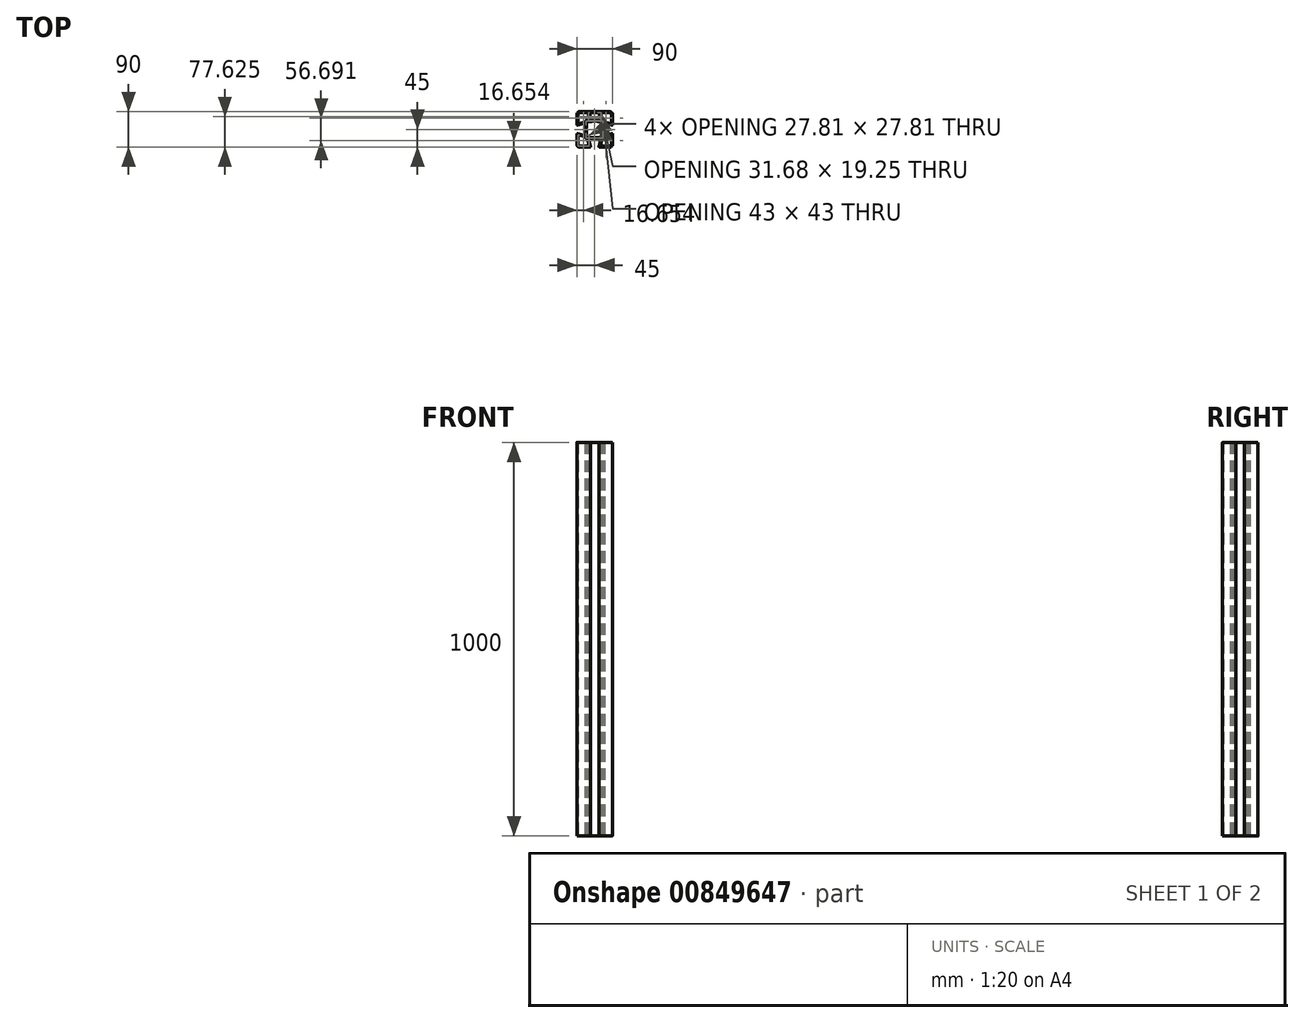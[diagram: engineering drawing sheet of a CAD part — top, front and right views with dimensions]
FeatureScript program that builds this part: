
annotation { "Feature Type Name" : "Feature", "Feature Type Description" : "" }
export const myFeature = defineFeature(function(context is Context, id is Id, definition is map)
    precondition{}
    {
        {
            var Q0;
            Q0=qCreatedBy(makeId("Top.planeOp"),FACE);
            var sketch = newSketch(context, id + "F0", { "sketchPlane" : qUnion([Q0])});
            skLineSegment(sketch, "E0", {"start": v(18.6, -24.48) * mm, "end": v(14.5, -39.73) * mm});
            skLineSegment(sketch, "E1", {"start": v(16.44, -42.25) * mm, "end": v(39, -42.25) * mm});
            skLineSegment(sketch, "E2", {"start": v(42.25, -39) * mm, "end": v(42.25, -16.44) * mm});
            skLineSegment(sketch, "E3", {"start": v(39.73, -14.5) * mm, "end": v(24.48, -18.6) * mm});
            skLineSegment(sketch, "E4", {"start": v(23, -20.53) * mm, "end": v(23, -21) * mm});
            skLineSegment(sketch, "E5", {"start": v(21, -23) * mm, "end": v(20.53, -23) * mm});
            skLineSegment(sketch, "E6", {"start": v(-24.48, -18.6) * mm, "end": v(-39.73, -14.5) * mm});
            skLineSegment(sketch, "E7", {"start": v(-42.25, -16.44) * mm, "end": v(-42.25, -39) * mm});
            skLineSegment(sketch, "E8", {"start": v(-39, -42.25) * mm, "end": v(-16.44, -42.25) * mm});
            skLineSegment(sketch, "E9", {"start": v(-14.5, -39.73) * mm, "end": v(-18.6, -24.48) * mm});
            skLineSegment(sketch, "E10", {"start": v(-20.53, -23) * mm, "end": v(-21, -23) * mm});
            skLineSegment(sketch, "E11", {"start": v(-23, -21) * mm, "end": v(-23, -20.53) * mm});
            skLineSegment(sketch, "E12", {"start": v(-14.84, 23) * mm, "end": v(-9.27, 23) * mm});
            skLineSegment(sketch, "E13", {"start": v(9.27, 23) * mm, "end": v(14.84, 23) * mm});
            skLineSegment(sketch, "E14", {"start": v(15.8, 24.26) * mm, "end": v(10.99, 42.25) * mm});
            skLineSegment(sketch, "E15", {"start": v(10.99, 42.25) * mm, "end": v(-10.99, 42.25) * mm});
            skLineSegment(sketch, "E16", {"start": v(-10.99, 42.25) * mm, "end": v(-15.8, 24.26) * mm});
            skLineSegment(sketch, "E17", {"start": v(9.27, -23) * mm, "end": v(14.84, -23) * mm});
            skLineSegment(sketch, "E18", {"start": v(-14.84, -23) * mm, "end": v(-9.27, -23) * mm});
            skLineSegment(sketch, "E19", {"start": v(-10.67, -43.43) * mm, "end": v(-15.8, -24.26) * mm});
            skLineSegment(sketch, "E20", {"start": v(-39, -45) * mm, "end": v(-11.88, -45) * mm});
            skLineSegment(sketch, "E21", {"start": v(-45, -11.88) * mm, "end": v(-45, -39) * mm});
            skLineSegment(sketch, "E22", {"start": v(-24.26, -15.8) * mm, "end": v(-43.43, -10.67) * mm});
            skLineSegment(sketch, "E23", {"start": v(-23, -9.27) * mm, "end": v(-23, -14.84) * mm});
            skLineSegment(sketch, "E24", {"start": v(-23, 14.84) * mm, "end": v(-23, 9.27) * mm});
            skLineSegment(sketch, "E25", {"start": v(-43.43, 10.67) * mm, "end": v(-24.26, 15.8) * mm});
            skLineSegment(sketch, "E26", {"start": v(-45, 39) * mm, "end": v(-45, 11.88) * mm});
            skLineSegment(sketch, "E27", {"start": v(39, 45) * mm, "end": v(-39, 45) * mm});
            skLineSegment(sketch, "E28", {"start": v(45, 11.88) * mm, "end": v(45, 39) * mm});
            skLineSegment(sketch, "E29", {"start": v(24.26, 15.8) * mm, "end": v(43.43, 10.67) * mm});
            skLineSegment(sketch, "E30", {"start": v(23, 9.27) * mm, "end": v(23, 14.84) * mm});
            skLineSegment(sketch, "E31", {"start": v(23, -14.84) * mm, "end": v(23, -9.27) * mm});
            skLineSegment(sketch, "E32", {"start": v(43.43, -10.67) * mm, "end": v(24.26, -15.8) * mm});
            skLineSegment(sketch, "E33", {"start": v(45, -39) * mm, "end": v(45, -11.88) * mm});
            skLineSegment(sketch, "E34", {"start": v(11.88, -45) * mm, "end": v(39, -45) * mm});
            skLineSegment(sketch, "E35", {"start": v(15.8, -24.26) * mm, "end": v(10.67, -43.43) * mm});
            skLineSegment(sketch, "E36", {"start": v(-19.25, -20.25) * mm, "end": v(-7.4, -20.25) * mm});
            skLineSegment(sketch, "E37", {"start": v(7.4, -20.25) * mm, "end": v(19.25, -20.25) * mm});
            skLineSegment(sketch, "E38", {"start": v(20.25, -19.25) * mm, "end": v(20.25, -7.4) * mm});
            skLineSegment(sketch, "E39", {"start": v(20.25, 7.4) * mm, "end": v(20.25, 19.25) * mm});
            skLineSegment(sketch, "E40", {"start": v(19.25, 20.25) * mm, "end": v(7.4, 20.25) * mm});
            skLineSegment(sketch, "E41", {"start": v(-7.4, 20.25) * mm, "end": v(-19.25, 20.25) * mm});
            skLineSegment(sketch, "E42", {"start": v(-20.25, 19.25) * mm, "end": v(-20.25, 7.4) * mm});
            skLineSegment(sketch, "E43", {"start": v(-20.25, -7.4) * mm, "end": v(-20.25, -19.25) * mm});
            skLineSegment(sketch, "E44", {"start": v(-18.6, 24.48) * mm, "end": v(-14.5, 39.73) * mm});
            skLineSegment(sketch, "E45", {"start": v(-16.44, 42.25) * mm, "end": v(-39, 42.25) * mm});
            skLineSegment(sketch, "E46", {"start": v(-42.25, 39) * mm, "end": v(-42.25, 16.44) * mm});
            skLineSegment(sketch, "E47", {"start": v(-39.73, 14.5) * mm, "end": v(-24.48, 18.6) * mm});
            skLineSegment(sketch, "E48", {"start": v(-23, 20.53) * mm, "end": v(-23, 21) * mm});
            skLineSegment(sketch, "E49", {"start": v(-21, 23) * mm, "end": v(-20.53, 23) * mm});
            skLineSegment(sketch, "E50", {"start": v(24.48, 18.6) * mm, "end": v(39.73, 14.5) * mm});
            skLineSegment(sketch, "E51", {"start": v(42.25, 16.44) * mm, "end": v(42.25, 39) * mm});
            skLineSegment(sketch, "E52", {"start": v(39, 42.25) * mm, "end": v(16.44, 42.25) * mm});
            skLineSegment(sketch, "E53", {"start": v(14.5, 39.73) * mm, "end": v(18.6, 24.48) * mm});
            skLineSegment(sketch, "E54", {"start": v(20.53, 23) * mm, "end": v(21, 23) * mm});
            skLineSegment(sketch, "E55", {"start": v(23, 21) * mm, "end": v(23, 20.53) * mm});
            skArc(sketch, "E56", {"start": v(20.53, -23) * mm, "mid": v(19.3, -23.41) * mm, "end": v(18.6, -24.48) * mm});
            skArc(sketch, "E57", {"start": v(14.5, -39.73) * mm, "mid": v(14.85, -41.47) * mm, "end": v(16.44, -42.25) * mm});
            skArc(sketch, "E58", {"start": v(39, -42.25) * mm, "mid": v(41.3, -41.3) * mm, "end": v(42.25, -39) * mm});
            skArc(sketch, "E59", {"start": v(42.25, -16.44) * mm, "mid": v(41.47, -14.85) * mm, "end": v(39.73, -14.5) * mm});
            skArc(sketch, "E60", {"start": v(24.48, -18.6) * mm, "mid": v(23.41, -19.3) * mm, "end": v(23, -20.53) * mm});
            skArc(sketch, "E61", {"start": v(21, -23) * mm, "mid": v(22.41, -22.41) * mm, "end": v(23, -21) * mm});
            skArc(sketch, "E62", {"start": v(-23, -20.53) * mm, "mid": v(-23.41, -19.3) * mm, "end": v(-24.48, -18.6) * mm});
            skArc(sketch, "E63", {"start": v(-39.73, -14.5) * mm, "mid": v(-41.47, -14.85) * mm, "end": v(-42.25, -16.44) * mm});
            skArc(sketch, "E64", {"start": v(-42.25, -39) * mm, "mid": v(-41.3, -41.3) * mm, "end": v(-39, -42.25) * mm});
            skArc(sketch, "E65", {"start": v(-16.44, -42.25) * mm, "mid": v(-14.85, -41.47) * mm, "end": v(-14.5, -39.73) * mm});
            skArc(sketch, "E66", {"start": v(-18.6, -24.48) * mm, "mid": v(-19.3, -23.41) * mm, "end": v(-20.53, -23) * mm});
            skArc(sketch, "E67", {"start": v(-23, -21) * mm, "mid": v(-22.41, -22.41) * mm, "end": v(-21, -23) * mm});
            skArc(sketch, "E68", {"start": v(-15.8, 24.26) * mm, "mid": v(-15.64, 23.4) * mm, "end": v(-14.84, 23) * mm});
            skArc(sketch, "E69", {"start": v(-9.27, 23) * mm, "mid": v(-9.06, 23.02) * mm, "end": v(-8.86, 23.09) * mm});
            skArc(sketch, "E70", {"start": v(8.86, 23.09) * mm, "mid": v(0, 25) * mm, "end": v(-8.86, 23.09) * mm});
            skArc(sketch, "E71", {"start": v(8.86, 23.09) * mm, "mid": v(9.06, 23.02) * mm, "end": v(9.27, 23) * mm});
            skArc(sketch, "E72", {"start": v(14.84, 23) * mm, "mid": v(15.64, 23.4) * mm, "end": v(15.8, 24.26) * mm});
            skArc(sketch, "E73", {"start": v(15.8, -24.26) * mm, "mid": v(15.64, -23.4) * mm, "end": v(14.84, -23) * mm});
            skArc(sketch, "E74", {"start": v(9.27, -23) * mm, "mid": v(9.06, -23.02) * mm, "end": v(8.86, -23.09) * mm});
            skArc(sketch, "E75", {"start": v(-8.86, -23.09) * mm, "mid": v(0, -25) * mm, "end": v(8.86, -23.09) * mm});
            skArc(sketch, "E76", {"start": v(-8.86, -23.09) * mm, "mid": v(-9.06, -23.02) * mm, "end": v(-9.27, -23) * mm});
            skArc(sketch, "E77", {"start": v(-14.84, -23) * mm, "mid": v(-15.64, -23.4) * mm, "end": v(-15.8, -24.26) * mm});
            skArc(sketch, "E78", {"start": v(-11.88, -45) * mm, "mid": v(-10.89, -44.51) * mm, "end": v(-10.67, -43.43) * mm});
            skArc(sketch, "E79", {"start": v(-45, -39) * mm, "mid": v(-43.24, -43.24) * mm, "end": v(-39, -45) * mm});
            skArc(sketch, "E80", {"start": v(-43.43, -10.67) * mm, "mid": v(-44.51, -10.89) * mm, "end": v(-45, -11.88) * mm});
            skArc(sketch, "E81", {"start": v(-24.26, -15.8) * mm, "mid": v(-23.4, -15.64) * mm, "end": v(-23, -14.84) * mm});
            skArc(sketch, "E82", {"start": v(-23, -9.27) * mm, "mid": v(-23.02, -9.06) * mm, "end": v(-23.09, -8.86) * mm});
            skArc(sketch, "E83", {"start": v(-23.09, 8.86) * mm, "mid": v(-25, 0) * mm, "end": v(-23.09, -8.86) * mm});
            skArc(sketch, "E84", {"start": v(-23.09, 8.86) * mm, "mid": v(-23.02, 9.06) * mm, "end": v(-23, 9.27) * mm});
            skArc(sketch, "E85", {"start": v(-23, 14.84) * mm, "mid": v(-23.4, 15.64) * mm, "end": v(-24.26, 15.8) * mm});
            skArc(sketch, "E86", {"start": v(-45, 11.88) * mm, "mid": v(-44.51, 10.89) * mm, "end": v(-43.43, 10.67) * mm});
            skArc(sketch, "E87", {"start": v(-39, 45) * mm, "mid": v(-43.24, 43.24) * mm, "end": v(-45, 39) * mm});
            skArc(sketch, "E88", {"start": v(45, 39) * mm, "mid": v(43.24, 43.24) * mm, "end": v(39, 45) * mm});
            skArc(sketch, "E89", {"start": v(43.43, 10.67) * mm, "mid": v(44.51, 10.89) * mm, "end": v(45, 11.88) * mm});
            skArc(sketch, "E90", {"start": v(24.26, 15.8) * mm, "mid": v(23.4, 15.64) * mm, "end": v(23, 14.84) * mm});
            skArc(sketch, "E91", {"start": v(23, 9.27) * mm, "mid": v(23.02, 9.06) * mm, "end": v(23.09, 8.86) * mm});
            skArc(sketch, "E92", {"start": v(23.09, -8.86) * mm, "mid": v(25, 0) * mm, "end": v(23.09, 8.86) * mm});
            skArc(sketch, "E93", {"start": v(23.09, -8.86) * mm, "mid": v(23.02, -9.06) * mm, "end": v(23, -9.27) * mm});
            skArc(sketch, "E94", {"start": v(23, -14.84) * mm, "mid": v(23.4, -15.64) * mm, "end": v(24.26, -15.8) * mm});
            skArc(sketch, "E95", {"start": v(45, -11.88) * mm, "mid": v(44.51, -10.89) * mm, "end": v(43.43, -10.67) * mm});
            skArc(sketch, "E96", {"start": v(39, -45) * mm, "mid": v(43.24, -43.24) * mm, "end": v(45, -39) * mm});
            skArc(sketch, "E97", {"start": v(10.67, -43.43) * mm, "mid": v(10.89, -44.51) * mm, "end": v(11.88, -45) * mm});
            skArc(sketch, "E98", {"start": v(-20.25, -19.25) * mm, "mid": v(-19.96, -19.96) * mm, "end": v(-19.25, -20.25) * mm});
            skArc(sketch, "E99", {"start": v(-7.07, -20.3) * mm, "mid": v(-7.23, -20.26) * mm, "end": v(-7.4, -20.25) * mm});
            skArc(sketch, "E100", {"start": v(-7.07, -20.3) * mm, "mid": v(0, -21.5) * mm, "end": v(7.07, -20.3) * mm});
            skArc(sketch, "E101", {"start": v(7.4, -20.25) * mm, "mid": v(7.23, -20.26) * mm, "end": v(7.07, -20.3) * mm});
            skArc(sketch, "E102", {"start": v(19.25, -20.25) * mm, "mid": v(19.96, -19.96) * mm, "end": v(20.25, -19.25) * mm});
            skArc(sketch, "E103", {"start": v(20.3, -7.07) * mm, "mid": v(20.26, -7.23) * mm, "end": v(20.25, -7.4) * mm});
            skArc(sketch, "E104", {"start": v(20.3, -7.07) * mm, "mid": v(21.5, 0) * mm, "end": v(20.3, 7.07) * mm});
            skArc(sketch, "E105", {"start": v(20.25, 7.4) * mm, "mid": v(20.26, 7.23) * mm, "end": v(20.3, 7.07) * mm});
            skArc(sketch, "E106", {"start": v(20.25, 19.25) * mm, "mid": v(19.96, 19.96) * mm, "end": v(19.25, 20.25) * mm});
            skArc(sketch, "E107", {"start": v(7.07, 20.3) * mm, "mid": v(7.23, 20.26) * mm, "end": v(7.4, 20.25) * mm});
            skArc(sketch, "E108", {"start": v(7.07, 20.3) * mm, "mid": v(0, 21.5) * mm, "end": v(-7.07, 20.3) * mm});
            skArc(sketch, "E109", {"start": v(-7.4, 20.25) * mm, "mid": v(-7.23, 20.26) * mm, "end": v(-7.07, 20.3) * mm});
            skArc(sketch, "E110", {"start": v(-19.25, 20.25) * mm, "mid": v(-19.96, 19.96) * mm, "end": v(-20.25, 19.25) * mm});
            skArc(sketch, "E111", {"start": v(-20.3, 7.07) * mm, "mid": v(-20.26, 7.23) * mm, "end": v(-20.25, 7.4) * mm});
            skArc(sketch, "E112", {"start": v(-20.3, 7.07) * mm, "mid": v(-21.5, 0) * mm, "end": v(-20.3, -7.07) * mm});
            skArc(sketch, "E113", {"start": v(-20.25, -7.4) * mm, "mid": v(-20.26, -7.23) * mm, "end": v(-20.3, -7.07) * mm});
            skArc(sketch, "E114", {"start": v(-20.53, 23) * mm, "mid": v(-19.3, 23.41) * mm, "end": v(-18.6, 24.48) * mm});
            skArc(sketch, "E115", {"start": v(-14.5, 39.73) * mm, "mid": v(-14.85, 41.47) * mm, "end": v(-16.44, 42.25) * mm});
            skArc(sketch, "E116", {"start": v(-39, 42.25) * mm, "mid": v(-41.3, 41.3) * mm, "end": v(-42.25, 39) * mm});
            skArc(sketch, "E117", {"start": v(-42.25, 16.44) * mm, "mid": v(-41.47, 14.85) * mm, "end": v(-39.73, 14.5) * mm});
            skArc(sketch, "E118", {"start": v(-24.48, 18.6) * mm, "mid": v(-23.41, 19.3) * mm, "end": v(-23, 20.53) * mm});
            skArc(sketch, "E119", {"start": v(-21, 23) * mm, "mid": v(-22.41, 22.41) * mm, "end": v(-23, 21) * mm});
            skArc(sketch, "E120", {"start": v(23, 20.53) * mm, "mid": v(23.41, 19.3) * mm, "end": v(24.48, 18.6) * mm});
            skArc(sketch, "E121", {"start": v(39.73, 14.5) * mm, "mid": v(41.47, 14.85) * mm, "end": v(42.25, 16.44) * mm});
            skArc(sketch, "E122", {"start": v(42.25, 39) * mm, "mid": v(41.3, 41.3) * mm, "end": v(39, 42.25) * mm});
            skArc(sketch, "E123", {"start": v(16.44, 42.25) * mm, "mid": v(14.85, 41.47) * mm, "end": v(14.5, 39.73) * mm});
            skArc(sketch, "E124", {"start": v(18.6, 24.48) * mm, "mid": v(19.3, 23.41) * mm, "end": v(20.53, 23) * mm});
            skArc(sketch, "E125", {"start": v(23, 21) * mm, "mid": v(22.41, 22.41) * mm, "end": v(21, 23) * mm});
            skLineSegment(sketch, "E126.1.0.0", {"start": v(116.44, -42.25) * mm, "end": v(139, -42.25) * mm});
            skLineSegment(sketch, "E126.1.0.1", {"start": v(143.43, -10.67) * mm, "end": v(124.26, -15.8) * mm});
            skLineSegment(sketch, "E126.1.0.2", {"start": v(139, 45) * mm, "end": v(61, 45) * mm});
            skLineSegment(sketch, "E126.1.0.3", {"start": v(120.25, 7.4) * mm, "end": v(120.25, 19.25) * mm});
            skLineSegment(sketch, "E126.1.0.4", {"start": v(92.6, 20.25) * mm, "end": v(80.75, 20.25) * mm});
            skLineSegment(sketch, "E126.1.0.5", {"start": v(107.4, -20.25) * mm, "end": v(119.25, -20.25) * mm});
            skArc(sketch, "E126.1.0.6", {"start": v(120.3, -7.07) * mm, "mid": v(121.5, 0) * mm, "end": v(120.3, 7.07) * mm});
            skLineSegment(sketch, "E126.1.0.7", {"start": v(115.8, 24.26) * mm, "end": v(110.99, 42.25) * mm});
            skLineSegment(sketch, "E126.1.0.8", {"start": v(89.33, -43.43) * mm, "end": v(84.2, -24.26) * mm});
            skLineSegment(sketch, "E126.1.0.9", {"start": v(75.74, -15.8) * mm, "end": v(56.57, -10.67) * mm});
            skArc(sketch, "E126.1.0.10", {"start": v(55, -39) * mm, "mid": v(56.76, -43.24) * mm, "end": v(61, -45) * mm});
            skArc(sketch, "E126.1.0.11", {"start": v(79.7, 7.07) * mm, "mid": v(78.5, 0) * mm, "end": v(79.7, -7.07) * mm});
            skArc(sketch, "E126.1.0.12", {"start": v(92.93, -20.3) * mm, "mid": v(100, -21.5) * mm, "end": v(107.07, -20.3) * mm});
            skLineSegment(sketch, "E126.1.0.13", {"start": v(89.01, 42.25) * mm, "end": v(84.2, 24.26) * mm});
            skLineSegment(sketch, "E126.1.0.14", {"start": v(139.73, -14.5) * mm, "end": v(124.48, -18.6) * mm});
            skLineSegment(sketch, "E126.1.0.15", {"start": v(75.52, -18.6) * mm, "end": v(60.27, -14.5) * mm});
            skLineSegment(sketch, "E126.1.0.16", {"start": v(61, -42.25) * mm, "end": v(83.56, -42.25) * mm});
            skLineSegment(sketch, "E126.1.0.17", {"start": v(83.56, 42.25) * mm, "end": v(61, 42.25) * mm});
            skLineSegment(sketch, "E126.1.0.18", {"start": v(139, 42.25) * mm, "end": v(116.44, 42.25) * mm});
            skLineSegment(sketch, "E126.1.0.19", {"start": v(110.99, 42.25) * mm, "end": v(89.01, 42.25) * mm});
            skLineSegment(sketch, "E126.1.0.20", {"start": v(124.26, 15.8) * mm, "end": v(143.43, 10.67) * mm});
            skLineSegment(sketch, "E126.1.0.21", {"start": v(79.75, -7.4) * mm, "end": v(79.75, -19.25) * mm});
            skArc(sketch, "E126.1.0.22", {"start": v(139, -45) * mm, "mid": v(143.24, -43.24) * mm, "end": v(145, -39) * mm});
            skLineSegment(sketch, "E126.1.0.23", {"start": v(80.75, -20.25) * mm, "end": v(92.6, -20.25) * mm});
            skLineSegment(sketch, "E126.1.0.24", {"start": v(124.48, 18.6) * mm, "end": v(139.73, 14.5) * mm});
            skArc(sketch, "E126.1.0.25", {"start": v(76.91, 8.86) * mm, "mid": v(75, 0) * mm, "end": v(76.91, -8.86) * mm});
            skLineSegment(sketch, "E126.1.0.26", {"start": v(79.75, 19.25) * mm, "end": v(79.75, 7.4) * mm});
            skArc(sketch, "E126.1.0.27", {"start": v(123.09, -8.86) * mm, "mid": v(125, 0) * mm, "end": v(123.09, 8.86) * mm});
            skLineSegment(sketch, "E126.1.0.28", {"start": v(60.27, 14.5) * mm, "end": v(75.52, 18.6) * mm});
            skLineSegment(sketch, "E126.1.0.29", {"start": v(85.5, -39.73) * mm, "end": v(81.4, -24.48) * mm});
            skLineSegment(sketch, "E126.1.0.30", {"start": v(111.88, -45) * mm, "end": v(139, -45) * mm});
            skLineSegment(sketch, "E126.1.0.31", {"start": v(55, 39) * mm, "end": v(55, 11.88) * mm});
            skLineSegment(sketch, "E126.1.0.32", {"start": v(57.75, -16.44) * mm, "end": v(57.75, -39) * mm});
            skLineSegment(sketch, "E126.1.0.33", {"start": v(120.25, -19.25) * mm, "end": v(120.25, -7.4) * mm});
            skLineSegment(sketch, "E126.1.0.34", {"start": v(57.75, 39) * mm, "end": v(57.75, 16.44) * mm});
            skArc(sketch, "E126.1.0.35", {"start": v(107.07, 20.3) * mm, "mid": v(100, 21.5) * mm, "end": v(92.93, 20.3) * mm});
            skArc(sketch, "E126.1.0.36", {"start": v(145, 39) * mm, "mid": v(143.24, 43.24) * mm, "end": v(139, 45) * mm});
            skLineSegment(sketch, "E126.1.0.37", {"start": v(114.5, 39.73) * mm, "end": v(118.6, 24.48) * mm});
            skLineSegment(sketch, "E126.1.0.38", {"start": v(118.6, -24.48) * mm, "end": v(114.5, -39.73) * mm});
            skArc(sketch, "E126.1.0.39", {"start": v(108.86, 23.09) * mm, "mid": v(100, 25) * mm, "end": v(91.14, 23.09) * mm});
            skLineSegment(sketch, "E126.1.0.40", {"start": v(55, -11.88) * mm, "end": v(55, -39) * mm});
            skArc(sketch, "E126.1.0.41", {"start": v(91.14, -23.09) * mm, "mid": v(100, -25) * mm, "end": v(108.86, -23.09) * mm});
            skLineSegment(sketch, "E126.1.0.42", {"start": v(115.8, -24.26) * mm, "end": v(110.67, -43.43) * mm});
            skLineSegment(sketch, "E126.1.0.43", {"start": v(61, -45) * mm, "end": v(88.12, -45) * mm});
            skLineSegment(sketch, "E126.1.0.44", {"start": v(142.25, 16.44) * mm, "end": v(142.25, 39) * mm});
            skLineSegment(sketch, "E126.1.0.45", {"start": v(81.4, 24.48) * mm, "end": v(85.5, 39.73) * mm});
            skLineSegment(sketch, "E126.1.0.46", {"start": v(145, -39) * mm, "end": v(145, -11.88) * mm});
            skLineSegment(sketch, "E126.1.0.47", {"start": v(56.57, 10.67) * mm, "end": v(75.74, 15.8) * mm});
            skLineSegment(sketch, "E126.1.0.48", {"start": v(142.25, -39) * mm, "end": v(142.25, -16.44) * mm});
            skArc(sketch, "E126.1.0.49", {"start": v(61, 45) * mm, "mid": v(56.76, 43.24) * mm, "end": v(55, 39) * mm});
            skLineSegment(sketch, "E126.1.0.50", {"start": v(145, 11.88) * mm, "end": v(145, 39) * mm});
            skLineSegment(sketch, "E126.1.0.51", {"start": v(119.25, 20.25) * mm, "end": v(107.4, 20.25) * mm});
            skArc(sketch, "E126.1.0.52", {"start": v(60.27, -14.5) * mm, "mid": v(58.53, -14.85) * mm, "end": v(57.75, -16.44) * mm});
            skArc(sketch, "E126.1.0.53", {"start": v(80.75, 20.25) * mm, "mid": v(80.04, 19.96) * mm, "end": v(79.75, 19.25) * mm});
            skArc(sketch, "E126.1.0.54", {"start": v(57.75, 16.44) * mm, "mid": v(58.53, 14.85) * mm, "end": v(60.27, 14.5) * mm});
            skArc(sketch, "E126.1.0.55", {"start": v(116.44, 42.25) * mm, "mid": v(114.85, 41.47) * mm, "end": v(114.5, 39.73) * mm});
            skArc(sketch, "E126.1.0.56", {"start": v(61, 42.25) * mm, "mid": v(58.7, 41.3) * mm, "end": v(57.75, 39) * mm});
            skArc(sketch, "E126.1.0.57", {"start": v(107.4, -20.25) * mm, "mid": v(107.23, -20.26) * mm, "end": v(107.07, -20.3) * mm});
            skArc(sketch, "E126.1.0.58", {"start": v(123, 21) * mm, "mid": v(122.41, 22.41) * mm, "end": v(121, 23) * mm});
            skLineSegment(sketch, "E126.1.0.59", {"start": v(77, 14.84) * mm, "end": v(77, 9.27) * mm});
            skArc(sketch, "E126.1.0.60", {"start": v(83.56, -42.25) * mm, "mid": v(85.15, -41.47) * mm, "end": v(85.5, -39.73) * mm});
            skArc(sketch, "E126.1.0.61", {"start": v(145, -11.88) * mm, "mid": v(144.51, -10.89) * mm, "end": v(143.43, -10.67) * mm});
            skArc(sketch, "E126.1.0.62", {"start": v(77, 14.84) * mm, "mid": v(76.6, 15.64) * mm, "end": v(75.74, 15.8) * mm});
            skArc(sketch, "E126.1.0.63", {"start": v(123, 20.53) * mm, "mid": v(123.41, 19.3) * mm, "end": v(124.48, 18.6) * mm});
            skLineSegment(sketch, "E126.1.0.64", {"start": v(85.16, -23) * mm, "end": v(90.73, -23) * mm});
            skArc(sketch, "E126.1.0.65", {"start": v(142.25, -16.44) * mm, "mid": v(141.47, -14.85) * mm, "end": v(139.73, -14.5) * mm});
            skArc(sketch, "E126.1.0.66", {"start": v(84.2, 24.26) * mm, "mid": v(84.36, 23.4) * mm, "end": v(85.16, 23) * mm});
            skArc(sketch, "E126.1.0.67", {"start": v(56.57, -10.67) * mm, "mid": v(55.49, -10.89) * mm, "end": v(55, -11.88) * mm});
            skArc(sketch, "E126.1.0.68", {"start": v(76.91, 8.86) * mm, "mid": v(76.98, 9.06) * mm, "end": v(77, 9.27) * mm});
            skArc(sketch, "E126.1.0.69", {"start": v(85.16, -23) * mm, "mid": v(84.36, -23.4) * mm, "end": v(84.2, -24.26) * mm});
            skArc(sketch, "E126.1.0.70", {"start": v(120.25, 19.25) * mm, "mid": v(119.96, 19.96) * mm, "end": v(119.25, 20.25) * mm});
            skLineSegment(sketch, "E126.1.0.71", {"start": v(109.27, -23) * mm, "end": v(114.84, -23) * mm});
            skLineSegment(sketch, "E126.1.0.72", {"start": v(85.16, 23) * mm, "end": v(90.73, 23) * mm});
            skArc(sketch, "E126.1.0.73", {"start": v(109.27, -23) * mm, "mid": v(109.06, -23.02) * mm, "end": v(108.86, -23.09) * mm});
            skArc(sketch, "E126.1.0.74", {"start": v(55, 11.88) * mm, "mid": v(55.49, 10.89) * mm, "end": v(56.57, 10.67) * mm});
            skArc(sketch, "E126.1.0.75", {"start": v(139.73, 14.5) * mm, "mid": v(141.47, 14.85) * mm, "end": v(142.25, 16.44) * mm});
            skArc(sketch, "E126.1.0.76", {"start": v(88.12, -45) * mm, "mid": v(89.11, -44.51) * mm, "end": v(89.33, -43.43) * mm});
            skArc(sketch, "E126.1.0.77", {"start": v(110.67, -43.43) * mm, "mid": v(110.89, -44.51) * mm, "end": v(111.88, -45) * mm});
            skLineSegment(sketch, "E126.1.0.78", {"start": v(120.53, 23) * mm, "end": v(121, 23) * mm});
            skArc(sketch, "E126.1.0.79", {"start": v(118.6, 24.48) * mm, "mid": v(119.3, 23.41) * mm, "end": v(120.53, 23) * mm});
            skLineSegment(sketch, "E126.1.0.80", {"start": v(123, 21) * mm, "end": v(123, 20.53) * mm});
            skArc(sketch, "E126.1.0.81", {"start": v(114.5, -39.73) * mm, "mid": v(114.85, -41.47) * mm, "end": v(116.44, -42.25) * mm});
            skArc(sketch, "E126.1.0.82", {"start": v(143.43, 10.67) * mm, "mid": v(144.51, 10.89) * mm, "end": v(145, 11.88) * mm});
            skArc(sketch, "E126.1.0.83", {"start": v(85.5, 39.73) * mm, "mid": v(85.15, 41.47) * mm, "end": v(83.56, 42.25) * mm});
            skLineSegment(sketch, "E126.1.0.84", {"start": v(123, -14.84) * mm, "end": v(123, -9.27) * mm});
            skArc(sketch, "E126.1.0.85", {"start": v(119.25, -20.25) * mm, "mid": v(119.96, -19.96) * mm, "end": v(120.25, -19.25) * mm});
            skArc(sketch, "E126.1.0.86", {"start": v(107.07, 20.3) * mm, "mid": v(107.23, 20.26) * mm, "end": v(107.4, 20.25) * mm});
            skArc(sketch, "E126.1.0.87", {"start": v(124.26, 15.8) * mm, "mid": v(123.4, 15.64) * mm, "end": v(123, 14.84) * mm});
            skArc(sketch, "E126.1.0.88", {"start": v(108.86, 23.09) * mm, "mid": v(109.06, 23.02) * mm, "end": v(109.27, 23) * mm});
            skArc(sketch, "E126.1.0.89", {"start": v(115.8, -24.26) * mm, "mid": v(115.64, -23.4) * mm, "end": v(114.84, -23) * mm});
            skArc(sketch, "E126.1.0.90", {"start": v(114.84, 23) * mm, "mid": v(115.64, 23.4) * mm, "end": v(115.8, 24.26) * mm});
            skArc(sketch, "E126.1.0.91", {"start": v(123, -14.84) * mm, "mid": v(123.4, -15.64) * mm, "end": v(124.26, -15.8) * mm});
            skArc(sketch, "E126.1.0.92", {"start": v(57.75, -39) * mm, "mid": v(58.7, -41.3) * mm, "end": v(61, -42.25) * mm});
            skArc(sketch, "E126.1.0.93", {"start": v(75.52, 18.6) * mm, "mid": v(76.59, 19.3) * mm, "end": v(77, 20.53) * mm});
            skLineSegment(sketch, "E126.1.0.94", {"start": v(123, 9.27) * mm, "end": v(123, 14.84) * mm});
            skArc(sketch, "E126.1.0.95", {"start": v(75.74, -15.8) * mm, "mid": v(76.6, -15.64) * mm, "end": v(77, -14.84) * mm});
            skArc(sketch, "E126.1.0.96", {"start": v(139, -42.25) * mm, "mid": v(141.3, -41.3) * mm, "end": v(142.25, -39) * mm});
            skLineSegment(sketch, "E126.1.0.97", {"start": v(109.27, 23) * mm, "end": v(114.84, 23) * mm});
            skLineSegment(sketch, "E126.1.0.98", {"start": v(77, -9.27) * mm, "end": v(77, -14.84) * mm});
            skArc(sketch, "E126.1.0.99", {"start": v(120.53, -23) * mm, "mid": v(119.3, -23.41) * mm, "end": v(118.6, -24.48) * mm});
            skArc(sketch, "E126.1.0.100", {"start": v(142.25, 39) * mm, "mid": v(141.3, 41.3) * mm, "end": v(139, 42.25) * mm});
            skArc(sketch, "E126.1.0.101", {"start": v(124.48, -18.6) * mm, "mid": v(123.41, -19.3) * mm, "end": v(123, -20.53) * mm});
            skLineSegment(sketch, "E126.1.0.102", {"start": v(79, 23) * mm, "end": v(79.47, 23) * mm});
            skArc(sketch, "E126.1.0.103", {"start": v(120.25, 7.4) * mm, "mid": v(120.26, 7.23) * mm, "end": v(120.3, 7.07) * mm});
            skLineSegment(sketch, "E126.1.0.104", {"start": v(121, -23) * mm, "end": v(120.53, -23) * mm});
            skArc(sketch, "E126.1.0.105", {"start": v(79, 23) * mm, "mid": v(77.59, 22.41) * mm, "end": v(77, 21) * mm});
            skArc(sketch, "E126.1.0.106", {"start": v(92.6, 20.25) * mm, "mid": v(92.77, 20.26) * mm, "end": v(92.93, 20.3) * mm});
            skArc(sketch, "E126.1.0.107", {"start": v(120.3, -7.07) * mm, "mid": v(120.26, -7.23) * mm, "end": v(120.25, -7.4) * mm});
            skLineSegment(sketch, "E126.1.0.108", {"start": v(77, 20.53) * mm, "end": v(77, 21) * mm});
            skArc(sketch, "E126.1.0.109", {"start": v(77, -9.27) * mm, "mid": v(76.98, -9.06) * mm, "end": v(76.91, -8.86) * mm});
            skArc(sketch, "E126.1.0.110", {"start": v(92.93, -20.3) * mm, "mid": v(92.77, -20.26) * mm, "end": v(92.6, -20.25) * mm});
            skArc(sketch, "E126.1.0.111", {"start": v(79.75, -7.4) * mm, "mid": v(79.74, -7.23) * mm, "end": v(79.7, -7.07) * mm});
            skArc(sketch, "E126.1.0.112", {"start": v(123, 9.27) * mm, "mid": v(123.02, 9.06) * mm, "end": v(123.09, 8.86) * mm});
            skArc(sketch, "E126.1.0.113", {"start": v(91.14, -23.09) * mm, "mid": v(90.94, -23.02) * mm, "end": v(90.73, -23) * mm});
            skArc(sketch, "E126.1.0.114", {"start": v(121, -23) * mm, "mid": v(122.41, -22.41) * mm, "end": v(123, -21) * mm});
            skArc(sketch, "E126.1.0.115", {"start": v(90.73, 23) * mm, "mid": v(90.94, 23.02) * mm, "end": v(91.14, 23.09) * mm});
            skArc(sketch, "E126.1.0.116", {"start": v(77, -20.53) * mm, "mid": v(76.59, -19.3) * mm, "end": v(75.52, -18.6) * mm});
            skArc(sketch, "E126.1.0.117", {"start": v(79.75, -19.25) * mm, "mid": v(80.04, -19.96) * mm, "end": v(80.75, -20.25) * mm});
            skArc(sketch, "E126.1.0.118", {"start": v(79.7, 7.07) * mm, "mid": v(79.74, 7.23) * mm, "end": v(79.75, 7.4) * mm});
            skArc(sketch, "E126.1.0.119", {"start": v(79.47, 23) * mm, "mid": v(80.7, 23.41) * mm, "end": v(81.4, 24.48) * mm});
            skLineSegment(sketch, "E126.1.0.120", {"start": v(79.47, -23) * mm, "end": v(79, -23) * mm});
            skArc(sketch, "E126.1.0.121", {"start": v(77, -21) * mm, "mid": v(77.59, -22.41) * mm, "end": v(79, -23) * mm});
            skArc(sketch, "E126.1.0.122", {"start": v(123.09, -8.86) * mm, "mid": v(123.02, -9.06) * mm, "end": v(123, -9.27) * mm});
            skLineSegment(sketch, "E126.1.0.123", {"start": v(77, -21) * mm, "end": v(77, -20.53) * mm});
            skArc(sketch, "E126.1.0.124", {"start": v(81.4, -24.48) * mm, "mid": v(80.7, -23.41) * mm, "end": v(79.47, -23) * mm});
            skLineSegment(sketch, "E126.1.0.125", {"start": v(123, -20.53) * mm, "end": v(123, -21) * mm});
            skLineSegment(sketch, "E126.2.0.0", {"start": v(216.44, -42.25) * mm, "end": v(239, -42.25) * mm});
            skLineSegment(sketch, "E126.2.0.1", {"start": v(243.43, -10.67) * mm, "end": v(224.26, -15.8) * mm});
            skLineSegment(sketch, "E126.2.0.2", {"start": v(239, 45) * mm, "end": v(161, 45) * mm});
            skLineSegment(sketch, "E126.2.0.3", {"start": v(220.25, 7.4) * mm, "end": v(220.25, 19.25) * mm});
            skLineSegment(sketch, "E126.2.0.4", {"start": v(192.6, 20.25) * mm, "end": v(180.75, 20.25) * mm});
            skLineSegment(sketch, "E126.2.0.5", {"start": v(207.4, -20.25) * mm, "end": v(219.25, -20.25) * mm});
            skArc(sketch, "E126.2.0.6", {"start": v(220.3, -7.07) * mm, "mid": v(221.5, 0) * mm, "end": v(220.3, 7.07) * mm});
            skLineSegment(sketch, "E126.2.0.7", {"start": v(215.8, 24.26) * mm, "end": v(210.99, 42.25) * mm});
            skLineSegment(sketch, "E126.2.0.8", {"start": v(189.33, -43.43) * mm, "end": v(184.2, -24.26) * mm});
            skLineSegment(sketch, "E126.2.0.9", {"start": v(175.74, -15.8) * mm, "end": v(156.57, -10.67) * mm});
            skArc(sketch, "E126.2.0.10", {"start": v(155, -39) * mm, "mid": v(156.76, -43.24) * mm, "end": v(161, -45) * mm});
            skArc(sketch, "E126.2.0.11", {"start": v(179.7, 7.07) * mm, "mid": v(178.5, 0) * mm, "end": v(179.7, -7.07) * mm});
            skArc(sketch, "E126.2.0.12", {"start": v(192.93, -20.3) * mm, "mid": v(200, -21.5) * mm, "end": v(207.07, -20.3) * mm});
            skLineSegment(sketch, "E126.2.0.13", {"start": v(189.01, 42.25) * mm, "end": v(184.2, 24.26) * mm});
            skLineSegment(sketch, "E126.2.0.14", {"start": v(239.73, -14.5) * mm, "end": v(224.48, -18.6) * mm});
            skLineSegment(sketch, "E126.2.0.15", {"start": v(175.52, -18.6) * mm, "end": v(160.27, -14.5) * mm});
            skLineSegment(sketch, "E126.2.0.16", {"start": v(161, -42.25) * mm, "end": v(183.56, -42.25) * mm});
            skLineSegment(sketch, "E126.2.0.17", {"start": v(183.56, 42.25) * mm, "end": v(161, 42.25) * mm});
            skLineSegment(sketch, "E126.2.0.18", {"start": v(239, 42.25) * mm, "end": v(216.44, 42.25) * mm});
            skLineSegment(sketch, "E126.2.0.19", {"start": v(210.99, 42.25) * mm, "end": v(189.01, 42.25) * mm});
            skLineSegment(sketch, "E126.2.0.20", {"start": v(224.26, 15.8) * mm, "end": v(243.43, 10.67) * mm});
            skLineSegment(sketch, "E126.2.0.21", {"start": v(179.75, -7.4) * mm, "end": v(179.75, -19.25) * mm});
            skArc(sketch, "E126.2.0.22", {"start": v(239, -45) * mm, "mid": v(243.24, -43.24) * mm, "end": v(245, -39) * mm});
            skLineSegment(sketch, "E126.2.0.23", {"start": v(180.75, -20.25) * mm, "end": v(192.6, -20.25) * mm});
            skLineSegment(sketch, "E126.2.0.24", {"start": v(224.48, 18.6) * mm, "end": v(239.73, 14.5) * mm});
            skArc(sketch, "E126.2.0.25", {"start": v(176.91, 8.86) * mm, "mid": v(175, 0) * mm, "end": v(176.91, -8.86) * mm});
            skLineSegment(sketch, "E126.2.0.26", {"start": v(179.75, 19.25) * mm, "end": v(179.75, 7.4) * mm});
            skArc(sketch, "E126.2.0.27", {"start": v(223.09, -8.86) * mm, "mid": v(225, 0) * mm, "end": v(223.09, 8.86) * mm});
            skLineSegment(sketch, "E126.2.0.28", {"start": v(160.27, 14.5) * mm, "end": v(175.52, 18.6) * mm});
            skLineSegment(sketch, "E126.2.0.29", {"start": v(185.5, -39.73) * mm, "end": v(181.4, -24.48) * mm});
            skLineSegment(sketch, "E126.2.0.30", {"start": v(211.88, -45) * mm, "end": v(239, -45) * mm});
            skLineSegment(sketch, "E126.2.0.31", {"start": v(155, 39) * mm, "end": v(155, 11.88) * mm});
            skLineSegment(sketch, "E126.2.0.32", {"start": v(157.75, -16.44) * mm, "end": v(157.75, -39) * mm});
            skLineSegment(sketch, "E126.2.0.33", {"start": v(220.25, -19.25) * mm, "end": v(220.25, -7.4) * mm});
            skLineSegment(sketch, "E126.2.0.34", {"start": v(157.75, 39) * mm, "end": v(157.75, 16.44) * mm});
            skArc(sketch, "E126.2.0.35", {"start": v(207.07, 20.3) * mm, "mid": v(200, 21.5) * mm, "end": v(192.93, 20.3) * mm});
            skArc(sketch, "E126.2.0.36", {"start": v(245, 39) * mm, "mid": v(243.24, 43.24) * mm, "end": v(239, 45) * mm});
            skLineSegment(sketch, "E126.2.0.37", {"start": v(214.5, 39.73) * mm, "end": v(218.6, 24.48) * mm});
            skLineSegment(sketch, "E126.2.0.38", {"start": v(218.6, -24.48) * mm, "end": v(214.5, -39.73) * mm});
            skArc(sketch, "E126.2.0.39", {"start": v(208.86, 23.09) * mm, "mid": v(200, 25) * mm, "end": v(191.14, 23.09) * mm});
            skLineSegment(sketch, "E126.2.0.40", {"start": v(155, -11.88) * mm, "end": v(155, -39) * mm});
            skArc(sketch, "E126.2.0.41", {"start": v(191.14, -23.09) * mm, "mid": v(200, -25) * mm, "end": v(208.86, -23.09) * mm});
            skLineSegment(sketch, "E126.2.0.42", {"start": v(215.8, -24.26) * mm, "end": v(210.67, -43.43) * mm});
            skLineSegment(sketch, "E126.2.0.43", {"start": v(161, -45) * mm, "end": v(188.12, -45) * mm});
            skLineSegment(sketch, "E126.2.0.44", {"start": v(242.25, 16.44) * mm, "end": v(242.25, 39) * mm});
            skLineSegment(sketch, "E126.2.0.45", {"start": v(181.4, 24.48) * mm, "end": v(185.5, 39.73) * mm});
            skLineSegment(sketch, "E126.2.0.46", {"start": v(245, -39) * mm, "end": v(245, -11.88) * mm});
            skLineSegment(sketch, "E126.2.0.47", {"start": v(156.57, 10.67) * mm, "end": v(175.74, 15.8) * mm});
            skLineSegment(sketch, "E126.2.0.48", {"start": v(242.25, -39) * mm, "end": v(242.25, -16.44) * mm});
            skArc(sketch, "E126.2.0.49", {"start": v(161, 45) * mm, "mid": v(156.76, 43.24) * mm, "end": v(155, 39) * mm});
            skLineSegment(sketch, "E126.2.0.50", {"start": v(245, 11.88) * mm, "end": v(245, 39) * mm});
            skLineSegment(sketch, "E126.2.0.51", {"start": v(219.25, 20.25) * mm, "end": v(207.4, 20.25) * mm});
            skArc(sketch, "E126.2.0.52", {"start": v(160.27, -14.5) * mm, "mid": v(158.53, -14.85) * mm, "end": v(157.75, -16.44) * mm});
            skArc(sketch, "E126.2.0.53", {"start": v(180.75, 20.25) * mm, "mid": v(180.04, 19.96) * mm, "end": v(179.75, 19.25) * mm});
            skArc(sketch, "E126.2.0.54", {"start": v(157.75, 16.44) * mm, "mid": v(158.53, 14.85) * mm, "end": v(160.27, 14.5) * mm});
            skArc(sketch, "E126.2.0.55", {"start": v(216.44, 42.25) * mm, "mid": v(214.85, 41.47) * mm, "end": v(214.5, 39.73) * mm});
            skArc(sketch, "E126.2.0.56", {"start": v(161, 42.25) * mm, "mid": v(158.7, 41.3) * mm, "end": v(157.75, 39) * mm});
            skArc(sketch, "E126.2.0.57", {"start": v(207.4, -20.25) * mm, "mid": v(207.23, -20.26) * mm, "end": v(207.07, -20.3) * mm});
            skArc(sketch, "E126.2.0.58", {"start": v(223, 21) * mm, "mid": v(222.41, 22.41) * mm, "end": v(221, 23) * mm});
            skLineSegment(sketch, "E126.2.0.59", {"start": v(177, 14.84) * mm, "end": v(177, 9.27) * mm});
            skArc(sketch, "E126.2.0.60", {"start": v(183.56, -42.25) * mm, "mid": v(185.15, -41.47) * mm, "end": v(185.5, -39.73) * mm});
            skArc(sketch, "E126.2.0.61", {"start": v(245, -11.88) * mm, "mid": v(244.51, -10.89) * mm, "end": v(243.43, -10.67) * mm});
            skArc(sketch, "E126.2.0.62", {"start": v(177, 14.84) * mm, "mid": v(176.6, 15.64) * mm, "end": v(175.74, 15.8) * mm});
            skArc(sketch, "E126.2.0.63", {"start": v(223, 20.53) * mm, "mid": v(223.41, 19.3) * mm, "end": v(224.48, 18.6) * mm});
            skLineSegment(sketch, "E126.2.0.64", {"start": v(185.16, -23) * mm, "end": v(190.73, -23) * mm});
            skArc(sketch, "E126.2.0.65", {"start": v(242.25, -16.44) * mm, "mid": v(241.47, -14.85) * mm, "end": v(239.73, -14.5) * mm});
            skArc(sketch, "E126.2.0.66", {"start": v(184.2, 24.26) * mm, "mid": v(184.36, 23.4) * mm, "end": v(185.16, 23) * mm});
            skArc(sketch, "E126.2.0.67", {"start": v(156.57, -10.67) * mm, "mid": v(155.49, -10.89) * mm, "end": v(155, -11.88) * mm});
            skArc(sketch, "E126.2.0.68", {"start": v(176.91, 8.86) * mm, "mid": v(176.98, 9.06) * mm, "end": v(177, 9.27) * mm});
            skArc(sketch, "E126.2.0.69", {"start": v(185.16, -23) * mm, "mid": v(184.36, -23.4) * mm, "end": v(184.2, -24.26) * mm});
            skArc(sketch, "E126.2.0.70", {"start": v(220.25, 19.25) * mm, "mid": v(219.96, 19.96) * mm, "end": v(219.25, 20.25) * mm});
            skLineSegment(sketch, "E126.2.0.71", {"start": v(209.27, -23) * mm, "end": v(214.84, -23) * mm});
            skLineSegment(sketch, "E126.2.0.72", {"start": v(185.16, 23) * mm, "end": v(190.73, 23) * mm});
            skArc(sketch, "E126.2.0.73", {"start": v(209.27, -23) * mm, "mid": v(209.06, -23.02) * mm, "end": v(208.86, -23.09) * mm});
            skArc(sketch, "E126.2.0.74", {"start": v(155, 11.88) * mm, "mid": v(155.49, 10.89) * mm, "end": v(156.57, 10.67) * mm});
            skArc(sketch, "E126.2.0.75", {"start": v(239.73, 14.5) * mm, "mid": v(241.47, 14.85) * mm, "end": v(242.25, 16.44) * mm});
            skArc(sketch, "E126.2.0.76", {"start": v(188.12, -45) * mm, "mid": v(189.11, -44.51) * mm, "end": v(189.33, -43.43) * mm});
            skArc(sketch, "E126.2.0.77", {"start": v(210.67, -43.43) * mm, "mid": v(210.89, -44.51) * mm, "end": v(211.88, -45) * mm});
            skLineSegment(sketch, "E126.2.0.78", {"start": v(220.53, 23) * mm, "end": v(221, 23) * mm});
            skArc(sketch, "E126.2.0.79", {"start": v(218.6, 24.48) * mm, "mid": v(219.3, 23.41) * mm, "end": v(220.53, 23) * mm});
            skLineSegment(sketch, "E126.2.0.80", {"start": v(223, 21) * mm, "end": v(223, 20.53) * mm});
            skArc(sketch, "E126.2.0.81", {"start": v(214.5, -39.73) * mm, "mid": v(214.85, -41.47) * mm, "end": v(216.44, -42.25) * mm});
            skArc(sketch, "E126.2.0.82", {"start": v(243.43, 10.67) * mm, "mid": v(244.51, 10.89) * mm, "end": v(245, 11.88) * mm});
            skArc(sketch, "E126.2.0.83", {"start": v(185.5, 39.73) * mm, "mid": v(185.15, 41.47) * mm, "end": v(183.56, 42.25) * mm});
            skLineSegment(sketch, "E126.2.0.84", {"start": v(223, -14.84) * mm, "end": v(223, -9.27) * mm});
            skArc(sketch, "E126.2.0.85", {"start": v(219.25, -20.25) * mm, "mid": v(219.96, -19.96) * mm, "end": v(220.25, -19.25) * mm});
            skArc(sketch, "E126.2.0.86", {"start": v(207.07, 20.3) * mm, "mid": v(207.23, 20.26) * mm, "end": v(207.4, 20.25) * mm});
            skArc(sketch, "E126.2.0.87", {"start": v(224.26, 15.8) * mm, "mid": v(223.4, 15.64) * mm, "end": v(223, 14.84) * mm});
            skArc(sketch, "E126.2.0.88", {"start": v(208.86, 23.09) * mm, "mid": v(209.06, 23.02) * mm, "end": v(209.27, 23) * mm});
            skArc(sketch, "E126.2.0.89", {"start": v(215.8, -24.26) * mm, "mid": v(215.64, -23.4) * mm, "end": v(214.84, -23) * mm});
            skArc(sketch, "E126.2.0.90", {"start": v(214.84, 23) * mm, "mid": v(215.64, 23.4) * mm, "end": v(215.8, 24.26) * mm});
            skArc(sketch, "E126.2.0.91", {"start": v(223, -14.84) * mm, "mid": v(223.4, -15.64) * mm, "end": v(224.26, -15.8) * mm});
            skArc(sketch, "E126.2.0.92", {"start": v(157.75, -39) * mm, "mid": v(158.7, -41.3) * mm, "end": v(161, -42.25) * mm});
            skArc(sketch, "E126.2.0.93", {"start": v(175.52, 18.6) * mm, "mid": v(176.59, 19.3) * mm, "end": v(177, 20.53) * mm});
            skLineSegment(sketch, "E126.2.0.94", {"start": v(223, 9.27) * mm, "end": v(223, 14.84) * mm});
            skArc(sketch, "E126.2.0.95", {"start": v(175.74, -15.8) * mm, "mid": v(176.6, -15.64) * mm, "end": v(177, -14.84) * mm});
            skArc(sketch, "E126.2.0.96", {"start": v(239, -42.25) * mm, "mid": v(241.3, -41.3) * mm, "end": v(242.25, -39) * mm});
            skLineSegment(sketch, "E126.2.0.97", {"start": v(209.27, 23) * mm, "end": v(214.84, 23) * mm});
            skLineSegment(sketch, "E126.2.0.98", {"start": v(177, -9.27) * mm, "end": v(177, -14.84) * mm});
            skArc(sketch, "E126.2.0.99", {"start": v(220.53, -23) * mm, "mid": v(219.3, -23.41) * mm, "end": v(218.6, -24.48) * mm});
            skArc(sketch, "E126.2.0.100", {"start": v(242.25, 39) * mm, "mid": v(241.3, 41.3) * mm, "end": v(239, 42.25) * mm});
            skArc(sketch, "E126.2.0.101", {"start": v(224.48, -18.6) * mm, "mid": v(223.41, -19.3) * mm, "end": v(223, -20.53) * mm});
            skLineSegment(sketch, "E126.2.0.102", {"start": v(179, 23) * mm, "end": v(179.47, 23) * mm});
            skArc(sketch, "E126.2.0.103", {"start": v(220.25, 7.4) * mm, "mid": v(220.26, 7.23) * mm, "end": v(220.3, 7.07) * mm});
            skLineSegment(sketch, "E126.2.0.104", {"start": v(221, -23) * mm, "end": v(220.53, -23) * mm});
            skArc(sketch, "E126.2.0.105", {"start": v(179, 23) * mm, "mid": v(177.59, 22.41) * mm, "end": v(177, 21) * mm});
            skArc(sketch, "E126.2.0.106", {"start": v(192.6, 20.25) * mm, "mid": v(192.77, 20.26) * mm, "end": v(192.93, 20.3) * mm});
            skArc(sketch, "E126.2.0.107", {"start": v(220.3, -7.07) * mm, "mid": v(220.26, -7.23) * mm, "end": v(220.25, -7.4) * mm});
            skLineSegment(sketch, "E126.2.0.108", {"start": v(177, 20.53) * mm, "end": v(177, 21) * mm});
            skArc(sketch, "E126.2.0.109", {"start": v(177, -9.27) * mm, "mid": v(176.98, -9.06) * mm, "end": v(176.91, -8.86) * mm});
            skArc(sketch, "E126.2.0.110", {"start": v(192.93, -20.3) * mm, "mid": v(192.77, -20.26) * mm, "end": v(192.6, -20.25) * mm});
            skArc(sketch, "E126.2.0.111", {"start": v(179.75, -7.4) * mm, "mid": v(179.74, -7.23) * mm, "end": v(179.7, -7.07) * mm});
            skArc(sketch, "E126.2.0.112", {"start": v(223, 9.27) * mm, "mid": v(223.02, 9.06) * mm, "end": v(223.09, 8.86) * mm});
            skArc(sketch, "E126.2.0.113", {"start": v(191.14, -23.09) * mm, "mid": v(190.94, -23.02) * mm, "end": v(190.73, -23) * mm});
            skArc(sketch, "E126.2.0.114", {"start": v(221, -23) * mm, "mid": v(222.41, -22.41) * mm, "end": v(223, -21) * mm});
            skArc(sketch, "E126.2.0.115", {"start": v(190.73, 23) * mm, "mid": v(190.94, 23.02) * mm, "end": v(191.14, 23.09) * mm});
            skArc(sketch, "E126.2.0.116", {"start": v(177, -20.53) * mm, "mid": v(176.59, -19.3) * mm, "end": v(175.52, -18.6) * mm});
            skArc(sketch, "E126.2.0.117", {"start": v(179.75, -19.25) * mm, "mid": v(180.04, -19.96) * mm, "end": v(180.75, -20.25) * mm});
            skArc(sketch, "E126.2.0.118", {"start": v(179.7, 7.07) * mm, "mid": v(179.74, 7.23) * mm, "end": v(179.75, 7.4) * mm});
            skArc(sketch, "E126.2.0.119", {"start": v(179.47, 23) * mm, "mid": v(180.7, 23.41) * mm, "end": v(181.4, 24.48) * mm});
            skLineSegment(sketch, "E126.2.0.120", {"start": v(179.47, -23) * mm, "end": v(179, -23) * mm});
            skArc(sketch, "E126.2.0.121", {"start": v(177, -21) * mm, "mid": v(177.59, -22.41) * mm, "end": v(179, -23) * mm});
            skArc(sketch, "E126.2.0.122", {"start": v(223.09, -8.86) * mm, "mid": v(223.02, -9.06) * mm, "end": v(223, -9.27) * mm});
            skLineSegment(sketch, "E126.2.0.123", {"start": v(177, -21) * mm, "end": v(177, -20.53) * mm});
            skArc(sketch, "E126.2.0.124", {"start": v(181.4, -24.48) * mm, "mid": v(180.7, -23.41) * mm, "end": v(179.47, -23) * mm});
            skLineSegment(sketch, "E126.2.0.125", {"start": v(223, -20.53) * mm, "end": v(223, -21) * mm});
            skLineSegment(sketch, "E126.3.0.0", {"start": v(316.44, -42.25) * mm, "end": v(339, -42.25) * mm});
            skLineSegment(sketch, "E126.3.0.1", {"start": v(343.43, -10.67) * mm, "end": v(324.26, -15.8) * mm});
            skLineSegment(sketch, "E126.3.0.2", {"start": v(339, 45) * mm, "end": v(261, 45) * mm});
            skLineSegment(sketch, "E126.3.0.3", {"start": v(320.25, 7.4) * mm, "end": v(320.25, 19.25) * mm});
            skLineSegment(sketch, "E126.3.0.4", {"start": v(292.6, 20.25) * mm, "end": v(280.75, 20.25) * mm});
            skLineSegment(sketch, "E126.3.0.5", {"start": v(307.4, -20.25) * mm, "end": v(319.25, -20.25) * mm});
            skArc(sketch, "E126.3.0.6", {"start": v(320.3, -7.07) * mm, "mid": v(321.5, 0) * mm, "end": v(320.3, 7.07) * mm});
            skLineSegment(sketch, "E126.3.0.7", {"start": v(315.8, 24.26) * mm, "end": v(310.99, 42.25) * mm});
            skLineSegment(sketch, "E126.3.0.8", {"start": v(289.33, -43.43) * mm, "end": v(284.2, -24.26) * mm});
            skLineSegment(sketch, "E126.3.0.9", {"start": v(275.74, -15.8) * mm, "end": v(256.57, -10.67) * mm});
            skArc(sketch, "E126.3.0.10", {"start": v(255, -39) * mm, "mid": v(256.76, -43.24) * mm, "end": v(261, -45) * mm});
            skArc(sketch, "E126.3.0.11", {"start": v(279.7, 7.07) * mm, "mid": v(278.5, 0) * mm, "end": v(279.7, -7.07) * mm});
            skArc(sketch, "E126.3.0.12", {"start": v(292.93, -20.3) * mm, "mid": v(300, -21.5) * mm, "end": v(307.07, -20.3) * mm});
            skLineSegment(sketch, "E126.3.0.13", {"start": v(289.01, 42.25) * mm, "end": v(284.2, 24.26) * mm});
            skLineSegment(sketch, "E126.3.0.14", {"start": v(339.73, -14.5) * mm, "end": v(324.48, -18.6) * mm});
            skLineSegment(sketch, "E126.3.0.15", {"start": v(275.52, -18.6) * mm, "end": v(260.27, -14.5) * mm});
            skLineSegment(sketch, "E126.3.0.16", {"start": v(261, -42.25) * mm, "end": v(283.56, -42.25) * mm});
            skLineSegment(sketch, "E126.3.0.17", {"start": v(283.56, 42.25) * mm, "end": v(261, 42.25) * mm});
            skLineSegment(sketch, "E126.3.0.18", {"start": v(339, 42.25) * mm, "end": v(316.44, 42.25) * mm});
            skLineSegment(sketch, "E126.3.0.19", {"start": v(310.99, 42.25) * mm, "end": v(289.01, 42.25) * mm});
            skLineSegment(sketch, "E126.3.0.20", {"start": v(324.26, 15.8) * mm, "end": v(343.43, 10.67) * mm});
            skLineSegment(sketch, "E126.3.0.21", {"start": v(279.75, -7.4) * mm, "end": v(279.75, -19.25) * mm});
            skArc(sketch, "E126.3.0.22", {"start": v(339, -45) * mm, "mid": v(343.24, -43.24) * mm, "end": v(345, -39) * mm});
            skLineSegment(sketch, "E126.3.0.23", {"start": v(280.75, -20.25) * mm, "end": v(292.6, -20.25) * mm});
            skLineSegment(sketch, "E126.3.0.24", {"start": v(324.48, 18.6) * mm, "end": v(339.73, 14.5) * mm});
            skArc(sketch, "E126.3.0.25", {"start": v(276.91, 8.86) * mm, "mid": v(275, 0) * mm, "end": v(276.91, -8.86) * mm});
            skLineSegment(sketch, "E126.3.0.26", {"start": v(279.75, 19.25) * mm, "end": v(279.75, 7.4) * mm});
            skArc(sketch, "E126.3.0.27", {"start": v(323.09, -8.86) * mm, "mid": v(325, 0) * mm, "end": v(323.09, 8.86) * mm});
            skLineSegment(sketch, "E126.3.0.28", {"start": v(260.27, 14.5) * mm, "end": v(275.52, 18.6) * mm});
            skLineSegment(sketch, "E126.3.0.29", {"start": v(285.5, -39.73) * mm, "end": v(281.4, -24.48) * mm});
            skLineSegment(sketch, "E126.3.0.30", {"start": v(311.88, -45) * mm, "end": v(339, -45) * mm});
            skLineSegment(sketch, "E126.3.0.31", {"start": v(255, 39) * mm, "end": v(255, 11.88) * mm});
            skLineSegment(sketch, "E126.3.0.32", {"start": v(257.75, -16.44) * mm, "end": v(257.75, -39) * mm});
            skLineSegment(sketch, "E126.3.0.33", {"start": v(320.25, -19.25) * mm, "end": v(320.25, -7.4) * mm});
            skLineSegment(sketch, "E126.3.0.34", {"start": v(257.75, 39) * mm, "end": v(257.75, 16.44) * mm});
            skArc(sketch, "E126.3.0.35", {"start": v(307.07, 20.3) * mm, "mid": v(300, 21.5) * mm, "end": v(292.93, 20.3) * mm});
            skArc(sketch, "E126.3.0.36", {"start": v(345, 39) * mm, "mid": v(343.24, 43.24) * mm, "end": v(339, 45) * mm});
            skLineSegment(sketch, "E126.3.0.37", {"start": v(314.5, 39.73) * mm, "end": v(318.6, 24.48) * mm});
            skLineSegment(sketch, "E126.3.0.38", {"start": v(318.6, -24.48) * mm, "end": v(314.5, -39.73) * mm});
            skArc(sketch, "E126.3.0.39", {"start": v(308.86, 23.09) * mm, "mid": v(300, 25) * mm, "end": v(291.14, 23.09) * mm});
            skLineSegment(sketch, "E126.3.0.40", {"start": v(255, -11.88) * mm, "end": v(255, -39) * mm});
            skArc(sketch, "E126.3.0.41", {"start": v(291.14, -23.09) * mm, "mid": v(300, -25) * mm, "end": v(308.86, -23.09) * mm});
            skLineSegment(sketch, "E126.3.0.42", {"start": v(315.8, -24.26) * mm, "end": v(310.67, -43.43) * mm});
            skLineSegment(sketch, "E126.3.0.43", {"start": v(261, -45) * mm, "end": v(288.12, -45) * mm});
            skLineSegment(sketch, "E126.3.0.44", {"start": v(342.25, 16.44) * mm, "end": v(342.25, 39) * mm});
            skLineSegment(sketch, "E126.3.0.45", {"start": v(281.4, 24.48) * mm, "end": v(285.5, 39.73) * mm});
            skLineSegment(sketch, "E126.3.0.46", {"start": v(345, -39) * mm, "end": v(345, -11.88) * mm});
            skLineSegment(sketch, "E126.3.0.47", {"start": v(256.57, 10.67) * mm, "end": v(275.74, 15.8) * mm});
            skLineSegment(sketch, "E126.3.0.48", {"start": v(342.25, -39) * mm, "end": v(342.25, -16.44) * mm});
            skArc(sketch, "E126.3.0.49", {"start": v(261, 45) * mm, "mid": v(256.76, 43.24) * mm, "end": v(255, 39) * mm});
            skLineSegment(sketch, "E126.3.0.50", {"start": v(345, 11.88) * mm, "end": v(345, 39) * mm});
            skLineSegment(sketch, "E126.3.0.51", {"start": v(319.25, 20.25) * mm, "end": v(307.4, 20.25) * mm});
            skArc(sketch, "E126.3.0.52", {"start": v(260.27, -14.5) * mm, "mid": v(258.53, -14.85) * mm, "end": v(257.75, -16.44) * mm});
            skArc(sketch, "E126.3.0.53", {"start": v(280.75, 20.25) * mm, "mid": v(280.04, 19.96) * mm, "end": v(279.75, 19.25) * mm});
            skArc(sketch, "E126.3.0.54", {"start": v(257.75, 16.44) * mm, "mid": v(258.53, 14.85) * mm, "end": v(260.27, 14.5) * mm});
            skArc(sketch, "E126.3.0.55", {"start": v(316.44, 42.25) * mm, "mid": v(314.85, 41.47) * mm, "end": v(314.5, 39.73) * mm});
            skArc(sketch, "E126.3.0.56", {"start": v(261, 42.25) * mm, "mid": v(258.7, 41.3) * mm, "end": v(257.75, 39) * mm});
            skArc(sketch, "E126.3.0.57", {"start": v(307.4, -20.25) * mm, "mid": v(307.23, -20.26) * mm, "end": v(307.07, -20.3) * mm});
            skArc(sketch, "E126.3.0.58", {"start": v(323, 21) * mm, "mid": v(322.41, 22.41) * mm, "end": v(321, 23) * mm});
            skLineSegment(sketch, "E126.3.0.59", {"start": v(277, 14.84) * mm, "end": v(277, 9.27) * mm});
            skArc(sketch, "E126.3.0.60", {"start": v(283.56, -42.25) * mm, "mid": v(285.15, -41.47) * mm, "end": v(285.5, -39.73) * mm});
            skArc(sketch, "E126.3.0.61", {"start": v(345, -11.88) * mm, "mid": v(344.51, -10.89) * mm, "end": v(343.43, -10.67) * mm});
            skArc(sketch, "E126.3.0.62", {"start": v(277, 14.84) * mm, "mid": v(276.6, 15.64) * mm, "end": v(275.74, 15.8) * mm});
            skArc(sketch, "E126.3.0.63", {"start": v(323, 20.53) * mm, "mid": v(323.41, 19.3) * mm, "end": v(324.48, 18.6) * mm});
            skLineSegment(sketch, "E126.3.0.64", {"start": v(285.16, -23) * mm, "end": v(290.73, -23) * mm});
            skArc(sketch, "E126.3.0.65", {"start": v(342.25, -16.44) * mm, "mid": v(341.47, -14.85) * mm, "end": v(339.73, -14.5) * mm});
            skArc(sketch, "E126.3.0.66", {"start": v(284.2, 24.26) * mm, "mid": v(284.36, 23.4) * mm, "end": v(285.16, 23) * mm});
            skArc(sketch, "E126.3.0.67", {"start": v(256.57, -10.67) * mm, "mid": v(255.49, -10.89) * mm, "end": v(255, -11.88) * mm});
            skArc(sketch, "E126.3.0.68", {"start": v(276.91, 8.86) * mm, "mid": v(276.98, 9.06) * mm, "end": v(277, 9.27) * mm});
            skArc(sketch, "E126.3.0.69", {"start": v(285.16, -23) * mm, "mid": v(284.36, -23.4) * mm, "end": v(284.2, -24.26) * mm});
            skArc(sketch, "E126.3.0.70", {"start": v(320.25, 19.25) * mm, "mid": v(319.96, 19.96) * mm, "end": v(319.25, 20.25) * mm});
            skLineSegment(sketch, "E126.3.0.71", {"start": v(309.27, -23) * mm, "end": v(314.84, -23) * mm});
            skLineSegment(sketch, "E126.3.0.72", {"start": v(285.16, 23) * mm, "end": v(290.73, 23) * mm});
            skArc(sketch, "E126.3.0.73", {"start": v(309.27, -23) * mm, "mid": v(309.06, -23.02) * mm, "end": v(308.86, -23.09) * mm});
            skArc(sketch, "E126.3.0.74", {"start": v(255, 11.88) * mm, "mid": v(255.49, 10.89) * mm, "end": v(256.57, 10.67) * mm});
            skArc(sketch, "E126.3.0.75", {"start": v(339.73, 14.5) * mm, "mid": v(341.47, 14.85) * mm, "end": v(342.25, 16.44) * mm});
            skArc(sketch, "E126.3.0.76", {"start": v(288.12, -45) * mm, "mid": v(289.11, -44.51) * mm, "end": v(289.33, -43.43) * mm});
            skArc(sketch, "E126.3.0.77", {"start": v(310.67, -43.43) * mm, "mid": v(310.89, -44.51) * mm, "end": v(311.88, -45) * mm});
            skLineSegment(sketch, "E126.3.0.78", {"start": v(320.53, 23) * mm, "end": v(321, 23) * mm});
            skArc(sketch, "E126.3.0.79", {"start": v(318.6, 24.48) * mm, "mid": v(319.3, 23.41) * mm, "end": v(320.53, 23) * mm});
            skLineSegment(sketch, "E126.3.0.80", {"start": v(323, 21) * mm, "end": v(323, 20.53) * mm});
            skArc(sketch, "E126.3.0.81", {"start": v(314.5, -39.73) * mm, "mid": v(314.85, -41.47) * mm, "end": v(316.44, -42.25) * mm});
            skArc(sketch, "E126.3.0.82", {"start": v(343.43, 10.67) * mm, "mid": v(344.51, 10.89) * mm, "end": v(345, 11.88) * mm});
            skArc(sketch, "E126.3.0.83", {"start": v(285.5, 39.73) * mm, "mid": v(285.15, 41.47) * mm, "end": v(283.56, 42.25) * mm});
            skLineSegment(sketch, "E126.3.0.84", {"start": v(323, -14.84) * mm, "end": v(323, -9.27) * mm});
            skArc(sketch, "E126.3.0.85", {"start": v(319.25, -20.25) * mm, "mid": v(319.96, -19.96) * mm, "end": v(320.25, -19.25) * mm});
            skArc(sketch, "E126.3.0.86", {"start": v(307.07, 20.3) * mm, "mid": v(307.23, 20.26) * mm, "end": v(307.4, 20.25) * mm});
            skArc(sketch, "E126.3.0.87", {"start": v(324.26, 15.8) * mm, "mid": v(323.4, 15.64) * mm, "end": v(323, 14.84) * mm});
            skArc(sketch, "E126.3.0.88", {"start": v(308.86, 23.09) * mm, "mid": v(309.06, 23.02) * mm, "end": v(309.27, 23) * mm});
            skArc(sketch, "E126.3.0.89", {"start": v(315.8, -24.26) * mm, "mid": v(315.64, -23.4) * mm, "end": v(314.84, -23) * mm});
            skArc(sketch, "E126.3.0.90", {"start": v(314.84, 23) * mm, "mid": v(315.64, 23.4) * mm, "end": v(315.8, 24.26) * mm});
            skArc(sketch, "E126.3.0.91", {"start": v(323, -14.84) * mm, "mid": v(323.4, -15.64) * mm, "end": v(324.26, -15.8) * mm});
            skArc(sketch, "E126.3.0.92", {"start": v(257.75, -39) * mm, "mid": v(258.7, -41.3) * mm, "end": v(261, -42.25) * mm});
            skArc(sketch, "E126.3.0.93", {"start": v(275.52, 18.6) * mm, "mid": v(276.59, 19.3) * mm, "end": v(277, 20.53) * mm});
            skLineSegment(sketch, "E126.3.0.94", {"start": v(323, 9.27) * mm, "end": v(323, 14.84) * mm});
            skArc(sketch, "E126.3.0.95", {"start": v(275.74, -15.8) * mm, "mid": v(276.6, -15.64) * mm, "end": v(277, -14.84) * mm});
            skArc(sketch, "E126.3.0.96", {"start": v(339, -42.25) * mm, "mid": v(341.3, -41.3) * mm, "end": v(342.25, -39) * mm});
            skLineSegment(sketch, "E126.3.0.97", {"start": v(309.27, 23) * mm, "end": v(314.84, 23) * mm});
            skLineSegment(sketch, "E126.3.0.98", {"start": v(277, -9.27) * mm, "end": v(277, -14.84) * mm});
            skArc(sketch, "E126.3.0.99", {"start": v(320.53, -23) * mm, "mid": v(319.3, -23.41) * mm, "end": v(318.6, -24.48) * mm});
            skArc(sketch, "E126.3.0.100", {"start": v(342.25, 39) * mm, "mid": v(341.3, 41.3) * mm, "end": v(339, 42.25) * mm});
            skArc(sketch, "E126.3.0.101", {"start": v(324.48, -18.6) * mm, "mid": v(323.41, -19.3) * mm, "end": v(323, -20.53) * mm});
            skLineSegment(sketch, "E126.3.0.102", {"start": v(279, 23) * mm, "end": v(279.47, 23) * mm});
            skArc(sketch, "E126.3.0.103", {"start": v(320.25, 7.4) * mm, "mid": v(320.26, 7.23) * mm, "end": v(320.3, 7.07) * mm});
            skLineSegment(sketch, "E126.3.0.104", {"start": v(321, -23) * mm, "end": v(320.53, -23) * mm});
            skArc(sketch, "E126.3.0.105", {"start": v(279, 23) * mm, "mid": v(277.59, 22.41) * mm, "end": v(277, 21) * mm});
            skArc(sketch, "E126.3.0.106", {"start": v(292.6, 20.25) * mm, "mid": v(292.77, 20.26) * mm, "end": v(292.93, 20.3) * mm});
            skArc(sketch, "E126.3.0.107", {"start": v(320.3, -7.07) * mm, "mid": v(320.26, -7.23) * mm, "end": v(320.25, -7.4) * mm});
            skLineSegment(sketch, "E126.3.0.108", {"start": v(277, 20.53) * mm, "end": v(277, 21) * mm});
            skArc(sketch, "E126.3.0.109", {"start": v(277, -9.27) * mm, "mid": v(276.98, -9.06) * mm, "end": v(276.91, -8.86) * mm});
            skArc(sketch, "E126.3.0.110", {"start": v(292.93, -20.3) * mm, "mid": v(292.77, -20.26) * mm, "end": v(292.6, -20.25) * mm});
            skArc(sketch, "E126.3.0.111", {"start": v(279.75, -7.4) * mm, "mid": v(279.74, -7.23) * mm, "end": v(279.7, -7.07) * mm});
            skArc(sketch, "E126.3.0.112", {"start": v(323, 9.27) * mm, "mid": v(323.02, 9.06) * mm, "end": v(323.09, 8.86) * mm});
            skArc(sketch, "E126.3.0.113", {"start": v(291.14, -23.09) * mm, "mid": v(290.94, -23.02) * mm, "end": v(290.73, -23) * mm});
            skArc(sketch, "E126.3.0.114", {"start": v(321, -23) * mm, "mid": v(322.41, -22.41) * mm, "end": v(323, -21) * mm});
            skArc(sketch, "E126.3.0.115", {"start": v(290.73, 23) * mm, "mid": v(290.94, 23.02) * mm, "end": v(291.14, 23.09) * mm});
            skArc(sketch, "E126.3.0.116", {"start": v(277, -20.53) * mm, "mid": v(276.59, -19.3) * mm, "end": v(275.52, -18.6) * mm});
            skArc(sketch, "E126.3.0.117", {"start": v(279.75, -19.25) * mm, "mid": v(280.04, -19.96) * mm, "end": v(280.75, -20.25) * mm});
            skArc(sketch, "E126.3.0.118", {"start": v(279.7, 7.07) * mm, "mid": v(279.74, 7.23) * mm, "end": v(279.75, 7.4) * mm});
            skArc(sketch, "E126.3.0.119", {"start": v(279.47, 23) * mm, "mid": v(280.7, 23.41) * mm, "end": v(281.4, 24.48) * mm});
            skLineSegment(sketch, "E126.3.0.120", {"start": v(279.47, -23) * mm, "end": v(279, -23) * mm});
            skArc(sketch, "E126.3.0.121", {"start": v(277, -21) * mm, "mid": v(277.59, -22.41) * mm, "end": v(279, -23) * mm});
            skArc(sketch, "E126.3.0.122", {"start": v(323.09, -8.86) * mm, "mid": v(323.02, -9.06) * mm, "end": v(323, -9.27) * mm});
            skLineSegment(sketch, "E126.3.0.123", {"start": v(277, -21) * mm, "end": v(277, -20.53) * mm});
            skArc(sketch, "E126.3.0.124", {"start": v(281.4, -24.48) * mm, "mid": v(280.7, -23.41) * mm, "end": v(279.47, -23) * mm});
            skLineSegment(sketch, "E126.3.0.125", {"start": v(323, -20.53) * mm, "end": v(323, -21) * mm});
            skLineSegment(sketch, "E126.4.0.0", {"start": v(416.44, -42.25) * mm, "end": v(439, -42.25) * mm});
            skLineSegment(sketch, "E126.4.0.1", {"start": v(443.43, -10.67) * mm, "end": v(424.26, -15.8) * mm});
            skLineSegment(sketch, "E126.4.0.2", {"start": v(439, 45) * mm, "end": v(361, 45) * mm});
            skLineSegment(sketch, "E126.4.0.3", {"start": v(420.25, 7.4) * mm, "end": v(420.25, 19.25) * mm});
            skLineSegment(sketch, "E126.4.0.4", {"start": v(392.6, 20.25) * mm, "end": v(380.75, 20.25) * mm});
            skLineSegment(sketch, "E126.4.0.5", {"start": v(407.4, -20.25) * mm, "end": v(419.25, -20.25) * mm});
            skArc(sketch, "E126.4.0.6", {"start": v(420.3, -7.07) * mm, "mid": v(421.5, 0) * mm, "end": v(420.3, 7.07) * mm});
            skLineSegment(sketch, "E126.4.0.7", {"start": v(415.8, 24.26) * mm, "end": v(410.99, 42.25) * mm});
            skLineSegment(sketch, "E126.4.0.8", {"start": v(389.33, -43.43) * mm, "end": v(384.2, -24.26) * mm});
            skLineSegment(sketch, "E126.4.0.9", {"start": v(375.74, -15.8) * mm, "end": v(356.57, -10.67) * mm});
            skArc(sketch, "E126.4.0.10", {"start": v(355, -39) * mm, "mid": v(356.76, -43.24) * mm, "end": v(361, -45) * mm});
            skArc(sketch, "E126.4.0.11", {"start": v(379.7, 7.07) * mm, "mid": v(378.5, 0) * mm, "end": v(379.7, -7.07) * mm});
            skArc(sketch, "E126.4.0.12", {"start": v(392.93, -20.3) * mm, "mid": v(400, -21.5) * mm, "end": v(407.07, -20.3) * mm});
            skLineSegment(sketch, "E126.4.0.13", {"start": v(389.01, 42.25) * mm, "end": v(384.2, 24.26) * mm});
            skLineSegment(sketch, "E126.4.0.14", {"start": v(439.73, -14.5) * mm, "end": v(424.48, -18.6) * mm});
            skLineSegment(sketch, "E126.4.0.15", {"start": v(375.52, -18.6) * mm, "end": v(360.27, -14.5) * mm});
            skLineSegment(sketch, "E126.4.0.16", {"start": v(361, -42.25) * mm, "end": v(383.56, -42.25) * mm});
            skLineSegment(sketch, "E126.4.0.17", {"start": v(383.56, 42.25) * mm, "end": v(361, 42.25) * mm});
            skLineSegment(sketch, "E126.4.0.18", {"start": v(439, 42.25) * mm, "end": v(416.44, 42.25) * mm});
            skLineSegment(sketch, "E126.4.0.19", {"start": v(410.99, 42.25) * mm, "end": v(389.01, 42.25) * mm});
            skLineSegment(sketch, "E126.4.0.20", {"start": v(424.26, 15.8) * mm, "end": v(443.43, 10.67) * mm});
            skLineSegment(sketch, "E126.4.0.21", {"start": v(379.75, -7.4) * mm, "end": v(379.75, -19.25) * mm});
            skArc(sketch, "E126.4.0.22", {"start": v(439, -45) * mm, "mid": v(443.24, -43.24) * mm, "end": v(445, -39) * mm});
            skLineSegment(sketch, "E126.4.0.23", {"start": v(380.75, -20.25) * mm, "end": v(392.6, -20.25) * mm});
            skLineSegment(sketch, "E126.4.0.24", {"start": v(424.48, 18.6) * mm, "end": v(439.73, 14.5) * mm});
            skArc(sketch, "E126.4.0.25", {"start": v(376.91, 8.86) * mm, "mid": v(375, 0) * mm, "end": v(376.91, -8.86) * mm});
            skLineSegment(sketch, "E126.4.0.26", {"start": v(379.75, 19.25) * mm, "end": v(379.75, 7.4) * mm});
            skArc(sketch, "E126.4.0.27", {"start": v(423.09, -8.86) * mm, "mid": v(425, 0) * mm, "end": v(423.09, 8.86) * mm});
            skLineSegment(sketch, "E126.4.0.28", {"start": v(360.27, 14.5) * mm, "end": v(375.52, 18.6) * mm});
            skLineSegment(sketch, "E126.4.0.29", {"start": v(385.5, -39.73) * mm, "end": v(381.4, -24.48) * mm});
            skLineSegment(sketch, "E126.4.0.30", {"start": v(411.88, -45) * mm, "end": v(439, -45) * mm});
            skLineSegment(sketch, "E126.4.0.31", {"start": v(355, 39) * mm, "end": v(355, 11.88) * mm});
            skLineSegment(sketch, "E126.4.0.32", {"start": v(357.75, -16.44) * mm, "end": v(357.75, -39) * mm});
            skLineSegment(sketch, "E126.4.0.33", {"start": v(420.25, -19.25) * mm, "end": v(420.25, -7.4) * mm});
            skLineSegment(sketch, "E126.4.0.34", {"start": v(357.75, 39) * mm, "end": v(357.75, 16.44) * mm});
            skArc(sketch, "E126.4.0.35", {"start": v(407.07, 20.3) * mm, "mid": v(400, 21.5) * mm, "end": v(392.93, 20.3) * mm});
            skArc(sketch, "E126.4.0.36", {"start": v(445, 39) * mm, "mid": v(443.24, 43.24) * mm, "end": v(439, 45) * mm});
            skLineSegment(sketch, "E126.4.0.37", {"start": v(414.5, 39.73) * mm, "end": v(418.6, 24.48) * mm});
            skLineSegment(sketch, "E126.4.0.38", {"start": v(418.6, -24.48) * mm, "end": v(414.5, -39.73) * mm});
            skArc(sketch, "E126.4.0.39", {"start": v(408.86, 23.09) * mm, "mid": v(400, 25) * mm, "end": v(391.14, 23.09) * mm});
            skLineSegment(sketch, "E126.4.0.40", {"start": v(355, -11.88) * mm, "end": v(355, -39) * mm});
            skArc(sketch, "E126.4.0.41", {"start": v(391.14, -23.09) * mm, "mid": v(400, -25) * mm, "end": v(408.86, -23.09) * mm});
            skLineSegment(sketch, "E126.4.0.42", {"start": v(415.8, -24.26) * mm, "end": v(410.67, -43.43) * mm});
            skLineSegment(sketch, "E126.4.0.43", {"start": v(361, -45) * mm, "end": v(388.12, -45) * mm});
            skLineSegment(sketch, "E126.4.0.44", {"start": v(442.25, 16.44) * mm, "end": v(442.25, 39) * mm});
            skLineSegment(sketch, "E126.4.0.45", {"start": v(381.4, 24.48) * mm, "end": v(385.5, 39.73) * mm});
            skLineSegment(sketch, "E126.4.0.46", {"start": v(445, -39) * mm, "end": v(445, -11.88) * mm});
            skLineSegment(sketch, "E126.4.0.47", {"start": v(356.57, 10.67) * mm, "end": v(375.74, 15.8) * mm});
            skLineSegment(sketch, "E126.4.0.48", {"start": v(442.25, -39) * mm, "end": v(442.25, -16.44) * mm});
            skArc(sketch, "E126.4.0.49", {"start": v(361, 45) * mm, "mid": v(356.76, 43.24) * mm, "end": v(355, 39) * mm});
            skLineSegment(sketch, "E126.4.0.50", {"start": v(445, 11.88) * mm, "end": v(445, 39) * mm});
            skLineSegment(sketch, "E126.4.0.51", {"start": v(419.25, 20.25) * mm, "end": v(407.4, 20.25) * mm});
            skArc(sketch, "E126.4.0.52", {"start": v(360.27, -14.5) * mm, "mid": v(358.53, -14.85) * mm, "end": v(357.75, -16.44) * mm});
            skArc(sketch, "E126.4.0.53", {"start": v(380.75, 20.25) * mm, "mid": v(380.04, 19.96) * mm, "end": v(379.75, 19.25) * mm});
            skArc(sketch, "E126.4.0.54", {"start": v(357.75, 16.44) * mm, "mid": v(358.53, 14.85) * mm, "end": v(360.27, 14.5) * mm});
            skArc(sketch, "E126.4.0.55", {"start": v(416.44, 42.25) * mm, "mid": v(414.85, 41.47) * mm, "end": v(414.5, 39.73) * mm});
            skArc(sketch, "E126.4.0.56", {"start": v(361, 42.25) * mm, "mid": v(358.7, 41.3) * mm, "end": v(357.75, 39) * mm});
            skArc(sketch, "E126.4.0.57", {"start": v(407.4, -20.25) * mm, "mid": v(407.23, -20.26) * mm, "end": v(407.07, -20.3) * mm});
            skArc(sketch, "E126.4.0.58", {"start": v(423, 21) * mm, "mid": v(422.41, 22.41) * mm, "end": v(421, 23) * mm});
            skLineSegment(sketch, "E126.4.0.59", {"start": v(377, 14.84) * mm, "end": v(377, 9.27) * mm});
            skArc(sketch, "E126.4.0.60", {"start": v(383.56, -42.25) * mm, "mid": v(385.15, -41.47) * mm, "end": v(385.5, -39.73) * mm});
            skArc(sketch, "E126.4.0.61", {"start": v(445, -11.88) * mm, "mid": v(444.51, -10.89) * mm, "end": v(443.43, -10.67) * mm});
            skArc(sketch, "E126.4.0.62", {"start": v(377, 14.84) * mm, "mid": v(376.6, 15.64) * mm, "end": v(375.74, 15.8) * mm});
            skArc(sketch, "E126.4.0.63", {"start": v(423, 20.53) * mm, "mid": v(423.41, 19.3) * mm, "end": v(424.48, 18.6) * mm});
            skLineSegment(sketch, "E126.4.0.64", {"start": v(385.16, -23) * mm, "end": v(390.73, -23) * mm});
            skArc(sketch, "E126.4.0.65", {"start": v(442.25, -16.44) * mm, "mid": v(441.47, -14.85) * mm, "end": v(439.73, -14.5) * mm});
            skArc(sketch, "E126.4.0.66", {"start": v(384.2, 24.26) * mm, "mid": v(384.36, 23.4) * mm, "end": v(385.16, 23) * mm});
            skArc(sketch, "E126.4.0.67", {"start": v(356.57, -10.67) * mm, "mid": v(355.49, -10.89) * mm, "end": v(355, -11.88) * mm});
            skArc(sketch, "E126.4.0.68", {"start": v(376.91, 8.86) * mm, "mid": v(376.98, 9.06) * mm, "end": v(377, 9.27) * mm});
            skArc(sketch, "E126.4.0.69", {"start": v(385.16, -23) * mm, "mid": v(384.36, -23.4) * mm, "end": v(384.2, -24.26) * mm});
            skArc(sketch, "E126.4.0.70", {"start": v(420.25, 19.25) * mm, "mid": v(419.96, 19.96) * mm, "end": v(419.25, 20.25) * mm});
            skLineSegment(sketch, "E126.4.0.71", {"start": v(409.27, -23) * mm, "end": v(414.84, -23) * mm});
            skLineSegment(sketch, "E126.4.0.72", {"start": v(385.16, 23) * mm, "end": v(390.73, 23) * mm});
            skArc(sketch, "E126.4.0.73", {"start": v(409.27, -23) * mm, "mid": v(409.06, -23.02) * mm, "end": v(408.86, -23.09) * mm});
            skArc(sketch, "E126.4.0.74", {"start": v(355, 11.88) * mm, "mid": v(355.49, 10.89) * mm, "end": v(356.57, 10.67) * mm});
            skArc(sketch, "E126.4.0.75", {"start": v(439.73, 14.5) * mm, "mid": v(441.47, 14.85) * mm, "end": v(442.25, 16.44) * mm});
            skArc(sketch, "E126.4.0.76", {"start": v(388.12, -45) * mm, "mid": v(389.11, -44.51) * mm, "end": v(389.33, -43.43) * mm});
            skArc(sketch, "E126.4.0.77", {"start": v(410.67, -43.43) * mm, "mid": v(410.89, -44.51) * mm, "end": v(411.88, -45) * mm});
            skLineSegment(sketch, "E126.4.0.78", {"start": v(420.53, 23) * mm, "end": v(421, 23) * mm});
            skArc(sketch, "E126.4.0.79", {"start": v(418.6, 24.48) * mm, "mid": v(419.3, 23.41) * mm, "end": v(420.53, 23) * mm});
            skLineSegment(sketch, "E126.4.0.80", {"start": v(423, 21) * mm, "end": v(423, 20.53) * mm});
            skArc(sketch, "E126.4.0.81", {"start": v(414.5, -39.73) * mm, "mid": v(414.85, -41.47) * mm, "end": v(416.44, -42.25) * mm});
            skArc(sketch, "E126.4.0.82", {"start": v(443.43, 10.67) * mm, "mid": v(444.51, 10.89) * mm, "end": v(445, 11.88) * mm});
            skArc(sketch, "E126.4.0.83", {"start": v(385.5, 39.73) * mm, "mid": v(385.15, 41.47) * mm, "end": v(383.56, 42.25) * mm});
            skLineSegment(sketch, "E126.4.0.84", {"start": v(423, -14.84) * mm, "end": v(423, -9.27) * mm});
            skArc(sketch, "E126.4.0.85", {"start": v(419.25, -20.25) * mm, "mid": v(419.96, -19.96) * mm, "end": v(420.25, -19.25) * mm});
            skArc(sketch, "E126.4.0.86", {"start": v(407.07, 20.3) * mm, "mid": v(407.23, 20.26) * mm, "end": v(407.4, 20.25) * mm});
            skArc(sketch, "E126.4.0.87", {"start": v(424.26, 15.8) * mm, "mid": v(423.4, 15.64) * mm, "end": v(423, 14.84) * mm});
            skArc(sketch, "E126.4.0.88", {"start": v(408.86, 23.09) * mm, "mid": v(409.06, 23.02) * mm, "end": v(409.27, 23) * mm});
            skArc(sketch, "E126.4.0.89", {"start": v(415.8, -24.26) * mm, "mid": v(415.64, -23.4) * mm, "end": v(414.84, -23) * mm});
            skArc(sketch, "E126.4.0.90", {"start": v(414.84, 23) * mm, "mid": v(415.64, 23.4) * mm, "end": v(415.8, 24.26) * mm});
            skArc(sketch, "E126.4.0.91", {"start": v(423, -14.84) * mm, "mid": v(423.4, -15.64) * mm, "end": v(424.26, -15.8) * mm});
            skArc(sketch, "E126.4.0.92", {"start": v(357.75, -39) * mm, "mid": v(358.7, -41.3) * mm, "end": v(361, -42.25) * mm});
            skArc(sketch, "E126.4.0.93", {"start": v(375.52, 18.6) * mm, "mid": v(376.59, 19.3) * mm, "end": v(377, 20.53) * mm});
            skLineSegment(sketch, "E126.4.0.94", {"start": v(423, 9.27) * mm, "end": v(423, 14.84) * mm});
            skArc(sketch, "E126.4.0.95", {"start": v(375.74, -15.8) * mm, "mid": v(376.6, -15.64) * mm, "end": v(377, -14.84) * mm});
            skArc(sketch, "E126.4.0.96", {"start": v(439, -42.25) * mm, "mid": v(441.3, -41.3) * mm, "end": v(442.25, -39) * mm});
            skLineSegment(sketch, "E126.4.0.97", {"start": v(409.27, 23) * mm, "end": v(414.84, 23) * mm});
            skLineSegment(sketch, "E126.4.0.98", {"start": v(377, -9.27) * mm, "end": v(377, -14.84) * mm});
            skArc(sketch, "E126.4.0.99", {"start": v(420.53, -23) * mm, "mid": v(419.3, -23.41) * mm, "end": v(418.6, -24.48) * mm});
            skArc(sketch, "E126.4.0.100", {"start": v(442.25, 39) * mm, "mid": v(441.3, 41.3) * mm, "end": v(439, 42.25) * mm});
            skArc(sketch, "E126.4.0.101", {"start": v(424.48, -18.6) * mm, "mid": v(423.41, -19.3) * mm, "end": v(423, -20.53) * mm});
            skLineSegment(sketch, "E126.4.0.102", {"start": v(379, 23) * mm, "end": v(379.47, 23) * mm});
            skArc(sketch, "E126.4.0.103", {"start": v(420.25, 7.4) * mm, "mid": v(420.26, 7.23) * mm, "end": v(420.3, 7.07) * mm});
            skLineSegment(sketch, "E126.4.0.104", {"start": v(421, -23) * mm, "end": v(420.53, -23) * mm});
            skArc(sketch, "E126.4.0.105", {"start": v(379, 23) * mm, "mid": v(377.59, 22.41) * mm, "end": v(377, 21) * mm});
            skArc(sketch, "E126.4.0.106", {"start": v(392.6, 20.25) * mm, "mid": v(392.77, 20.26) * mm, "end": v(392.93, 20.3) * mm});
            skArc(sketch, "E126.4.0.107", {"start": v(420.3, -7.07) * mm, "mid": v(420.26, -7.23) * mm, "end": v(420.25, -7.4) * mm});
            skLineSegment(sketch, "E126.4.0.108", {"start": v(377, 20.53) * mm, "end": v(377, 21) * mm});
            skArc(sketch, "E126.4.0.109", {"start": v(377, -9.27) * mm, "mid": v(376.98, -9.06) * mm, "end": v(376.91, -8.86) * mm});
            skArc(sketch, "E126.4.0.110", {"start": v(392.93, -20.3) * mm, "mid": v(392.77, -20.26) * mm, "end": v(392.6, -20.25) * mm});
            skArc(sketch, "E126.4.0.111", {"start": v(379.75, -7.4) * mm, "mid": v(379.74, -7.23) * mm, "end": v(379.7, -7.07) * mm});
            skArc(sketch, "E126.4.0.112", {"start": v(423, 9.27) * mm, "mid": v(423.02, 9.06) * mm, "end": v(423.09, 8.86) * mm});
            skArc(sketch, "E126.4.0.113", {"start": v(391.14, -23.09) * mm, "mid": v(390.94, -23.02) * mm, "end": v(390.73, -23) * mm});
            skArc(sketch, "E126.4.0.114", {"start": v(421, -23) * mm, "mid": v(422.41, -22.41) * mm, "end": v(423, -21) * mm});
            skArc(sketch, "E126.4.0.115", {"start": v(390.73, 23) * mm, "mid": v(390.94, 23.02) * mm, "end": v(391.14, 23.09) * mm});
            skArc(sketch, "E126.4.0.116", {"start": v(377, -20.53) * mm, "mid": v(376.59, -19.3) * mm, "end": v(375.52, -18.6) * mm});
            skArc(sketch, "E126.4.0.117", {"start": v(379.75, -19.25) * mm, "mid": v(380.04, -19.96) * mm, "end": v(380.75, -20.25) * mm});
            skArc(sketch, "E126.4.0.118", {"start": v(379.7, 7.07) * mm, "mid": v(379.74, 7.23) * mm, "end": v(379.75, 7.4) * mm});
            skArc(sketch, "E126.4.0.119", {"start": v(379.47, 23) * mm, "mid": v(380.7, 23.41) * mm, "end": v(381.4, 24.48) * mm});
            skLineSegment(sketch, "E126.4.0.120", {"start": v(379.47, -23) * mm, "end": v(379, -23) * mm});
            skArc(sketch, "E126.4.0.121", {"start": v(377, -21) * mm, "mid": v(377.59, -22.41) * mm, "end": v(379, -23) * mm});
            skArc(sketch, "E126.4.0.122", {"start": v(423.09, -8.86) * mm, "mid": v(423.02, -9.06) * mm, "end": v(423, -9.27) * mm});
            skLineSegment(sketch, "E126.4.0.123", {"start": v(377, -21) * mm, "end": v(377, -20.53) * mm});
            skArc(sketch, "E126.4.0.124", {"start": v(381.4, -24.48) * mm, "mid": v(380.7, -23.41) * mm, "end": v(379.47, -23) * mm});
            skLineSegment(sketch, "E126.4.0.125", {"start": v(423, -20.53) * mm, "end": v(423, -21) * mm});
            skLineSegment(sketch, "E126.5.0.0", {"start": v(516.44, -42.25) * mm, "end": v(539, -42.25) * mm});
            skLineSegment(sketch, "E126.5.0.1", {"start": v(543.43, -10.67) * mm, "end": v(524.26, -15.8) * mm});
            skLineSegment(sketch, "E126.5.0.2", {"start": v(539, 45) * mm, "end": v(461, 45) * mm});
            skLineSegment(sketch, "E126.5.0.3", {"start": v(520.25, 7.4) * mm, "end": v(520.25, 19.25) * mm});
            skLineSegment(sketch, "E126.5.0.4", {"start": v(492.6, 20.25) * mm, "end": v(480.75, 20.25) * mm});
            skLineSegment(sketch, "E126.5.0.5", {"start": v(507.4, -20.25) * mm, "end": v(519.25, -20.25) * mm});
            skArc(sketch, "E126.5.0.6", {"start": v(520.3, -7.07) * mm, "mid": v(521.5, 0) * mm, "end": v(520.3, 7.07) * mm});
            skLineSegment(sketch, "E126.5.0.7", {"start": v(515.8, 24.26) * mm, "end": v(510.99, 42.25) * mm});
            skLineSegment(sketch, "E126.5.0.8", {"start": v(489.33, -43.43) * mm, "end": v(484.2, -24.26) * mm});
            skLineSegment(sketch, "E126.5.0.9", {"start": v(475.74, -15.8) * mm, "end": v(456.57, -10.67) * mm});
            skArc(sketch, "E126.5.0.10", {"start": v(455, -39) * mm, "mid": v(456.76, -43.24) * mm, "end": v(461, -45) * mm});
            skArc(sketch, "E126.5.0.11", {"start": v(479.7, 7.07) * mm, "mid": v(478.5, 0) * mm, "end": v(479.7, -7.07) * mm});
            skArc(sketch, "E126.5.0.12", {"start": v(492.93, -20.3) * mm, "mid": v(500, -21.5) * mm, "end": v(507.07, -20.3) * mm});
            skLineSegment(sketch, "E126.5.0.13", {"start": v(489.01, 42.25) * mm, "end": v(484.2, 24.26) * mm});
            skLineSegment(sketch, "E126.5.0.14", {"start": v(539.73, -14.5) * mm, "end": v(524.48, -18.6) * mm});
            skLineSegment(sketch, "E126.5.0.15", {"start": v(475.52, -18.6) * mm, "end": v(460.27, -14.5) * mm});
            skLineSegment(sketch, "E126.5.0.16", {"start": v(461, -42.25) * mm, "end": v(483.56, -42.25) * mm});
            skLineSegment(sketch, "E126.5.0.17", {"start": v(483.56, 42.25) * mm, "end": v(461, 42.25) * mm});
            skLineSegment(sketch, "E126.5.0.18", {"start": v(539, 42.25) * mm, "end": v(516.44, 42.25) * mm});
            skLineSegment(sketch, "E126.5.0.19", {"start": v(510.99, 42.25) * mm, "end": v(489.01, 42.25) * mm});
            skLineSegment(sketch, "E126.5.0.20", {"start": v(524.26, 15.8) * mm, "end": v(543.43, 10.67) * mm});
            skLineSegment(sketch, "E126.5.0.21", {"start": v(479.75, -7.4) * mm, "end": v(479.75, -19.25) * mm});
            skArc(sketch, "E126.5.0.22", {"start": v(539, -45) * mm, "mid": v(543.24, -43.24) * mm, "end": v(545, -39) * mm});
            skLineSegment(sketch, "E126.5.0.23", {"start": v(480.75, -20.25) * mm, "end": v(492.6, -20.25) * mm});
            skLineSegment(sketch, "E126.5.0.24", {"start": v(524.48, 18.6) * mm, "end": v(539.73, 14.5) * mm});
            skArc(sketch, "E126.5.0.25", {"start": v(476.91, 8.86) * mm, "mid": v(475, 0) * mm, "end": v(476.91, -8.86) * mm});
            skLineSegment(sketch, "E126.5.0.26", {"start": v(479.75, 19.25) * mm, "end": v(479.75, 7.4) * mm});
            skArc(sketch, "E126.5.0.27", {"start": v(523.09, -8.86) * mm, "mid": v(525, 0) * mm, "end": v(523.09, 8.86) * mm});
            skLineSegment(sketch, "E126.5.0.28", {"start": v(460.27, 14.5) * mm, "end": v(475.52, 18.6) * mm});
            skLineSegment(sketch, "E126.5.0.29", {"start": v(485.5, -39.73) * mm, "end": v(481.4, -24.48) * mm});
            skLineSegment(sketch, "E126.5.0.30", {"start": v(511.88, -45) * mm, "end": v(539, -45) * mm});
            skLineSegment(sketch, "E126.5.0.31", {"start": v(455, 39) * mm, "end": v(455, 11.88) * mm});
            skLineSegment(sketch, "E126.5.0.32", {"start": v(457.75, -16.44) * mm, "end": v(457.75, -39) * mm});
            skLineSegment(sketch, "E126.5.0.33", {"start": v(520.25, -19.25) * mm, "end": v(520.25, -7.4) * mm});
            skLineSegment(sketch, "E126.5.0.34", {"start": v(457.75, 39) * mm, "end": v(457.75, 16.44) * mm});
            skArc(sketch, "E126.5.0.35", {"start": v(507.07, 20.3) * mm, "mid": v(500, 21.5) * mm, "end": v(492.93, 20.3) * mm});
            skArc(sketch, "E126.5.0.36", {"start": v(545, 39) * mm, "mid": v(543.24, 43.24) * mm, "end": v(539, 45) * mm});
            skLineSegment(sketch, "E126.5.0.37", {"start": v(514.5, 39.73) * mm, "end": v(518.6, 24.48) * mm});
            skLineSegment(sketch, "E126.5.0.38", {"start": v(518.6, -24.48) * mm, "end": v(514.5, -39.73) * mm});
            skArc(sketch, "E126.5.0.39", {"start": v(508.86, 23.09) * mm, "mid": v(500, 25) * mm, "end": v(491.14, 23.09) * mm});
            skLineSegment(sketch, "E126.5.0.40", {"start": v(455, -11.88) * mm, "end": v(455, -39) * mm});
            skArc(sketch, "E126.5.0.41", {"start": v(491.14, -23.09) * mm, "mid": v(500, -25) * mm, "end": v(508.86, -23.09) * mm});
            skLineSegment(sketch, "E126.5.0.42", {"start": v(515.8, -24.26) * mm, "end": v(510.67, -43.43) * mm});
            skLineSegment(sketch, "E126.5.0.43", {"start": v(461, -45) * mm, "end": v(488.12, -45) * mm});
            skLineSegment(sketch, "E126.5.0.44", {"start": v(542.25, 16.44) * mm, "end": v(542.25, 39) * mm});
            skLineSegment(sketch, "E126.5.0.45", {"start": v(481.4, 24.48) * mm, "end": v(485.5, 39.73) * mm});
            skLineSegment(sketch, "E126.5.0.46", {"start": v(545, -39) * mm, "end": v(545, -11.88) * mm});
            skLineSegment(sketch, "E126.5.0.47", {"start": v(456.57, 10.67) * mm, "end": v(475.74, 15.8) * mm});
            skLineSegment(sketch, "E126.5.0.48", {"start": v(542.25, -39) * mm, "end": v(542.25, -16.44) * mm});
            skArc(sketch, "E126.5.0.49", {"start": v(461, 45) * mm, "mid": v(456.76, 43.24) * mm, "end": v(455, 39) * mm});
            skLineSegment(sketch, "E126.5.0.50", {"start": v(545, 11.88) * mm, "end": v(545, 39) * mm});
            skLineSegment(sketch, "E126.5.0.51", {"start": v(519.25, 20.25) * mm, "end": v(507.4, 20.25) * mm});
            skArc(sketch, "E126.5.0.52", {"start": v(460.27, -14.5) * mm, "mid": v(458.53, -14.85) * mm, "end": v(457.75, -16.44) * mm});
            skArc(sketch, "E126.5.0.53", {"start": v(480.75, 20.25) * mm, "mid": v(480.04, 19.96) * mm, "end": v(479.75, 19.25) * mm});
            skArc(sketch, "E126.5.0.54", {"start": v(457.75, 16.44) * mm, "mid": v(458.53, 14.85) * mm, "end": v(460.27, 14.5) * mm});
            skArc(sketch, "E126.5.0.55", {"start": v(516.44, 42.25) * mm, "mid": v(514.85, 41.47) * mm, "end": v(514.5, 39.73) * mm});
            skArc(sketch, "E126.5.0.56", {"start": v(461, 42.25) * mm, "mid": v(458.7, 41.3) * mm, "end": v(457.75, 39) * mm});
            skArc(sketch, "E126.5.0.57", {"start": v(507.4, -20.25) * mm, "mid": v(507.23, -20.26) * mm, "end": v(507.07, -20.3) * mm});
            skArc(sketch, "E126.5.0.58", {"start": v(523, 21) * mm, "mid": v(522.41, 22.41) * mm, "end": v(521, 23) * mm});
            skLineSegment(sketch, "E126.5.0.59", {"start": v(477, 14.84) * mm, "end": v(477, 9.27) * mm});
            skArc(sketch, "E126.5.0.60", {"start": v(483.56, -42.25) * mm, "mid": v(485.15, -41.47) * mm, "end": v(485.5, -39.73) * mm});
            skArc(sketch, "E126.5.0.61", {"start": v(545, -11.88) * mm, "mid": v(544.51, -10.89) * mm, "end": v(543.43, -10.67) * mm});
            skArc(sketch, "E126.5.0.62", {"start": v(477, 14.84) * mm, "mid": v(476.6, 15.64) * mm, "end": v(475.74, 15.8) * mm});
            skArc(sketch, "E126.5.0.63", {"start": v(523, 20.53) * mm, "mid": v(523.41, 19.3) * mm, "end": v(524.48, 18.6) * mm});
            skLineSegment(sketch, "E126.5.0.64", {"start": v(485.16, -23) * mm, "end": v(490.73, -23) * mm});
            skArc(sketch, "E126.5.0.65", {"start": v(542.25, -16.44) * mm, "mid": v(541.47, -14.85) * mm, "end": v(539.73, -14.5) * mm});
            skArc(sketch, "E126.5.0.66", {"start": v(484.2, 24.26) * mm, "mid": v(484.36, 23.4) * mm, "end": v(485.16, 23) * mm});
            skArc(sketch, "E126.5.0.67", {"start": v(456.57, -10.67) * mm, "mid": v(455.49, -10.89) * mm, "end": v(455, -11.88) * mm});
            skArc(sketch, "E126.5.0.68", {"start": v(476.91, 8.86) * mm, "mid": v(476.98, 9.06) * mm, "end": v(477, 9.27) * mm});
            skArc(sketch, "E126.5.0.69", {"start": v(485.16, -23) * mm, "mid": v(484.36, -23.4) * mm, "end": v(484.2, -24.26) * mm});
            skArc(sketch, "E126.5.0.70", {"start": v(520.25, 19.25) * mm, "mid": v(519.96, 19.96) * mm, "end": v(519.25, 20.25) * mm});
            skLineSegment(sketch, "E126.5.0.71", {"start": v(509.27, -23) * mm, "end": v(514.84, -23) * mm});
            skLineSegment(sketch, "E126.5.0.72", {"start": v(485.16, 23) * mm, "end": v(490.73, 23) * mm});
            skArc(sketch, "E126.5.0.73", {"start": v(509.27, -23) * mm, "mid": v(509.06, -23.02) * mm, "end": v(508.86, -23.09) * mm});
            skArc(sketch, "E126.5.0.74", {"start": v(455, 11.88) * mm, "mid": v(455.49, 10.89) * mm, "end": v(456.57, 10.67) * mm});
            skArc(sketch, "E126.5.0.75", {"start": v(539.73, 14.5) * mm, "mid": v(541.47, 14.85) * mm, "end": v(542.25, 16.44) * mm});
            skArc(sketch, "E126.5.0.76", {"start": v(488.12, -45) * mm, "mid": v(489.11, -44.51) * mm, "end": v(489.33, -43.43) * mm});
            skArc(sketch, "E126.5.0.77", {"start": v(510.67, -43.43) * mm, "mid": v(510.89, -44.51) * mm, "end": v(511.88, -45) * mm});
            skLineSegment(sketch, "E126.5.0.78", {"start": v(520.53, 23) * mm, "end": v(521, 23) * mm});
            skArc(sketch, "E126.5.0.79", {"start": v(518.6, 24.48) * mm, "mid": v(519.3, 23.41) * mm, "end": v(520.53, 23) * mm});
            skLineSegment(sketch, "E126.5.0.80", {"start": v(523, 21) * mm, "end": v(523, 20.53) * mm});
            skArc(sketch, "E126.5.0.81", {"start": v(514.5, -39.73) * mm, "mid": v(514.85, -41.47) * mm, "end": v(516.44, -42.25) * mm});
            skArc(sketch, "E126.5.0.82", {"start": v(543.43, 10.67) * mm, "mid": v(544.51, 10.89) * mm, "end": v(545, 11.88) * mm});
            skArc(sketch, "E126.5.0.83", {"start": v(485.5, 39.73) * mm, "mid": v(485.15, 41.47) * mm, "end": v(483.56, 42.25) * mm});
            skLineSegment(sketch, "E126.5.0.84", {"start": v(523, -14.84) * mm, "end": v(523, -9.27) * mm});
            skArc(sketch, "E126.5.0.85", {"start": v(519.25, -20.25) * mm, "mid": v(519.96, -19.96) * mm, "end": v(520.25, -19.25) * mm});
            skArc(sketch, "E126.5.0.86", {"start": v(507.07, 20.3) * mm, "mid": v(507.23, 20.26) * mm, "end": v(507.4, 20.25) * mm});
            skArc(sketch, "E126.5.0.87", {"start": v(524.26, 15.8) * mm, "mid": v(523.4, 15.64) * mm, "end": v(523, 14.84) * mm});
            skArc(sketch, "E126.5.0.88", {"start": v(508.86, 23.09) * mm, "mid": v(509.06, 23.02) * mm, "end": v(509.27, 23) * mm});
            skArc(sketch, "E126.5.0.89", {"start": v(515.8, -24.26) * mm, "mid": v(515.64, -23.4) * mm, "end": v(514.84, -23) * mm});
            skArc(sketch, "E126.5.0.90", {"start": v(514.84, 23) * mm, "mid": v(515.64, 23.4) * mm, "end": v(515.8, 24.26) * mm});
            skArc(sketch, "E126.5.0.91", {"start": v(523, -14.84) * mm, "mid": v(523.4, -15.64) * mm, "end": v(524.26, -15.8) * mm});
            skArc(sketch, "E126.5.0.92", {"start": v(457.75, -39) * mm, "mid": v(458.7, -41.3) * mm, "end": v(461, -42.25) * mm});
            skArc(sketch, "E126.5.0.93", {"start": v(475.52, 18.6) * mm, "mid": v(476.59, 19.3) * mm, "end": v(477, 20.53) * mm});
            skLineSegment(sketch, "E126.5.0.94", {"start": v(523, 9.27) * mm, "end": v(523, 14.84) * mm});
            skArc(sketch, "E126.5.0.95", {"start": v(475.74, -15.8) * mm, "mid": v(476.6, -15.64) * mm, "end": v(477, -14.84) * mm});
            skArc(sketch, "E126.5.0.96", {"start": v(539, -42.25) * mm, "mid": v(541.3, -41.3) * mm, "end": v(542.25, -39) * mm});
            skLineSegment(sketch, "E126.5.0.97", {"start": v(509.27, 23) * mm, "end": v(514.84, 23) * mm});
            skLineSegment(sketch, "E126.5.0.98", {"start": v(477, -9.27) * mm, "end": v(477, -14.84) * mm});
            skArc(sketch, "E126.5.0.99", {"start": v(520.53, -23) * mm, "mid": v(519.3, -23.41) * mm, "end": v(518.6, -24.48) * mm});
            skArc(sketch, "E126.5.0.100", {"start": v(542.25, 39) * mm, "mid": v(541.3, 41.3) * mm, "end": v(539, 42.25) * mm});
            skArc(sketch, "E126.5.0.101", {"start": v(524.48, -18.6) * mm, "mid": v(523.41, -19.3) * mm, "end": v(523, -20.53) * mm});
            skLineSegment(sketch, "E126.5.0.102", {"start": v(479, 23) * mm, "end": v(479.47, 23) * mm});
            skArc(sketch, "E126.5.0.103", {"start": v(520.25, 7.4) * mm, "mid": v(520.26, 7.23) * mm, "end": v(520.3, 7.07) * mm});
            skLineSegment(sketch, "E126.5.0.104", {"start": v(521, -23) * mm, "end": v(520.53, -23) * mm});
            skArc(sketch, "E126.5.0.105", {"start": v(479, 23) * mm, "mid": v(477.59, 22.41) * mm, "end": v(477, 21) * mm});
            skArc(sketch, "E126.5.0.106", {"start": v(492.6, 20.25) * mm, "mid": v(492.77, 20.26) * mm, "end": v(492.93, 20.3) * mm});
            skArc(sketch, "E126.5.0.107", {"start": v(520.3, -7.07) * mm, "mid": v(520.26, -7.23) * mm, "end": v(520.25, -7.4) * mm});
            skLineSegment(sketch, "E126.5.0.108", {"start": v(477, 20.53) * mm, "end": v(477, 21) * mm});
            skArc(sketch, "E126.5.0.109", {"start": v(477, -9.27) * mm, "mid": v(476.98, -9.06) * mm, "end": v(476.91, -8.86) * mm});
            skArc(sketch, "E126.5.0.110", {"start": v(492.93, -20.3) * mm, "mid": v(492.77, -20.26) * mm, "end": v(492.6, -20.25) * mm});
            skArc(sketch, "E126.5.0.111", {"start": v(479.75, -7.4) * mm, "mid": v(479.74, -7.23) * mm, "end": v(479.7, -7.07) * mm});
            skArc(sketch, "E126.5.0.112", {"start": v(523, 9.27) * mm, "mid": v(523.02, 9.06) * mm, "end": v(523.09, 8.86) * mm});
            skArc(sketch, "E126.5.0.113", {"start": v(491.14, -23.09) * mm, "mid": v(490.94, -23.02) * mm, "end": v(490.73, -23) * mm});
            skArc(sketch, "E126.5.0.114", {"start": v(521, -23) * mm, "mid": v(522.41, -22.41) * mm, "end": v(523, -21) * mm});
            skArc(sketch, "E126.5.0.115", {"start": v(490.73, 23) * mm, "mid": v(490.94, 23.02) * mm, "end": v(491.14, 23.09) * mm});
            skArc(sketch, "E126.5.0.116", {"start": v(477, -20.53) * mm, "mid": v(476.59, -19.3) * mm, "end": v(475.52, -18.6) * mm});
            skArc(sketch, "E126.5.0.117", {"start": v(479.75, -19.25) * mm, "mid": v(480.04, -19.96) * mm, "end": v(480.75, -20.25) * mm});
            skArc(sketch, "E126.5.0.118", {"start": v(479.7, 7.07) * mm, "mid": v(479.74, 7.23) * mm, "end": v(479.75, 7.4) * mm});
            skArc(sketch, "E126.5.0.119", {"start": v(479.47, 23) * mm, "mid": v(480.7, 23.41) * mm, "end": v(481.4, 24.48) * mm});
            skLineSegment(sketch, "E126.5.0.120", {"start": v(479.47, -23) * mm, "end": v(479, -23) * mm});
            skArc(sketch, "E126.5.0.121", {"start": v(477, -21) * mm, "mid": v(477.59, -22.41) * mm, "end": v(479, -23) * mm});
            skArc(sketch, "E126.5.0.122", {"start": v(523.09, -8.86) * mm, "mid": v(523.02, -9.06) * mm, "end": v(523, -9.27) * mm});
            skLineSegment(sketch, "E126.5.0.123", {"start": v(477, -21) * mm, "end": v(477, -20.53) * mm});
            skArc(sketch, "E126.5.0.124", {"start": v(481.4, -24.48) * mm, "mid": v(480.7, -23.41) * mm, "end": v(479.47, -23) * mm});
            skLineSegment(sketch, "E126.5.0.125", {"start": v(523, -20.53) * mm, "end": v(523, -21) * mm});
            skLineSegment(sketch, "E126.6.0.0", {"start": v(616.44, -42.25) * mm, "end": v(639, -42.25) * mm});
            skLineSegment(sketch, "E126.6.0.1", {"start": v(643.43, -10.67) * mm, "end": v(624.26, -15.8) * mm});
            skLineSegment(sketch, "E126.6.0.2", {"start": v(639, 45) * mm, "end": v(561, 45) * mm});
            skLineSegment(sketch, "E126.6.0.3", {"start": v(620.25, 7.4) * mm, "end": v(620.25, 19.25) * mm});
            skLineSegment(sketch, "E126.6.0.4", {"start": v(592.6, 20.25) * mm, "end": v(580.75, 20.25) * mm});
            skLineSegment(sketch, "E126.6.0.5", {"start": v(607.4, -20.25) * mm, "end": v(619.25, -20.25) * mm});
            skArc(sketch, "E126.6.0.6", {"start": v(620.3, -7.07) * mm, "mid": v(621.5, 0) * mm, "end": v(620.3, 7.07) * mm});
            skLineSegment(sketch, "E126.6.0.7", {"start": v(615.8, 24.26) * mm, "end": v(610.99, 42.25) * mm});
            skLineSegment(sketch, "E126.6.0.8", {"start": v(589.33, -43.43) * mm, "end": v(584.2, -24.26) * mm});
            skLineSegment(sketch, "E126.6.0.9", {"start": v(575.74, -15.8) * mm, "end": v(556.57, -10.67) * mm});
            skArc(sketch, "E126.6.0.10", {"start": v(555, -39) * mm, "mid": v(556.76, -43.24) * mm, "end": v(561, -45) * mm});
            skArc(sketch, "E126.6.0.11", {"start": v(579.7, 7.07) * mm, "mid": v(578.5, 0) * mm, "end": v(579.7, -7.07) * mm});
            skArc(sketch, "E126.6.0.12", {"start": v(592.93, -20.3) * mm, "mid": v(600, -21.5) * mm, "end": v(607.07, -20.3) * mm});
            skLineSegment(sketch, "E126.6.0.13", {"start": v(589.01, 42.25) * mm, "end": v(584.2, 24.26) * mm});
            skLineSegment(sketch, "E126.6.0.14", {"start": v(639.73, -14.5) * mm, "end": v(624.48, -18.6) * mm});
            skLineSegment(sketch, "E126.6.0.15", {"start": v(575.52, -18.6) * mm, "end": v(560.27, -14.5) * mm});
            skLineSegment(sketch, "E126.6.0.16", {"start": v(561, -42.25) * mm, "end": v(583.56, -42.25) * mm});
            skLineSegment(sketch, "E126.6.0.17", {"start": v(583.56, 42.25) * mm, "end": v(561, 42.25) * mm});
            skLineSegment(sketch, "E126.6.0.18", {"start": v(639, 42.25) * mm, "end": v(616.44, 42.25) * mm});
            skLineSegment(sketch, "E126.6.0.19", {"start": v(610.99, 42.25) * mm, "end": v(589.01, 42.25) * mm});
            skLineSegment(sketch, "E126.6.0.20", {"start": v(624.26, 15.8) * mm, "end": v(643.43, 10.67) * mm});
            skLineSegment(sketch, "E126.6.0.21", {"start": v(579.75, -7.4) * mm, "end": v(579.75, -19.25) * mm});
            skArc(sketch, "E126.6.0.22", {"start": v(639, -45) * mm, "mid": v(643.24, -43.24) * mm, "end": v(645, -39) * mm});
            skLineSegment(sketch, "E126.6.0.23", {"start": v(580.75, -20.25) * mm, "end": v(592.6, -20.25) * mm});
            skLineSegment(sketch, "E126.6.0.24", {"start": v(624.48, 18.6) * mm, "end": v(639.73, 14.5) * mm});
            skArc(sketch, "E126.6.0.25", {"start": v(576.91, 8.86) * mm, "mid": v(575, 0) * mm, "end": v(576.91, -8.86) * mm});
            skLineSegment(sketch, "E126.6.0.26", {"start": v(579.75, 19.25) * mm, "end": v(579.75, 7.4) * mm});
            skArc(sketch, "E126.6.0.27", {"start": v(623.09, -8.86) * mm, "mid": v(625, 0) * mm, "end": v(623.09, 8.86) * mm});
            skLineSegment(sketch, "E126.6.0.28", {"start": v(560.27, 14.5) * mm, "end": v(575.52, 18.6) * mm});
            skLineSegment(sketch, "E126.6.0.29", {"start": v(585.5, -39.73) * mm, "end": v(581.4, -24.48) * mm});
            skLineSegment(sketch, "E126.6.0.30", {"start": v(611.88, -45) * mm, "end": v(639, -45) * mm});
            skLineSegment(sketch, "E126.6.0.31", {"start": v(555, 39) * mm, "end": v(555, 11.88) * mm});
            skLineSegment(sketch, "E126.6.0.32", {"start": v(557.75, -16.44) * mm, "end": v(557.75, -39) * mm});
            skLineSegment(sketch, "E126.6.0.33", {"start": v(620.25, -19.25) * mm, "end": v(620.25, -7.4) * mm});
            skLineSegment(sketch, "E126.6.0.34", {"start": v(557.75, 39) * mm, "end": v(557.75, 16.44) * mm});
            skArc(sketch, "E126.6.0.35", {"start": v(607.07, 20.3) * mm, "mid": v(600, 21.5) * mm, "end": v(592.93, 20.3) * mm});
            skArc(sketch, "E126.6.0.36", {"start": v(645, 39) * mm, "mid": v(643.24, 43.24) * mm, "end": v(639, 45) * mm});
            skLineSegment(sketch, "E126.6.0.37", {"start": v(614.5, 39.73) * mm, "end": v(618.6, 24.48) * mm});
            skLineSegment(sketch, "E126.6.0.38", {"start": v(618.6, -24.48) * mm, "end": v(614.5, -39.73) * mm});
            skArc(sketch, "E126.6.0.39", {"start": v(608.86, 23.09) * mm, "mid": v(600, 25) * mm, "end": v(591.14, 23.09) * mm});
            skLineSegment(sketch, "E126.6.0.40", {"start": v(555, -11.88) * mm, "end": v(555, -39) * mm});
            skArc(sketch, "E126.6.0.41", {"start": v(591.14, -23.09) * mm, "mid": v(600, -25) * mm, "end": v(608.86, -23.09) * mm});
            skLineSegment(sketch, "E126.6.0.42", {"start": v(615.8, -24.26) * mm, "end": v(610.67, -43.43) * mm});
            skLineSegment(sketch, "E126.6.0.43", {"start": v(561, -45) * mm, "end": v(588.12, -45) * mm});
            skLineSegment(sketch, "E126.6.0.44", {"start": v(642.25, 16.44) * mm, "end": v(642.25, 39) * mm});
            skLineSegment(sketch, "E126.6.0.45", {"start": v(581.4, 24.48) * mm, "end": v(585.5, 39.73) * mm});
            skLineSegment(sketch, "E126.6.0.46", {"start": v(645, -39) * mm, "end": v(645, -11.88) * mm});
            skLineSegment(sketch, "E126.6.0.47", {"start": v(556.57, 10.67) * mm, "end": v(575.74, 15.8) * mm});
            skLineSegment(sketch, "E126.6.0.48", {"start": v(642.25, -39) * mm, "end": v(642.25, -16.44) * mm});
            skArc(sketch, "E126.6.0.49", {"start": v(561, 45) * mm, "mid": v(556.76, 43.24) * mm, "end": v(555, 39) * mm});
            skLineSegment(sketch, "E126.6.0.50", {"start": v(645, 11.88) * mm, "end": v(645, 39) * mm});
            skLineSegment(sketch, "E126.6.0.51", {"start": v(619.25, 20.25) * mm, "end": v(607.4, 20.25) * mm});
            skArc(sketch, "E126.6.0.52", {"start": v(560.27, -14.5) * mm, "mid": v(558.53, -14.85) * mm, "end": v(557.75, -16.44) * mm});
            skArc(sketch, "E126.6.0.53", {"start": v(580.75, 20.25) * mm, "mid": v(580.04, 19.96) * mm, "end": v(579.75, 19.25) * mm});
            skArc(sketch, "E126.6.0.54", {"start": v(557.75, 16.44) * mm, "mid": v(558.53, 14.85) * mm, "end": v(560.27, 14.5) * mm});
            skArc(sketch, "E126.6.0.55", {"start": v(616.44, 42.25) * mm, "mid": v(614.85, 41.47) * mm, "end": v(614.5, 39.73) * mm});
            skArc(sketch, "E126.6.0.56", {"start": v(561, 42.25) * mm, "mid": v(558.7, 41.3) * mm, "end": v(557.75, 39) * mm});
            skArc(sketch, "E126.6.0.57", {"start": v(607.4, -20.25) * mm, "mid": v(607.23, -20.26) * mm, "end": v(607.07, -20.3) * mm});
            skArc(sketch, "E126.6.0.58", {"start": v(623, 21) * mm, "mid": v(622.41, 22.41) * mm, "end": v(621, 23) * mm});
            skLineSegment(sketch, "E126.6.0.59", {"start": v(577, 14.84) * mm, "end": v(577, 9.27) * mm});
            skArc(sketch, "E126.6.0.60", {"start": v(583.56, -42.25) * mm, "mid": v(585.15, -41.47) * mm, "end": v(585.5, -39.73) * mm});
            skArc(sketch, "E126.6.0.61", {"start": v(645, -11.88) * mm, "mid": v(644.51, -10.89) * mm, "end": v(643.43, -10.67) * mm});
            skArc(sketch, "E126.6.0.62", {"start": v(577, 14.84) * mm, "mid": v(576.6, 15.64) * mm, "end": v(575.74, 15.8) * mm});
            skArc(sketch, "E126.6.0.63", {"start": v(623, 20.53) * mm, "mid": v(623.41, 19.3) * mm, "end": v(624.48, 18.6) * mm});
            skLineSegment(sketch, "E126.6.0.64", {"start": v(585.16, -23) * mm, "end": v(590.73, -23) * mm});
            skArc(sketch, "E126.6.0.65", {"start": v(642.25, -16.44) * mm, "mid": v(641.47, -14.85) * mm, "end": v(639.73, -14.5) * mm});
            skArc(sketch, "E126.6.0.66", {"start": v(584.2, 24.26) * mm, "mid": v(584.36, 23.4) * mm, "end": v(585.16, 23) * mm});
            skArc(sketch, "E126.6.0.67", {"start": v(556.57, -10.67) * mm, "mid": v(555.49, -10.89) * mm, "end": v(555, -11.88) * mm});
            skArc(sketch, "E126.6.0.68", {"start": v(576.91, 8.86) * mm, "mid": v(576.98, 9.06) * mm, "end": v(577, 9.27) * mm});
            skArc(sketch, "E126.6.0.69", {"start": v(585.16, -23) * mm, "mid": v(584.36, -23.4) * mm, "end": v(584.2, -24.26) * mm});
            skArc(sketch, "E126.6.0.70", {"start": v(620.25, 19.25) * mm, "mid": v(619.96, 19.96) * mm, "end": v(619.25, 20.25) * mm});
            skLineSegment(sketch, "E126.6.0.71", {"start": v(609.27, -23) * mm, "end": v(614.84, -23) * mm});
            skLineSegment(sketch, "E126.6.0.72", {"start": v(585.16, 23) * mm, "end": v(590.73, 23) * mm});
            skArc(sketch, "E126.6.0.73", {"start": v(609.27, -23) * mm, "mid": v(609.06, -23.02) * mm, "end": v(608.86, -23.09) * mm});
            skArc(sketch, "E126.6.0.74", {"start": v(555, 11.88) * mm, "mid": v(555.49, 10.89) * mm, "end": v(556.57, 10.67) * mm});
            skArc(sketch, "E126.6.0.75", {"start": v(639.73, 14.5) * mm, "mid": v(641.47, 14.85) * mm, "end": v(642.25, 16.44) * mm});
            skArc(sketch, "E126.6.0.76", {"start": v(588.12, -45) * mm, "mid": v(589.11, -44.51) * mm, "end": v(589.33, -43.43) * mm});
            skArc(sketch, "E126.6.0.77", {"start": v(610.67, -43.43) * mm, "mid": v(610.89, -44.51) * mm, "end": v(611.88, -45) * mm});
            skLineSegment(sketch, "E126.6.0.78", {"start": v(620.53, 23) * mm, "end": v(621, 23) * mm});
            skArc(sketch, "E126.6.0.79", {"start": v(618.6, 24.48) * mm, "mid": v(619.3, 23.41) * mm, "end": v(620.53, 23) * mm});
            skLineSegment(sketch, "E126.6.0.80", {"start": v(623, 21) * mm, "end": v(623, 20.53) * mm});
            skArc(sketch, "E126.6.0.81", {"start": v(614.5, -39.73) * mm, "mid": v(614.85, -41.47) * mm, "end": v(616.44, -42.25) * mm});
            skArc(sketch, "E126.6.0.82", {"start": v(643.43, 10.67) * mm, "mid": v(644.51, 10.89) * mm, "end": v(645, 11.88) * mm});
            skArc(sketch, "E126.6.0.83", {"start": v(585.5, 39.73) * mm, "mid": v(585.15, 41.47) * mm, "end": v(583.56, 42.25) * mm});
            skLineSegment(sketch, "E126.6.0.84", {"start": v(623, -14.84) * mm, "end": v(623, -9.27) * mm});
            skArc(sketch, "E126.6.0.85", {"start": v(619.25, -20.25) * mm, "mid": v(619.96, -19.96) * mm, "end": v(620.25, -19.25) * mm});
            skArc(sketch, "E126.6.0.86", {"start": v(607.07, 20.3) * mm, "mid": v(607.23, 20.26) * mm, "end": v(607.4, 20.25) * mm});
            skArc(sketch, "E126.6.0.87", {"start": v(624.26, 15.8) * mm, "mid": v(623.4, 15.64) * mm, "end": v(623, 14.84) * mm});
            skArc(sketch, "E126.6.0.88", {"start": v(608.86, 23.09) * mm, "mid": v(609.06, 23.02) * mm, "end": v(609.27, 23) * mm});
            skArc(sketch, "E126.6.0.89", {"start": v(615.8, -24.26) * mm, "mid": v(615.64, -23.4) * mm, "end": v(614.84, -23) * mm});
            skArc(sketch, "E126.6.0.90", {"start": v(614.84, 23) * mm, "mid": v(615.64, 23.4) * mm, "end": v(615.8, 24.26) * mm});
            skArc(sketch, "E126.6.0.91", {"start": v(623, -14.84) * mm, "mid": v(623.4, -15.64) * mm, "end": v(624.26, -15.8) * mm});
            skArc(sketch, "E126.6.0.92", {"start": v(557.75, -39) * mm, "mid": v(558.7, -41.3) * mm, "end": v(561, -42.25) * mm});
            skArc(sketch, "E126.6.0.93", {"start": v(575.52, 18.6) * mm, "mid": v(576.59, 19.3) * mm, "end": v(577, 20.53) * mm});
            skLineSegment(sketch, "E126.6.0.94", {"start": v(623, 9.27) * mm, "end": v(623, 14.84) * mm});
            skArc(sketch, "E126.6.0.95", {"start": v(575.74, -15.8) * mm, "mid": v(576.6, -15.64) * mm, "end": v(577, -14.84) * mm});
            skArc(sketch, "E126.6.0.96", {"start": v(639, -42.25) * mm, "mid": v(641.3, -41.3) * mm, "end": v(642.25, -39) * mm});
            skLineSegment(sketch, "E126.6.0.97", {"start": v(609.27, 23) * mm, "end": v(614.84, 23) * mm});
            skLineSegment(sketch, "E126.6.0.98", {"start": v(577, -9.27) * mm, "end": v(577, -14.84) * mm});
            skArc(sketch, "E126.6.0.99", {"start": v(620.53, -23) * mm, "mid": v(619.3, -23.41) * mm, "end": v(618.6, -24.48) * mm});
            skArc(sketch, "E126.6.0.100", {"start": v(642.25, 39) * mm, "mid": v(641.3, 41.3) * mm, "end": v(639, 42.25) * mm});
            skArc(sketch, "E126.6.0.101", {"start": v(624.48, -18.6) * mm, "mid": v(623.41, -19.3) * mm, "end": v(623, -20.53) * mm});
            skLineSegment(sketch, "E126.6.0.102", {"start": v(579, 23) * mm, "end": v(579.47, 23) * mm});
            skArc(sketch, "E126.6.0.103", {"start": v(620.25, 7.4) * mm, "mid": v(620.26, 7.23) * mm, "end": v(620.3, 7.07) * mm});
            skLineSegment(sketch, "E126.6.0.104", {"start": v(621, -23) * mm, "end": v(620.53, -23) * mm});
            skArc(sketch, "E126.6.0.105", {"start": v(579, 23) * mm, "mid": v(577.59, 22.41) * mm, "end": v(577, 21) * mm});
            skArc(sketch, "E126.6.0.106", {"start": v(592.6, 20.25) * mm, "mid": v(592.77, 20.26) * mm, "end": v(592.93, 20.3) * mm});
            skArc(sketch, "E126.6.0.107", {"start": v(620.3, -7.07) * mm, "mid": v(620.26, -7.23) * mm, "end": v(620.25, -7.4) * mm});
            skLineSegment(sketch, "E126.6.0.108", {"start": v(577, 20.53) * mm, "end": v(577, 21) * mm});
            skArc(sketch, "E126.6.0.109", {"start": v(577, -9.27) * mm, "mid": v(576.98, -9.06) * mm, "end": v(576.91, -8.86) * mm});
            skArc(sketch, "E126.6.0.110", {"start": v(592.93, -20.3) * mm, "mid": v(592.77, -20.26) * mm, "end": v(592.6, -20.25) * mm});
            skArc(sketch, "E126.6.0.111", {"start": v(579.75, -7.4) * mm, "mid": v(579.74, -7.23) * mm, "end": v(579.7, -7.07) * mm});
            skArc(sketch, "E126.6.0.112", {"start": v(623, 9.27) * mm, "mid": v(623.02, 9.06) * mm, "end": v(623.09, 8.86) * mm});
            skArc(sketch, "E126.6.0.113", {"start": v(591.14, -23.09) * mm, "mid": v(590.94, -23.02) * mm, "end": v(590.73, -23) * mm});
            skArc(sketch, "E126.6.0.114", {"start": v(621, -23) * mm, "mid": v(622.41, -22.41) * mm, "end": v(623, -21) * mm});
            skArc(sketch, "E126.6.0.115", {"start": v(590.73, 23) * mm, "mid": v(590.94, 23.02) * mm, "end": v(591.14, 23.09) * mm});
            skArc(sketch, "E126.6.0.116", {"start": v(577, -20.53) * mm, "mid": v(576.59, -19.3) * mm, "end": v(575.52, -18.6) * mm});
            skArc(sketch, "E126.6.0.117", {"start": v(579.75, -19.25) * mm, "mid": v(580.04, -19.96) * mm, "end": v(580.75, -20.25) * mm});
            skArc(sketch, "E126.6.0.118", {"start": v(579.7, 7.07) * mm, "mid": v(579.74, 7.23) * mm, "end": v(579.75, 7.4) * mm});
            skArc(sketch, "E126.6.0.119", {"start": v(579.47, 23) * mm, "mid": v(580.7, 23.41) * mm, "end": v(581.4, 24.48) * mm});
            skLineSegment(sketch, "E126.6.0.120", {"start": v(579.47, -23) * mm, "end": v(579, -23) * mm});
            skArc(sketch, "E126.6.0.121", {"start": v(577, -21) * mm, "mid": v(577.59, -22.41) * mm, "end": v(579, -23) * mm});
            skArc(sketch, "E126.6.0.122", {"start": v(623.09, -8.86) * mm, "mid": v(623.02, -9.06) * mm, "end": v(623, -9.27) * mm});
            skLineSegment(sketch, "E126.6.0.123", {"start": v(577, -21) * mm, "end": v(577, -20.53) * mm});
            skArc(sketch, "E126.6.0.124", {"start": v(581.4, -24.48) * mm, "mid": v(580.7, -23.41) * mm, "end": v(579.47, -23) * mm});
            skLineSegment(sketch, "E126.6.0.125", {"start": v(623, -20.53) * mm, "end": v(623, -21) * mm});
            skLineSegment(sketch, "E126.7.0.0", {"start": v(716.44, -42.25) * mm, "end": v(739, -42.25) * mm});
            skLineSegment(sketch, "E126.7.0.1", {"start": v(743.43, -10.67) * mm, "end": v(724.26, -15.8) * mm});
            skLineSegment(sketch, "E126.7.0.2", {"start": v(739, 45) * mm, "end": v(661, 45) * mm});
            skLineSegment(sketch, "E126.7.0.3", {"start": v(720.25, 7.4) * mm, "end": v(720.25, 19.25) * mm});
            skLineSegment(sketch, "E126.7.0.4", {"start": v(692.6, 20.25) * mm, "end": v(680.75, 20.25) * mm});
            skLineSegment(sketch, "E126.7.0.5", {"start": v(707.4, -20.25) * mm, "end": v(719.25, -20.25) * mm});
            skArc(sketch, "E126.7.0.6", {"start": v(720.3, -7.07) * mm, "mid": v(721.5, 0) * mm, "end": v(720.3, 7.07) * mm});
            skLineSegment(sketch, "E126.7.0.7", {"start": v(715.8, 24.26) * mm, "end": v(710.99, 42.25) * mm});
            skLineSegment(sketch, "E126.7.0.8", {"start": v(689.33, -43.43) * mm, "end": v(684.2, -24.26) * mm});
            skLineSegment(sketch, "E126.7.0.9", {"start": v(675.74, -15.8) * mm, "end": v(656.57, -10.67) * mm});
            skArc(sketch, "E126.7.0.10", {"start": v(655, -39) * mm, "mid": v(656.76, -43.24) * mm, "end": v(661, -45) * mm});
            skArc(sketch, "E126.7.0.11", {"start": v(679.7, 7.07) * mm, "mid": v(678.5, 0) * mm, "end": v(679.7, -7.07) * mm});
            skArc(sketch, "E126.7.0.12", {"start": v(692.93, -20.3) * mm, "mid": v(700, -21.5) * mm, "end": v(707.07, -20.3) * mm});
            skLineSegment(sketch, "E126.7.0.13", {"start": v(689.01, 42.25) * mm, "end": v(684.2, 24.26) * mm});
            skLineSegment(sketch, "E126.7.0.14", {"start": v(739.73, -14.5) * mm, "end": v(724.48, -18.6) * mm});
            skLineSegment(sketch, "E126.7.0.15", {"start": v(675.52, -18.6) * mm, "end": v(660.27, -14.5) * mm});
            skLineSegment(sketch, "E126.7.0.16", {"start": v(661, -42.25) * mm, "end": v(683.56, -42.25) * mm});
            skLineSegment(sketch, "E126.7.0.17", {"start": v(683.56, 42.25) * mm, "end": v(661, 42.25) * mm});
            skLineSegment(sketch, "E126.7.0.18", {"start": v(739, 42.25) * mm, "end": v(716.44, 42.25) * mm});
            skLineSegment(sketch, "E126.7.0.19", {"start": v(710.99, 42.25) * mm, "end": v(689.01, 42.25) * mm});
            skLineSegment(sketch, "E126.7.0.20", {"start": v(724.26, 15.8) * mm, "end": v(743.43, 10.67) * mm});
            skLineSegment(sketch, "E126.7.0.21", {"start": v(679.75, -7.4) * mm, "end": v(679.75, -19.25) * mm});
            skArc(sketch, "E126.7.0.22", {"start": v(739, -45) * mm, "mid": v(743.24, -43.24) * mm, "end": v(745, -39) * mm});
            skLineSegment(sketch, "E126.7.0.23", {"start": v(680.75, -20.25) * mm, "end": v(692.6, -20.25) * mm});
            skLineSegment(sketch, "E126.7.0.24", {"start": v(724.48, 18.6) * mm, "end": v(739.73, 14.5) * mm});
            skArc(sketch, "E126.7.0.25", {"start": v(676.91, 8.86) * mm, "mid": v(675, 0) * mm, "end": v(676.91, -8.86) * mm});
            skLineSegment(sketch, "E126.7.0.26", {"start": v(679.75, 19.25) * mm, "end": v(679.75, 7.4) * mm});
            skArc(sketch, "E126.7.0.27", {"start": v(723.09, -8.86) * mm, "mid": v(725, 0) * mm, "end": v(723.09, 8.86) * mm});
            skLineSegment(sketch, "E126.7.0.28", {"start": v(660.27, 14.5) * mm, "end": v(675.52, 18.6) * mm});
            skLineSegment(sketch, "E126.7.0.29", {"start": v(685.5, -39.73) * mm, "end": v(681.4, -24.48) * mm});
            skLineSegment(sketch, "E126.7.0.30", {"start": v(711.88, -45) * mm, "end": v(739, -45) * mm});
            skLineSegment(sketch, "E126.7.0.31", {"start": v(655, 39) * mm, "end": v(655, 11.88) * mm});
            skLineSegment(sketch, "E126.7.0.32", {"start": v(657.75, -16.44) * mm, "end": v(657.75, -39) * mm});
            skLineSegment(sketch, "E126.7.0.33", {"start": v(720.25, -19.25) * mm, "end": v(720.25, -7.4) * mm});
            skLineSegment(sketch, "E126.7.0.34", {"start": v(657.75, 39) * mm, "end": v(657.75, 16.44) * mm});
            skArc(sketch, "E126.7.0.35", {"start": v(707.07, 20.3) * mm, "mid": v(700, 21.5) * mm, "end": v(692.93, 20.3) * mm});
            skArc(sketch, "E126.7.0.36", {"start": v(745, 39) * mm, "mid": v(743.24, 43.24) * mm, "end": v(739, 45) * mm});
            skLineSegment(sketch, "E126.7.0.37", {"start": v(714.5, 39.73) * mm, "end": v(718.6, 24.48) * mm});
            skLineSegment(sketch, "E126.7.0.38", {"start": v(718.6, -24.48) * mm, "end": v(714.5, -39.73) * mm});
            skArc(sketch, "E126.7.0.39", {"start": v(708.86, 23.09) * mm, "mid": v(700, 25) * mm, "end": v(691.14, 23.09) * mm});
            skLineSegment(sketch, "E126.7.0.40", {"start": v(655, -11.88) * mm, "end": v(655, -39) * mm});
            skArc(sketch, "E126.7.0.41", {"start": v(691.14, -23.09) * mm, "mid": v(700, -25) * mm, "end": v(708.86, -23.09) * mm});
            skLineSegment(sketch, "E126.7.0.42", {"start": v(715.8, -24.26) * mm, "end": v(710.67, -43.43) * mm});
            skLineSegment(sketch, "E126.7.0.43", {"start": v(661, -45) * mm, "end": v(688.12, -45) * mm});
            skLineSegment(sketch, "E126.7.0.44", {"start": v(742.25, 16.44) * mm, "end": v(742.25, 39) * mm});
            skLineSegment(sketch, "E126.7.0.45", {"start": v(681.4, 24.48) * mm, "end": v(685.5, 39.73) * mm});
            skLineSegment(sketch, "E126.7.0.46", {"start": v(745, -39) * mm, "end": v(745, -11.88) * mm});
            skLineSegment(sketch, "E126.7.0.47", {"start": v(656.57, 10.67) * mm, "end": v(675.74, 15.8) * mm});
            skLineSegment(sketch, "E126.7.0.48", {"start": v(742.25, -39) * mm, "end": v(742.25, -16.44) * mm});
            skArc(sketch, "E126.7.0.49", {"start": v(661, 45) * mm, "mid": v(656.76, 43.24) * mm, "end": v(655, 39) * mm});
            skLineSegment(sketch, "E126.7.0.50", {"start": v(745, 11.88) * mm, "end": v(745, 39) * mm});
            skLineSegment(sketch, "E126.7.0.51", {"start": v(719.25, 20.25) * mm, "end": v(707.4, 20.25) * mm});
            skArc(sketch, "E126.7.0.52", {"start": v(660.27, -14.5) * mm, "mid": v(658.53, -14.85) * mm, "end": v(657.75, -16.44) * mm});
            skArc(sketch, "E126.7.0.53", {"start": v(680.75, 20.25) * mm, "mid": v(680.04, 19.96) * mm, "end": v(679.75, 19.25) * mm});
            skArc(sketch, "E126.7.0.54", {"start": v(657.75, 16.44) * mm, "mid": v(658.53, 14.85) * mm, "end": v(660.27, 14.5) * mm});
            skArc(sketch, "E126.7.0.55", {"start": v(716.44, 42.25) * mm, "mid": v(714.85, 41.47) * mm, "end": v(714.5, 39.73) * mm});
            skArc(sketch, "E126.7.0.56", {"start": v(661, 42.25) * mm, "mid": v(658.7, 41.3) * mm, "end": v(657.75, 39) * mm});
            skArc(sketch, "E126.7.0.57", {"start": v(707.4, -20.25) * mm, "mid": v(707.23, -20.26) * mm, "end": v(707.07, -20.3) * mm});
            skArc(sketch, "E126.7.0.58", {"start": v(723, 21) * mm, "mid": v(722.41, 22.41) * mm, "end": v(721, 23) * mm});
            skLineSegment(sketch, "E126.7.0.59", {"start": v(677, 14.84) * mm, "end": v(677, 9.27) * mm});
            skArc(sketch, "E126.7.0.60", {"start": v(683.56, -42.25) * mm, "mid": v(685.15, -41.47) * mm, "end": v(685.5, -39.73) * mm});
            skArc(sketch, "E126.7.0.61", {"start": v(745, -11.88) * mm, "mid": v(744.51, -10.89) * mm, "end": v(743.43, -10.67) * mm});
            skArc(sketch, "E126.7.0.62", {"start": v(677, 14.84) * mm, "mid": v(676.6, 15.64) * mm, "end": v(675.74, 15.8) * mm});
            skArc(sketch, "E126.7.0.63", {"start": v(723, 20.53) * mm, "mid": v(723.41, 19.3) * mm, "end": v(724.48, 18.6) * mm});
            skLineSegment(sketch, "E126.7.0.64", {"start": v(685.16, -23) * mm, "end": v(690.73, -23) * mm});
            skArc(sketch, "E126.7.0.65", {"start": v(742.25, -16.44) * mm, "mid": v(741.47, -14.85) * mm, "end": v(739.73, -14.5) * mm});
            skArc(sketch, "E126.7.0.66", {"start": v(684.2, 24.26) * mm, "mid": v(684.36, 23.4) * mm, "end": v(685.16, 23) * mm});
            skArc(sketch, "E126.7.0.67", {"start": v(656.57, -10.67) * mm, "mid": v(655.49, -10.89) * mm, "end": v(655, -11.88) * mm});
            skArc(sketch, "E126.7.0.68", {"start": v(676.91, 8.86) * mm, "mid": v(676.98, 9.06) * mm, "end": v(677, 9.27) * mm});
            skArc(sketch, "E126.7.0.69", {"start": v(685.16, -23) * mm, "mid": v(684.36, -23.4) * mm, "end": v(684.2, -24.26) * mm});
            skArc(sketch, "E126.7.0.70", {"start": v(720.25, 19.25) * mm, "mid": v(719.96, 19.96) * mm, "end": v(719.25, 20.25) * mm});
            skLineSegment(sketch, "E126.7.0.71", {"start": v(709.27, -23) * mm, "end": v(714.84, -23) * mm});
            skLineSegment(sketch, "E126.7.0.72", {"start": v(685.16, 23) * mm, "end": v(690.73, 23) * mm});
            skArc(sketch, "E126.7.0.73", {"start": v(709.27, -23) * mm, "mid": v(709.06, -23.02) * mm, "end": v(708.86, -23.09) * mm});
            skArc(sketch, "E126.7.0.74", {"start": v(655, 11.88) * mm, "mid": v(655.49, 10.89) * mm, "end": v(656.57, 10.67) * mm});
            skArc(sketch, "E126.7.0.75", {"start": v(739.73, 14.5) * mm, "mid": v(741.47, 14.85) * mm, "end": v(742.25, 16.44) * mm});
            skArc(sketch, "E126.7.0.76", {"start": v(688.12, -45) * mm, "mid": v(689.11, -44.51) * mm, "end": v(689.33, -43.43) * mm});
            skArc(sketch, "E126.7.0.77", {"start": v(710.67, -43.43) * mm, "mid": v(710.89, -44.51) * mm, "end": v(711.88, -45) * mm});
            skLineSegment(sketch, "E126.7.0.78", {"start": v(720.53, 23) * mm, "end": v(721, 23) * mm});
            skArc(sketch, "E126.7.0.79", {"start": v(718.6, 24.48) * mm, "mid": v(719.3, 23.41) * mm, "end": v(720.53, 23) * mm});
            skLineSegment(sketch, "E126.7.0.80", {"start": v(723, 21) * mm, "end": v(723, 20.53) * mm});
            skArc(sketch, "E126.7.0.81", {"start": v(714.5, -39.73) * mm, "mid": v(714.85, -41.47) * mm, "end": v(716.44, -42.25) * mm});
            skArc(sketch, "E126.7.0.82", {"start": v(743.43, 10.67) * mm, "mid": v(744.51, 10.89) * mm, "end": v(745, 11.88) * mm});
            skArc(sketch, "E126.7.0.83", {"start": v(685.5, 39.73) * mm, "mid": v(685.15, 41.47) * mm, "end": v(683.56, 42.25) * mm});
            skLineSegment(sketch, "E126.7.0.84", {"start": v(723, -14.84) * mm, "end": v(723, -9.27) * mm});
            skArc(sketch, "E126.7.0.85", {"start": v(719.25, -20.25) * mm, "mid": v(719.96, -19.96) * mm, "end": v(720.25, -19.25) * mm});
            skArc(sketch, "E126.7.0.86", {"start": v(707.07, 20.3) * mm, "mid": v(707.23, 20.26) * mm, "end": v(707.4, 20.25) * mm});
            skArc(sketch, "E126.7.0.87", {"start": v(724.26, 15.8) * mm, "mid": v(723.4, 15.64) * mm, "end": v(723, 14.84) * mm});
            skArc(sketch, "E126.7.0.88", {"start": v(708.86, 23.09) * mm, "mid": v(709.06, 23.02) * mm, "end": v(709.27, 23) * mm});
            skArc(sketch, "E126.7.0.89", {"start": v(715.8, -24.26) * mm, "mid": v(715.64, -23.4) * mm, "end": v(714.84, -23) * mm});
            skArc(sketch, "E126.7.0.90", {"start": v(714.84, 23) * mm, "mid": v(715.64, 23.4) * mm, "end": v(715.8, 24.26) * mm});
            skArc(sketch, "E126.7.0.91", {"start": v(723, -14.84) * mm, "mid": v(723.4, -15.64) * mm, "end": v(724.26, -15.8) * mm});
            skArc(sketch, "E126.7.0.92", {"start": v(657.75, -39) * mm, "mid": v(658.7, -41.3) * mm, "end": v(661, -42.25) * mm});
            skArc(sketch, "E126.7.0.93", {"start": v(675.52, 18.6) * mm, "mid": v(676.59, 19.3) * mm, "end": v(677, 20.53) * mm});
            skLineSegment(sketch, "E126.7.0.94", {"start": v(723, 9.27) * mm, "end": v(723, 14.84) * mm});
            skArc(sketch, "E126.7.0.95", {"start": v(675.74, -15.8) * mm, "mid": v(676.6, -15.64) * mm, "end": v(677, -14.84) * mm});
            skArc(sketch, "E126.7.0.96", {"start": v(739, -42.25) * mm, "mid": v(741.3, -41.3) * mm, "end": v(742.25, -39) * mm});
            skLineSegment(sketch, "E126.7.0.97", {"start": v(709.27, 23) * mm, "end": v(714.84, 23) * mm});
            skLineSegment(sketch, "E126.7.0.98", {"start": v(677, -9.27) * mm, "end": v(677, -14.84) * mm});
            skArc(sketch, "E126.7.0.99", {"start": v(720.53, -23) * mm, "mid": v(719.3, -23.41) * mm, "end": v(718.6, -24.48) * mm});
            skArc(sketch, "E126.7.0.100", {"start": v(742.25, 39) * mm, "mid": v(741.3, 41.3) * mm, "end": v(739, 42.25) * mm});
            skArc(sketch, "E126.7.0.101", {"start": v(724.48, -18.6) * mm, "mid": v(723.41, -19.3) * mm, "end": v(723, -20.53) * mm});
            skLineSegment(sketch, "E126.7.0.102", {"start": v(679, 23) * mm, "end": v(679.47, 23) * mm});
            skArc(sketch, "E126.7.0.103", {"start": v(720.25, 7.4) * mm, "mid": v(720.26, 7.23) * mm, "end": v(720.3, 7.07) * mm});
            skLineSegment(sketch, "E126.7.0.104", {"start": v(721, -23) * mm, "end": v(720.53, -23) * mm});
            skArc(sketch, "E126.7.0.105", {"start": v(679, 23) * mm, "mid": v(677.59, 22.41) * mm, "end": v(677, 21) * mm});
            skArc(sketch, "E126.7.0.106", {"start": v(692.6, 20.25) * mm, "mid": v(692.77, 20.26) * mm, "end": v(692.93, 20.3) * mm});
            skArc(sketch, "E126.7.0.107", {"start": v(720.3, -7.07) * mm, "mid": v(720.26, -7.23) * mm, "end": v(720.25, -7.4) * mm});
            skLineSegment(sketch, "E126.7.0.108", {"start": v(677, 20.53) * mm, "end": v(677, 21) * mm});
            skArc(sketch, "E126.7.0.109", {"start": v(677, -9.27) * mm, "mid": v(676.98, -9.06) * mm, "end": v(676.91, -8.86) * mm});
            skArc(sketch, "E126.7.0.110", {"start": v(692.93, -20.3) * mm, "mid": v(692.77, -20.26) * mm, "end": v(692.6, -20.25) * mm});
            skArc(sketch, "E126.7.0.111", {"start": v(679.75, -7.4) * mm, "mid": v(679.74, -7.23) * mm, "end": v(679.7, -7.07) * mm});
            skArc(sketch, "E126.7.0.112", {"start": v(723, 9.27) * mm, "mid": v(723.02, 9.06) * mm, "end": v(723.09, 8.86) * mm});
            skArc(sketch, "E126.7.0.113", {"start": v(691.14, -23.09) * mm, "mid": v(690.94, -23.02) * mm, "end": v(690.73, -23) * mm});
            skArc(sketch, "E126.7.0.114", {"start": v(721, -23) * mm, "mid": v(722.41, -22.41) * mm, "end": v(723, -21) * mm});
            skArc(sketch, "E126.7.0.115", {"start": v(690.73, 23) * mm, "mid": v(690.94, 23.02) * mm, "end": v(691.14, 23.09) * mm});
            skArc(sketch, "E126.7.0.116", {"start": v(677, -20.53) * mm, "mid": v(676.59, -19.3) * mm, "end": v(675.52, -18.6) * mm});
            skArc(sketch, "E126.7.0.117", {"start": v(679.75, -19.25) * mm, "mid": v(680.04, -19.96) * mm, "end": v(680.75, -20.25) * mm});
            skArc(sketch, "E126.7.0.118", {"start": v(679.7, 7.07) * mm, "mid": v(679.74, 7.23) * mm, "end": v(679.75, 7.4) * mm});
            skArc(sketch, "E126.7.0.119", {"start": v(679.47, 23) * mm, "mid": v(680.7, 23.41) * mm, "end": v(681.4, 24.48) * mm});
            skLineSegment(sketch, "E126.7.0.120", {"start": v(679.47, -23) * mm, "end": v(679, -23) * mm});
            skArc(sketch, "E126.7.0.121", {"start": v(677, -21) * mm, "mid": v(677.59, -22.41) * mm, "end": v(679, -23) * mm});
            skArc(sketch, "E126.7.0.122", {"start": v(723.09, -8.86) * mm, "mid": v(723.02, -9.06) * mm, "end": v(723, -9.27) * mm});
            skLineSegment(sketch, "E126.7.0.123", {"start": v(677, -21) * mm, "end": v(677, -20.53) * mm});
            skArc(sketch, "E126.7.0.124", {"start": v(681.4, -24.48) * mm, "mid": v(680.7, -23.41) * mm, "end": v(679.47, -23) * mm});
            skLineSegment(sketch, "E126.7.0.125", {"start": v(723, -20.53) * mm, "end": v(723, -21) * mm});
            skLineSegment(sketch, "E126.8.0.0", {"start": v(816.44, -42.25) * mm, "end": v(839, -42.25) * mm});
            skLineSegment(sketch, "E126.8.0.1", {"start": v(843.43, -10.67) * mm, "end": v(824.26, -15.8) * mm});
            skLineSegment(sketch, "E126.8.0.2", {"start": v(839, 45) * mm, "end": v(761, 45) * mm});
            skLineSegment(sketch, "E126.8.0.3", {"start": v(820.25, 7.4) * mm, "end": v(820.25, 19.25) * mm});
            skLineSegment(sketch, "E126.8.0.4", {"start": v(792.6, 20.25) * mm, "end": v(780.75, 20.25) * mm});
            skLineSegment(sketch, "E126.8.0.5", {"start": v(807.4, -20.25) * mm, "end": v(819.25, -20.25) * mm});
            skArc(sketch, "E126.8.0.6", {"start": v(820.3, -7.07) * mm, "mid": v(821.5, 0) * mm, "end": v(820.3, 7.07) * mm});
            skLineSegment(sketch, "E126.8.0.7", {"start": v(815.8, 24.26) * mm, "end": v(810.99, 42.25) * mm});
            skLineSegment(sketch, "E126.8.0.8", {"start": v(789.33, -43.43) * mm, "end": v(784.2, -24.26) * mm});
            skLineSegment(sketch, "E126.8.0.9", {"start": v(775.74, -15.8) * mm, "end": v(756.57, -10.67) * mm});
            skArc(sketch, "E126.8.0.10", {"start": v(755, -39) * mm, "mid": v(756.76, -43.24) * mm, "end": v(761, -45) * mm});
            skArc(sketch, "E126.8.0.11", {"start": v(779.7, 7.07) * mm, "mid": v(778.5, 0) * mm, "end": v(779.7, -7.07) * mm});
            skArc(sketch, "E126.8.0.12", {"start": v(792.93, -20.3) * mm, "mid": v(800, -21.5) * mm, "end": v(807.07, -20.3) * mm});
            skLineSegment(sketch, "E126.8.0.13", {"start": v(789.01, 42.25) * mm, "end": v(784.2, 24.26) * mm});
            skLineSegment(sketch, "E126.8.0.14", {"start": v(839.73, -14.5) * mm, "end": v(824.48, -18.6) * mm});
            skLineSegment(sketch, "E126.8.0.15", {"start": v(775.52, -18.6) * mm, "end": v(760.27, -14.5) * mm});
            skLineSegment(sketch, "E126.8.0.16", {"start": v(761, -42.25) * mm, "end": v(783.56, -42.25) * mm});
            skLineSegment(sketch, "E126.8.0.17", {"start": v(783.56, 42.25) * mm, "end": v(761, 42.25) * mm});
            skLineSegment(sketch, "E126.8.0.18", {"start": v(839, 42.25) * mm, "end": v(816.44, 42.25) * mm});
            skLineSegment(sketch, "E126.8.0.19", {"start": v(810.99, 42.25) * mm, "end": v(789.01, 42.25) * mm});
            skLineSegment(sketch, "E126.8.0.20", {"start": v(824.26, 15.8) * mm, "end": v(843.43, 10.67) * mm});
            skLineSegment(sketch, "E126.8.0.21", {"start": v(779.75, -7.4) * mm, "end": v(779.75, -19.25) * mm});
            skArc(sketch, "E126.8.0.22", {"start": v(839, -45) * mm, "mid": v(843.24, -43.24) * mm, "end": v(845, -39) * mm});
            skLineSegment(sketch, "E126.8.0.23", {"start": v(780.75, -20.25) * mm, "end": v(792.6, -20.25) * mm});
            skLineSegment(sketch, "E126.8.0.24", {"start": v(824.48, 18.6) * mm, "end": v(839.73, 14.5) * mm});
            skArc(sketch, "E126.8.0.25", {"start": v(776.91, 8.86) * mm, "mid": v(775, 0) * mm, "end": v(776.91, -8.86) * mm});
            skLineSegment(sketch, "E126.8.0.26", {"start": v(779.75, 19.25) * mm, "end": v(779.75, 7.4) * mm});
            skArc(sketch, "E126.8.0.27", {"start": v(823.09, -8.86) * mm, "mid": v(825, 0) * mm, "end": v(823.09, 8.86) * mm});
            skLineSegment(sketch, "E126.8.0.28", {"start": v(760.27, 14.5) * mm, "end": v(775.52, 18.6) * mm});
            skLineSegment(sketch, "E126.8.0.29", {"start": v(785.5, -39.73) * mm, "end": v(781.4, -24.48) * mm});
            skLineSegment(sketch, "E126.8.0.30", {"start": v(811.88, -45) * mm, "end": v(839, -45) * mm});
            skLineSegment(sketch, "E126.8.0.31", {"start": v(755, 39) * mm, "end": v(755, 11.88) * mm});
            skLineSegment(sketch, "E126.8.0.32", {"start": v(757.75, -16.44) * mm, "end": v(757.75, -39) * mm});
            skLineSegment(sketch, "E126.8.0.33", {"start": v(820.25, -19.25) * mm, "end": v(820.25, -7.4) * mm});
            skLineSegment(sketch, "E126.8.0.34", {"start": v(757.75, 39) * mm, "end": v(757.75, 16.44) * mm});
            skArc(sketch, "E126.8.0.35", {"start": v(807.07, 20.3) * mm, "mid": v(800, 21.5) * mm, "end": v(792.93, 20.3) * mm});
            skArc(sketch, "E126.8.0.36", {"start": v(845, 39) * mm, "mid": v(843.24, 43.24) * mm, "end": v(839, 45) * mm});
            skLineSegment(sketch, "E126.8.0.37", {"start": v(814.5, 39.73) * mm, "end": v(818.6, 24.48) * mm});
            skLineSegment(sketch, "E126.8.0.38", {"start": v(818.6, -24.48) * mm, "end": v(814.5, -39.73) * mm});
            skArc(sketch, "E126.8.0.39", {"start": v(808.86, 23.09) * mm, "mid": v(800, 25) * mm, "end": v(791.14, 23.09) * mm});
            skLineSegment(sketch, "E126.8.0.40", {"start": v(755, -11.88) * mm, "end": v(755, -39) * mm});
            skArc(sketch, "E126.8.0.41", {"start": v(791.14, -23.09) * mm, "mid": v(800, -25) * mm, "end": v(808.86, -23.09) * mm});
            skLineSegment(sketch, "E126.8.0.42", {"start": v(815.8, -24.26) * mm, "end": v(810.67, -43.43) * mm});
            skLineSegment(sketch, "E126.8.0.43", {"start": v(761, -45) * mm, "end": v(788.12, -45) * mm});
            skLineSegment(sketch, "E126.8.0.44", {"start": v(842.25, 16.44) * mm, "end": v(842.25, 39) * mm});
            skLineSegment(sketch, "E126.8.0.45", {"start": v(781.4, 24.48) * mm, "end": v(785.5, 39.73) * mm});
            skLineSegment(sketch, "E126.8.0.46", {"start": v(845, -39) * mm, "end": v(845, -11.88) * mm});
            skLineSegment(sketch, "E126.8.0.47", {"start": v(756.57, 10.67) * mm, "end": v(775.74, 15.8) * mm});
            skLineSegment(sketch, "E126.8.0.48", {"start": v(842.25, -39) * mm, "end": v(842.25, -16.44) * mm});
            skArc(sketch, "E126.8.0.49", {"start": v(761, 45) * mm, "mid": v(756.76, 43.24) * mm, "end": v(755, 39) * mm});
            skLineSegment(sketch, "E126.8.0.50", {"start": v(845, 11.88) * mm, "end": v(845, 39) * mm});
            skLineSegment(sketch, "E126.8.0.51", {"start": v(819.25, 20.25) * mm, "end": v(807.4, 20.25) * mm});
            skArc(sketch, "E126.8.0.52", {"start": v(760.27, -14.5) * mm, "mid": v(758.53, -14.85) * mm, "end": v(757.75, -16.44) * mm});
            skArc(sketch, "E126.8.0.53", {"start": v(780.75, 20.25) * mm, "mid": v(780.04, 19.96) * mm, "end": v(779.75, 19.25) * mm});
            skArc(sketch, "E126.8.0.54", {"start": v(757.75, 16.44) * mm, "mid": v(758.53, 14.85) * mm, "end": v(760.27, 14.5) * mm});
            skArc(sketch, "E126.8.0.55", {"start": v(816.44, 42.25) * mm, "mid": v(814.85, 41.47) * mm, "end": v(814.5, 39.73) * mm});
            skArc(sketch, "E126.8.0.56", {"start": v(761, 42.25) * mm, "mid": v(758.7, 41.3) * mm, "end": v(757.75, 39) * mm});
            skArc(sketch, "E126.8.0.57", {"start": v(807.4, -20.25) * mm, "mid": v(807.23, -20.26) * mm, "end": v(807.07, -20.3) * mm});
            skArc(sketch, "E126.8.0.58", {"start": v(823, 21) * mm, "mid": v(822.41, 22.41) * mm, "end": v(821, 23) * mm});
            skLineSegment(sketch, "E126.8.0.59", {"start": v(777, 14.84) * mm, "end": v(777, 9.27) * mm});
            skArc(sketch, "E126.8.0.60", {"start": v(783.56, -42.25) * mm, "mid": v(785.15, -41.47) * mm, "end": v(785.5, -39.73) * mm});
            skArc(sketch, "E126.8.0.61", {"start": v(845, -11.88) * mm, "mid": v(844.51, -10.89) * mm, "end": v(843.43, -10.67) * mm});
            skArc(sketch, "E126.8.0.62", {"start": v(777, 14.84) * mm, "mid": v(776.6, 15.64) * mm, "end": v(775.74, 15.8) * mm});
            skArc(sketch, "E126.8.0.63", {"start": v(823, 20.53) * mm, "mid": v(823.41, 19.3) * mm, "end": v(824.48, 18.6) * mm});
            skLineSegment(sketch, "E126.8.0.64", {"start": v(785.16, -23) * mm, "end": v(790.73, -23) * mm});
            skArc(sketch, "E126.8.0.65", {"start": v(842.25, -16.44) * mm, "mid": v(841.47, -14.85) * mm, "end": v(839.73, -14.5) * mm});
            skArc(sketch, "E126.8.0.66", {"start": v(784.2, 24.26) * mm, "mid": v(784.36, 23.4) * mm, "end": v(785.16, 23) * mm});
            skArc(sketch, "E126.8.0.67", {"start": v(756.57, -10.67) * mm, "mid": v(755.49, -10.89) * mm, "end": v(755, -11.88) * mm});
            skArc(sketch, "E126.8.0.68", {"start": v(776.91, 8.86) * mm, "mid": v(776.98, 9.06) * mm, "end": v(777, 9.27) * mm});
            skArc(sketch, "E126.8.0.69", {"start": v(785.16, -23) * mm, "mid": v(784.36, -23.4) * mm, "end": v(784.2, -24.26) * mm});
            skArc(sketch, "E126.8.0.70", {"start": v(820.25, 19.25) * mm, "mid": v(819.96, 19.96) * mm, "end": v(819.25, 20.25) * mm});
            skLineSegment(sketch, "E126.8.0.71", {"start": v(809.27, -23) * mm, "end": v(814.84, -23) * mm});
            skLineSegment(sketch, "E126.8.0.72", {"start": v(785.16, 23) * mm, "end": v(790.73, 23) * mm});
            skArc(sketch, "E126.8.0.73", {"start": v(809.27, -23) * mm, "mid": v(809.06, -23.02) * mm, "end": v(808.86, -23.09) * mm});
            skArc(sketch, "E126.8.0.74", {"start": v(755, 11.88) * mm, "mid": v(755.49, 10.89) * mm, "end": v(756.57, 10.67) * mm});
            skArc(sketch, "E126.8.0.75", {"start": v(839.73, 14.5) * mm, "mid": v(841.47, 14.85) * mm, "end": v(842.25, 16.44) * mm});
            skArc(sketch, "E126.8.0.76", {"start": v(788.12, -45) * mm, "mid": v(789.11, -44.51) * mm, "end": v(789.33, -43.43) * mm});
            skArc(sketch, "E126.8.0.77", {"start": v(810.67, -43.43) * mm, "mid": v(810.89, -44.51) * mm, "end": v(811.88, -45) * mm});
            skLineSegment(sketch, "E126.8.0.78", {"start": v(820.53, 23) * mm, "end": v(821, 23) * mm});
            skArc(sketch, "E126.8.0.79", {"start": v(818.6, 24.48) * mm, "mid": v(819.3, 23.41) * mm, "end": v(820.53, 23) * mm});
            skLineSegment(sketch, "E126.8.0.80", {"start": v(823, 21) * mm, "end": v(823, 20.53) * mm});
            skArc(sketch, "E126.8.0.81", {"start": v(814.5, -39.73) * mm, "mid": v(814.85, -41.47) * mm, "end": v(816.44, -42.25) * mm});
            skArc(sketch, "E126.8.0.82", {"start": v(843.43, 10.67) * mm, "mid": v(844.51, 10.89) * mm, "end": v(845, 11.88) * mm});
            skArc(sketch, "E126.8.0.83", {"start": v(785.5, 39.73) * mm, "mid": v(785.15, 41.47) * mm, "end": v(783.56, 42.25) * mm});
            skLineSegment(sketch, "E126.8.0.84", {"start": v(823, -14.84) * mm, "end": v(823, -9.27) * mm});
            skArc(sketch, "E126.8.0.85", {"start": v(819.25, -20.25) * mm, "mid": v(819.96, -19.96) * mm, "end": v(820.25, -19.25) * mm});
            skArc(sketch, "E126.8.0.86", {"start": v(807.07, 20.3) * mm, "mid": v(807.23, 20.26) * mm, "end": v(807.4, 20.25) * mm});
            skArc(sketch, "E126.8.0.87", {"start": v(824.26, 15.8) * mm, "mid": v(823.4, 15.64) * mm, "end": v(823, 14.84) * mm});
            skArc(sketch, "E126.8.0.88", {"start": v(808.86, 23.09) * mm, "mid": v(809.06, 23.02) * mm, "end": v(809.27, 23) * mm});
            skArc(sketch, "E126.8.0.89", {"start": v(815.8, -24.26) * mm, "mid": v(815.64, -23.4) * mm, "end": v(814.84, -23) * mm});
            skArc(sketch, "E126.8.0.90", {"start": v(814.84, 23) * mm, "mid": v(815.64, 23.4) * mm, "end": v(815.8, 24.26) * mm});
            skArc(sketch, "E126.8.0.91", {"start": v(823, -14.84) * mm, "mid": v(823.4, -15.64) * mm, "end": v(824.26, -15.8) * mm});
            skArc(sketch, "E126.8.0.92", {"start": v(757.75, -39) * mm, "mid": v(758.7, -41.3) * mm, "end": v(761, -42.25) * mm});
            skArc(sketch, "E126.8.0.93", {"start": v(775.52, 18.6) * mm, "mid": v(776.59, 19.3) * mm, "end": v(777, 20.53) * mm});
            skLineSegment(sketch, "E126.8.0.94", {"start": v(823, 9.27) * mm, "end": v(823, 14.84) * mm});
            skArc(sketch, "E126.8.0.95", {"start": v(775.74, -15.8) * mm, "mid": v(776.6, -15.64) * mm, "end": v(777, -14.84) * mm});
            skArc(sketch, "E126.8.0.96", {"start": v(839, -42.25) * mm, "mid": v(841.3, -41.3) * mm, "end": v(842.25, -39) * mm});
            skLineSegment(sketch, "E126.8.0.97", {"start": v(809.27, 23) * mm, "end": v(814.84, 23) * mm});
            skLineSegment(sketch, "E126.8.0.98", {"start": v(777, -9.27) * mm, "end": v(777, -14.84) * mm});
            skArc(sketch, "E126.8.0.99", {"start": v(820.53, -23) * mm, "mid": v(819.3, -23.41) * mm, "end": v(818.6, -24.48) * mm});
            skArc(sketch, "E126.8.0.100", {"start": v(842.25, 39) * mm, "mid": v(841.3, 41.3) * mm, "end": v(839, 42.25) * mm});
            skArc(sketch, "E126.8.0.101", {"start": v(824.48, -18.6) * mm, "mid": v(823.41, -19.3) * mm, "end": v(823, -20.53) * mm});
            skLineSegment(sketch, "E126.8.0.102", {"start": v(779, 23) * mm, "end": v(779.47, 23) * mm});
            skArc(sketch, "E126.8.0.103", {"start": v(820.25, 7.4) * mm, "mid": v(820.26, 7.23) * mm, "end": v(820.3, 7.07) * mm});
            skLineSegment(sketch, "E126.8.0.104", {"start": v(821, -23) * mm, "end": v(820.53, -23) * mm});
            skArc(sketch, "E126.8.0.105", {"start": v(779, 23) * mm, "mid": v(777.59, 22.41) * mm, "end": v(777, 21) * mm});
            skArc(sketch, "E126.8.0.106", {"start": v(792.6, 20.25) * mm, "mid": v(792.77, 20.26) * mm, "end": v(792.93, 20.3) * mm});
            skArc(sketch, "E126.8.0.107", {"start": v(820.3, -7.07) * mm, "mid": v(820.26, -7.23) * mm, "end": v(820.25, -7.4) * mm});
            skLineSegment(sketch, "E126.8.0.108", {"start": v(777, 20.53) * mm, "end": v(777, 21) * mm});
            skArc(sketch, "E126.8.0.109", {"start": v(777, -9.27) * mm, "mid": v(776.98, -9.06) * mm, "end": v(776.91, -8.86) * mm});
            skArc(sketch, "E126.8.0.110", {"start": v(792.93, -20.3) * mm, "mid": v(792.77, -20.26) * mm, "end": v(792.6, -20.25) * mm});
            skArc(sketch, "E126.8.0.111", {"start": v(779.75, -7.4) * mm, "mid": v(779.74, -7.23) * mm, "end": v(779.7, -7.07) * mm});
            skArc(sketch, "E126.8.0.112", {"start": v(823, 9.27) * mm, "mid": v(823.02, 9.06) * mm, "end": v(823.09, 8.86) * mm});
            skArc(sketch, "E126.8.0.113", {"start": v(791.14, -23.09) * mm, "mid": v(790.94, -23.02) * mm, "end": v(790.73, -23) * mm});
            skArc(sketch, "E126.8.0.114", {"start": v(821, -23) * mm, "mid": v(822.41, -22.41) * mm, "end": v(823, -21) * mm});
            skArc(sketch, "E126.8.0.115", {"start": v(790.73, 23) * mm, "mid": v(790.94, 23.02) * mm, "end": v(791.14, 23.09) * mm});
            skArc(sketch, "E126.8.0.116", {"start": v(777, -20.53) * mm, "mid": v(776.59, -19.3) * mm, "end": v(775.52, -18.6) * mm});
            skArc(sketch, "E126.8.0.117", {"start": v(779.75, -19.25) * mm, "mid": v(780.04, -19.96) * mm, "end": v(780.75, -20.25) * mm});
            skArc(sketch, "E126.8.0.118", {"start": v(779.7, 7.07) * mm, "mid": v(779.74, 7.23) * mm, "end": v(779.75, 7.4) * mm});
            skArc(sketch, "E126.8.0.119", {"start": v(779.47, 23) * mm, "mid": v(780.7, 23.41) * mm, "end": v(781.4, 24.48) * mm});
            skLineSegment(sketch, "E126.8.0.120", {"start": v(779.47, -23) * mm, "end": v(779, -23) * mm});
            skArc(sketch, "E126.8.0.121", {"start": v(777, -21) * mm, "mid": v(777.59, -22.41) * mm, "end": v(779, -23) * mm});
            skArc(sketch, "E126.8.0.122", {"start": v(823.09, -8.86) * mm, "mid": v(823.02, -9.06) * mm, "end": v(823, -9.27) * mm});
            skLineSegment(sketch, "E126.8.0.123", {"start": v(777, -21) * mm, "end": v(777, -20.53) * mm});
            skArc(sketch, "E126.8.0.124", {"start": v(781.4, -24.48) * mm, "mid": v(780.7, -23.41) * mm, "end": v(779.47, -23) * mm});
            skLineSegment(sketch, "E126.8.0.125", {"start": v(823, -20.53) * mm, "end": v(823, -21) * mm});
            skLineSegment(sketch, "E126.9.0.0", {"start": v(916.44, -42.25) * mm, "end": v(939, -42.25) * mm});
            skLineSegment(sketch, "E126.9.0.1", {"start": v(943.43, -10.67) * mm, "end": v(924.26, -15.8) * mm});
            skLineSegment(sketch, "E126.9.0.2", {"start": v(939, 45) * mm, "end": v(861, 45) * mm});
            skLineSegment(sketch, "E126.9.0.3", {"start": v(920.25, 7.4) * mm, "end": v(920.25, 19.25) * mm});
            skLineSegment(sketch, "E126.9.0.4", {"start": v(892.6, 20.25) * mm, "end": v(880.75, 20.25) * mm});
            skLineSegment(sketch, "E126.9.0.5", {"start": v(907.4, -20.25) * mm, "end": v(919.25, -20.25) * mm});
            skArc(sketch, "E126.9.0.6", {"start": v(920.3, -7.07) * mm, "mid": v(921.5, 0) * mm, "end": v(920.3, 7.07) * mm});
            skLineSegment(sketch, "E126.9.0.7", {"start": v(915.8, 24.26) * mm, "end": v(910.99, 42.25) * mm});
            skLineSegment(sketch, "E126.9.0.8", {"start": v(889.33, -43.43) * mm, "end": v(884.2, -24.26) * mm});
            skLineSegment(sketch, "E126.9.0.9", {"start": v(875.74, -15.8) * mm, "end": v(856.57, -10.67) * mm});
            skArc(sketch, "E126.9.0.10", {"start": v(855, -39) * mm, "mid": v(856.76, -43.24) * mm, "end": v(861, -45) * mm});
            skArc(sketch, "E126.9.0.11", {"start": v(879.7, 7.07) * mm, "mid": v(878.5, 0) * mm, "end": v(879.7, -7.07) * mm});
            skArc(sketch, "E126.9.0.12", {"start": v(892.93, -20.3) * mm, "mid": v(900, -21.5) * mm, "end": v(907.07, -20.3) * mm});
            skLineSegment(sketch, "E126.9.0.13", {"start": v(889.01, 42.25) * mm, "end": v(884.2, 24.26) * mm});
            skLineSegment(sketch, "E126.9.0.14", {"start": v(939.73, -14.5) * mm, "end": v(924.48, -18.6) * mm});
            skLineSegment(sketch, "E126.9.0.15", {"start": v(875.52, -18.6) * mm, "end": v(860.27, -14.5) * mm});
            skLineSegment(sketch, "E126.9.0.16", {"start": v(861, -42.25) * mm, "end": v(883.56, -42.25) * mm});
            skLineSegment(sketch, "E126.9.0.17", {"start": v(883.56, 42.25) * mm, "end": v(861, 42.25) * mm});
            skLineSegment(sketch, "E126.9.0.18", {"start": v(939, 42.25) * mm, "end": v(916.44, 42.25) * mm});
            skLineSegment(sketch, "E126.9.0.19", {"start": v(910.99, 42.25) * mm, "end": v(889.01, 42.25) * mm});
            skLineSegment(sketch, "E126.9.0.20", {"start": v(924.26, 15.8) * mm, "end": v(943.43, 10.67) * mm});
            skLineSegment(sketch, "E126.9.0.21", {"start": v(879.75, -7.4) * mm, "end": v(879.75, -19.25) * mm});
            skArc(sketch, "E126.9.0.22", {"start": v(939, -45) * mm, "mid": v(943.24, -43.24) * mm, "end": v(945, -39) * mm});
            skLineSegment(sketch, "E126.9.0.23", {"start": v(880.75, -20.25) * mm, "end": v(892.6, -20.25) * mm});
            skLineSegment(sketch, "E126.9.0.24", {"start": v(924.48, 18.6) * mm, "end": v(939.73, 14.5) * mm});
            skArc(sketch, "E126.9.0.25", {"start": v(876.91, 8.86) * mm, "mid": v(875, 0) * mm, "end": v(876.91, -8.86) * mm});
            skLineSegment(sketch, "E126.9.0.26", {"start": v(879.75, 19.25) * mm, "end": v(879.75, 7.4) * mm});
            skArc(sketch, "E126.9.0.27", {"start": v(923.09, -8.86) * mm, "mid": v(925, 0) * mm, "end": v(923.09, 8.86) * mm});
            skLineSegment(sketch, "E126.9.0.28", {"start": v(860.27, 14.5) * mm, "end": v(875.52, 18.6) * mm});
            skLineSegment(sketch, "E126.9.0.29", {"start": v(885.5, -39.73) * mm, "end": v(881.4, -24.48) * mm});
            skLineSegment(sketch, "E126.9.0.30", {"start": v(911.88, -45) * mm, "end": v(939, -45) * mm});
            skLineSegment(sketch, "E126.9.0.31", {"start": v(855, 39) * mm, "end": v(855, 11.88) * mm});
            skLineSegment(sketch, "E126.9.0.32", {"start": v(857.75, -16.44) * mm, "end": v(857.75, -39) * mm});
            skLineSegment(sketch, "E126.9.0.33", {"start": v(920.25, -19.25) * mm, "end": v(920.25, -7.4) * mm});
            skLineSegment(sketch, "E126.9.0.34", {"start": v(857.75, 39) * mm, "end": v(857.75, 16.44) * mm});
            skArc(sketch, "E126.9.0.35", {"start": v(907.07, 20.3) * mm, "mid": v(900, 21.5) * mm, "end": v(892.93, 20.3) * mm});
            skArc(sketch, "E126.9.0.36", {"start": v(945, 39) * mm, "mid": v(943.24, 43.24) * mm, "end": v(939, 45) * mm});
            skLineSegment(sketch, "E126.9.0.37", {"start": v(914.5, 39.73) * mm, "end": v(918.6, 24.48) * mm});
            skLineSegment(sketch, "E126.9.0.38", {"start": v(918.6, -24.48) * mm, "end": v(914.5, -39.73) * mm});
            skArc(sketch, "E126.9.0.39", {"start": v(908.86, 23.09) * mm, "mid": v(900, 25) * mm, "end": v(891.14, 23.09) * mm});
            skLineSegment(sketch, "E126.9.0.40", {"start": v(855, -11.88) * mm, "end": v(855, -39) * mm});
            skArc(sketch, "E126.9.0.41", {"start": v(891.14, -23.09) * mm, "mid": v(900, -25) * mm, "end": v(908.86, -23.09) * mm});
            skLineSegment(sketch, "E126.9.0.42", {"start": v(915.8, -24.26) * mm, "end": v(910.67, -43.43) * mm});
            skLineSegment(sketch, "E126.9.0.43", {"start": v(861, -45) * mm, "end": v(888.12, -45) * mm});
            skLineSegment(sketch, "E126.9.0.44", {"start": v(942.25, 16.44) * mm, "end": v(942.25, 39) * mm});
            skLineSegment(sketch, "E126.9.0.45", {"start": v(881.4, 24.48) * mm, "end": v(885.5, 39.73) * mm});
            skLineSegment(sketch, "E126.9.0.46", {"start": v(945, -39) * mm, "end": v(945, -11.88) * mm});
            skLineSegment(sketch, "E126.9.0.47", {"start": v(856.57, 10.67) * mm, "end": v(875.74, 15.8) * mm});
            skLineSegment(sketch, "E126.9.0.48", {"start": v(942.25, -39) * mm, "end": v(942.25, -16.44) * mm});
            skArc(sketch, "E126.9.0.49", {"start": v(861, 45) * mm, "mid": v(856.76, 43.24) * mm, "end": v(855, 39) * mm});
            skLineSegment(sketch, "E126.9.0.50", {"start": v(945, 11.88) * mm, "end": v(945, 39) * mm});
            skLineSegment(sketch, "E126.9.0.51", {"start": v(919.25, 20.25) * mm, "end": v(907.4, 20.25) * mm});
            skArc(sketch, "E126.9.0.52", {"start": v(860.27, -14.5) * mm, "mid": v(858.53, -14.85) * mm, "end": v(857.75, -16.44) * mm});
            skArc(sketch, "E126.9.0.53", {"start": v(880.75, 20.25) * mm, "mid": v(880.04, 19.96) * mm, "end": v(879.75, 19.25) * mm});
            skArc(sketch, "E126.9.0.54", {"start": v(857.75, 16.44) * mm, "mid": v(858.53, 14.85) * mm, "end": v(860.27, 14.5) * mm});
            skArc(sketch, "E126.9.0.55", {"start": v(916.44, 42.25) * mm, "mid": v(914.85, 41.47) * mm, "end": v(914.5, 39.73) * mm});
            skArc(sketch, "E126.9.0.56", {"start": v(861, 42.25) * mm, "mid": v(858.7, 41.3) * mm, "end": v(857.75, 39) * mm});
            skArc(sketch, "E126.9.0.57", {"start": v(907.4, -20.25) * mm, "mid": v(907.23, -20.26) * mm, "end": v(907.07, -20.3) * mm});
            skArc(sketch, "E126.9.0.58", {"start": v(923, 21) * mm, "mid": v(922.41, 22.41) * mm, "end": v(921, 23) * mm});
            skLineSegment(sketch, "E126.9.0.59", {"start": v(877, 14.84) * mm, "end": v(877, 9.27) * mm});
            skArc(sketch, "E126.9.0.60", {"start": v(883.56, -42.25) * mm, "mid": v(885.15, -41.47) * mm, "end": v(885.5, -39.73) * mm});
            skArc(sketch, "E126.9.0.61", {"start": v(945, -11.88) * mm, "mid": v(944.51, -10.89) * mm, "end": v(943.43, -10.67) * mm});
            skArc(sketch, "E126.9.0.62", {"start": v(877, 14.84) * mm, "mid": v(876.6, 15.64) * mm, "end": v(875.74, 15.8) * mm});
            skArc(sketch, "E126.9.0.63", {"start": v(923, 20.53) * mm, "mid": v(923.41, 19.3) * mm, "end": v(924.48, 18.6) * mm});
            skLineSegment(sketch, "E126.9.0.64", {"start": v(885.16, -23) * mm, "end": v(890.73, -23) * mm});
            skArc(sketch, "E126.9.0.65", {"start": v(942.25, -16.44) * mm, "mid": v(941.47, -14.85) * mm, "end": v(939.73, -14.5) * mm});
            skArc(sketch, "E126.9.0.66", {"start": v(884.2, 24.26) * mm, "mid": v(884.36, 23.4) * mm, "end": v(885.16, 23) * mm});
            skArc(sketch, "E126.9.0.67", {"start": v(856.57, -10.67) * mm, "mid": v(855.49, -10.89) * mm, "end": v(855, -11.88) * mm});
            skArc(sketch, "E126.9.0.68", {"start": v(876.91, 8.86) * mm, "mid": v(876.98, 9.06) * mm, "end": v(877, 9.27) * mm});
            skArc(sketch, "E126.9.0.69", {"start": v(885.16, -23) * mm, "mid": v(884.36, -23.4) * mm, "end": v(884.2, -24.26) * mm});
            skArc(sketch, "E126.9.0.70", {"start": v(920.25, 19.25) * mm, "mid": v(919.96, 19.96) * mm, "end": v(919.25, 20.25) * mm});
            skLineSegment(sketch, "E126.9.0.71", {"start": v(909.27, -23) * mm, "end": v(914.84, -23) * mm});
            skLineSegment(sketch, "E126.9.0.72", {"start": v(885.16, 23) * mm, "end": v(890.73, 23) * mm});
            skArc(sketch, "E126.9.0.73", {"start": v(909.27, -23) * mm, "mid": v(909.06, -23.02) * mm, "end": v(908.86, -23.09) * mm});
            skArc(sketch, "E126.9.0.74", {"start": v(855, 11.88) * mm, "mid": v(855.49, 10.89) * mm, "end": v(856.57, 10.67) * mm});
            skArc(sketch, "E126.9.0.75", {"start": v(939.73, 14.5) * mm, "mid": v(941.47, 14.85) * mm, "end": v(942.25, 16.44) * mm});
            skArc(sketch, "E126.9.0.76", {"start": v(888.12, -45) * mm, "mid": v(889.11, -44.51) * mm, "end": v(889.33, -43.43) * mm});
            skArc(sketch, "E126.9.0.77", {"start": v(910.67, -43.43) * mm, "mid": v(910.89, -44.51) * mm, "end": v(911.88, -45) * mm});
            skLineSegment(sketch, "E126.9.0.78", {"start": v(920.53, 23) * mm, "end": v(921, 23) * mm});
            skArc(sketch, "E126.9.0.79", {"start": v(918.6, 24.48) * mm, "mid": v(919.3, 23.41) * mm, "end": v(920.53, 23) * mm});
            skLineSegment(sketch, "E126.9.0.80", {"start": v(923, 21) * mm, "end": v(923, 20.53) * mm});
            skArc(sketch, "E126.9.0.81", {"start": v(914.5, -39.73) * mm, "mid": v(914.85, -41.47) * mm, "end": v(916.44, -42.25) * mm});
            skArc(sketch, "E126.9.0.82", {"start": v(943.43, 10.67) * mm, "mid": v(944.51, 10.89) * mm, "end": v(945, 11.88) * mm});
            skArc(sketch, "E126.9.0.83", {"start": v(885.5, 39.73) * mm, "mid": v(885.15, 41.47) * mm, "end": v(883.56, 42.25) * mm});
            skLineSegment(sketch, "E126.9.0.84", {"start": v(923, -14.84) * mm, "end": v(923, -9.27) * mm});
            skArc(sketch, "E126.9.0.85", {"start": v(919.25, -20.25) * mm, "mid": v(919.96, -19.96) * mm, "end": v(920.25, -19.25) * mm});
            skArc(sketch, "E126.9.0.86", {"start": v(907.07, 20.3) * mm, "mid": v(907.23, 20.26) * mm, "end": v(907.4, 20.25) * mm});
            skArc(sketch, "E126.9.0.87", {"start": v(924.26, 15.8) * mm, "mid": v(923.4, 15.64) * mm, "end": v(923, 14.84) * mm});
            skArc(sketch, "E126.9.0.88", {"start": v(908.86, 23.09) * mm, "mid": v(909.06, 23.02) * mm, "end": v(909.27, 23) * mm});
            skArc(sketch, "E126.9.0.89", {"start": v(915.8, -24.26) * mm, "mid": v(915.64, -23.4) * mm, "end": v(914.84, -23) * mm});
            skArc(sketch, "E126.9.0.90", {"start": v(914.84, 23) * mm, "mid": v(915.64, 23.4) * mm, "end": v(915.8, 24.26) * mm});
            skArc(sketch, "E126.9.0.91", {"start": v(923, -14.84) * mm, "mid": v(923.4, -15.64) * mm, "end": v(924.26, -15.8) * mm});
            skArc(sketch, "E126.9.0.92", {"start": v(857.75, -39) * mm, "mid": v(858.7, -41.3) * mm, "end": v(861, -42.25) * mm});
            skArc(sketch, "E126.9.0.93", {"start": v(875.52, 18.6) * mm, "mid": v(876.59, 19.3) * mm, "end": v(877, 20.53) * mm});
            skLineSegment(sketch, "E126.9.0.94", {"start": v(923, 9.27) * mm, "end": v(923, 14.84) * mm});
            skArc(sketch, "E126.9.0.95", {"start": v(875.74, -15.8) * mm, "mid": v(876.6, -15.64) * mm, "end": v(877, -14.84) * mm});
            skArc(sketch, "E126.9.0.96", {"start": v(939, -42.25) * mm, "mid": v(941.3, -41.3) * mm, "end": v(942.25, -39) * mm});
            skLineSegment(sketch, "E126.9.0.97", {"start": v(909.27, 23) * mm, "end": v(914.84, 23) * mm});
            skLineSegment(sketch, "E126.9.0.98", {"start": v(877, -9.27) * mm, "end": v(877, -14.84) * mm});
            skArc(sketch, "E126.9.0.99", {"start": v(920.53, -23) * mm, "mid": v(919.3, -23.41) * mm, "end": v(918.6, -24.48) * mm});
            skArc(sketch, "E126.9.0.100", {"start": v(942.25, 39) * mm, "mid": v(941.3, 41.3) * mm, "end": v(939, 42.25) * mm});
            skArc(sketch, "E126.9.0.101", {"start": v(924.48, -18.6) * mm, "mid": v(923.41, -19.3) * mm, "end": v(923, -20.53) * mm});
            skLineSegment(sketch, "E126.9.0.102", {"start": v(879, 23) * mm, "end": v(879.47, 23) * mm});
            skArc(sketch, "E126.9.0.103", {"start": v(920.25, 7.4) * mm, "mid": v(920.26, 7.23) * mm, "end": v(920.3, 7.07) * mm});
            skLineSegment(sketch, "E126.9.0.104", {"start": v(921, -23) * mm, "end": v(920.53, -23) * mm});
            skArc(sketch, "E126.9.0.105", {"start": v(879, 23) * mm, "mid": v(877.59, 22.41) * mm, "end": v(877, 21) * mm});
            skArc(sketch, "E126.9.0.106", {"start": v(892.6, 20.25) * mm, "mid": v(892.77, 20.26) * mm, "end": v(892.93, 20.3) * mm});
            skArc(sketch, "E126.9.0.107", {"start": v(920.3, -7.07) * mm, "mid": v(920.26, -7.23) * mm, "end": v(920.25, -7.4) * mm});
            skLineSegment(sketch, "E126.9.0.108", {"start": v(877, 20.53) * mm, "end": v(877, 21) * mm});
            skArc(sketch, "E126.9.0.109", {"start": v(877, -9.27) * mm, "mid": v(876.98, -9.06) * mm, "end": v(876.91, -8.86) * mm});
            skArc(sketch, "E126.9.0.110", {"start": v(892.93, -20.3) * mm, "mid": v(892.77, -20.26) * mm, "end": v(892.6, -20.25) * mm});
            skArc(sketch, "E126.9.0.111", {"start": v(879.75, -7.4) * mm, "mid": v(879.74, -7.23) * mm, "end": v(879.7, -7.07) * mm});
            skArc(sketch, "E126.9.0.112", {"start": v(923, 9.27) * mm, "mid": v(923.02, 9.06) * mm, "end": v(923.09, 8.86) * mm});
            skArc(sketch, "E126.9.0.113", {"start": v(891.14, -23.09) * mm, "mid": v(890.94, -23.02) * mm, "end": v(890.73, -23) * mm});
            skArc(sketch, "E126.9.0.114", {"start": v(921, -23) * mm, "mid": v(922.41, -22.41) * mm, "end": v(923, -21) * mm});
            skArc(sketch, "E126.9.0.115", {"start": v(890.73, 23) * mm, "mid": v(890.94, 23.02) * mm, "end": v(891.14, 23.09) * mm});
            skArc(sketch, "E126.9.0.116", {"start": v(877, -20.53) * mm, "mid": v(876.59, -19.3) * mm, "end": v(875.52, -18.6) * mm});
            skArc(sketch, "E126.9.0.117", {"start": v(879.75, -19.25) * mm, "mid": v(880.04, -19.96) * mm, "end": v(880.75, -20.25) * mm});
            skArc(sketch, "E126.9.0.118", {"start": v(879.7, 7.07) * mm, "mid": v(879.74, 7.23) * mm, "end": v(879.75, 7.4) * mm});
            skArc(sketch, "E126.9.0.119", {"start": v(879.47, 23) * mm, "mid": v(880.7, 23.41) * mm, "end": v(881.4, 24.48) * mm});
            skLineSegment(sketch, "E126.9.0.120", {"start": v(879.47, -23) * mm, "end": v(879, -23) * mm});
            skArc(sketch, "E126.9.0.121", {"start": v(877, -21) * mm, "mid": v(877.59, -22.41) * mm, "end": v(879, -23) * mm});
            skArc(sketch, "E126.9.0.122", {"start": v(923.09, -8.86) * mm, "mid": v(923.02, -9.06) * mm, "end": v(923, -9.27) * mm});
            skLineSegment(sketch, "E126.9.0.123", {"start": v(877, -21) * mm, "end": v(877, -20.53) * mm});
            skArc(sketch, "E126.9.0.124", {"start": v(881.4, -24.48) * mm, "mid": v(880.7, -23.41) * mm, "end": v(879.47, -23) * mm});
            skLineSegment(sketch, "E126.9.0.125", {"start": v(923, -20.53) * mm, "end": v(923, -21) * mm});
            skLineSegment(sketch, "E126.direction1", {"start": v(-39, -45) * mm, "end": v(61, -45) * mm, "construction": true});
            skSolve(sketch);
        }
        {
            var Q0;
            Q0=makeQuery(id+"F0.imprint","IMPRINT",FACE,{"disambiguationData":[TD([[makeQuery(id+"F0.imprint","IMPRINT",EDGE,{"derivedFrom":sQuery(id+"F0.wireOp",EDGE,"E0")}),-1.0]])]});
            extrude(context, id + "F1", {"entities" : qUnion([Q0]), "depth" : 1000 * mm, "offsetDistance" : 25 * mm});
        }
    });
